# Revit family: Specialty_Equipment-Planter-Planters_Unlimited-Madera-Square-Rectangular
name_source: partatom
category: Specialty Equipment
units: mm (PartAtom-declared; Revit-internal decimal feet)

## family parameters
Always vertical = Yes
Cut with Voids When Loaded = No
Enable Cutting in Views = Yes
Maintain Annotation Orientation = No
OmniClass Number = 23.40.05.21.17
OmniClass Title = Planters
Part Type = Normal
Room Calculation Point = No
Round Connector Dimension = Use Diameter
Shared = No
Work Plane-Based = No

## types (1344) — shared parameters
Assembly Code = G2050600
CD_Height Max = 60"
CD_Height Min = 18"
CD_Length Max = 120"
CD_Length Min = 18"
CD_Offset = 0"
CD_Product Name = Madera Planter
CD_Product Page URL = https://www.plantersunlimited.com
CD_Specification = https://www.plantersunlimited.com
CD_Width Max = 72"
CD_Width Min = 12"
Default Elevation = 0"
Description = Modular Planting Bed
Manufacturer = Planters Unlimited
Material = Plastic-Fiberglass-Carlsbad-Faux Wood-Grey
Model = Madera Series Planters
Stiffeners Horizontal = Yes
Type Comments = Rectangular/Square Planter
URL = https://www.plantersunlimited.com

## per-type parameters (varying)
| type | CD_Height | CD_Length | CD_Requested Height | CD_Requested Length | CD_Requested Length Bottom | CD_Requested Width | CD_Requested Width Bottom | CD_Width | Center Divider | Center Divider Visibility by Length | Diagonal Support | Diagonal Support Visibility by Length | Rectangle Planter | Square Planter |
| Rectangular 18" x 12" x 18" | 18" | 18" | 18" | 18" | 12" | 12" | 8" | 12" | No | No | No | No | Yes | No |
| Rectangular 18" x 12" x 24" | 24" | 18" | 24" | 18" | 12" | 12" | 8" | 12" | No | No | No | No | Yes | No |
| Rectangular 18" x 12" x 30" | 30" | 18" | 30" | 18" | 12" | 12" | 8" | 12" | No | No | No | No | Yes | No |
| Rectangular 18" x 12" x 36" | 36" | 18" | 36" | 18" | 12" | 12" | 8" | 12" | No | No | No | No | Yes | No |
| Rectangular 18" x 15" x 18" | 18" | 18" | 18" | 18" | 12" | 15" | 10" | 15" | No | No | No | No | Yes | No |
| Rectangular 18" x 15" x 24" | 24" | 18" | 24" | 18" | 12" | 15" | 10" | 15" | No | No | No | No | Yes | No |
| Rectangular 18" x 15" x 30" | 30" | 18" | 30" | 18" | 12" | 15" | 10" | 15" | No | No | No | No | Yes | No |
| Rectangular 18" x 15" x 36" | 36" | 18" | 36" | 18" | 12" | 15" | 10" | 15" | No | No | No | No | Yes | No |
| Rectangular 18" x 15" x 42" | 42" | 18" | 42" | 18" | 12" | 15" | 10" | 15" | No | No | No | No | Yes | No |
| Rectangular 18" x 15" x 48" | 48" | 18" | 48" | 18" | 12" | 15" | 10" | 15" | No | No | No | No | Yes | No |
| Rectangular 18" x 15" x 54" | 54" | 18" | 54" | 18" | 12" | 15" | 10" | 15" | No | No | No | No | Yes | No |
| Rectangular 18" x 15" x 60" | 60" | 18" | 60" | 18" | 12" | 15" | 10" | 15" | No | No | No | No | Yes | No |
| Square 18" x 18" x 18" | 18" | 18" | 18" | 18" | 12" | 18" | 12" | 18" | No | No | No | No | No | Yes |
| Square 18" x 18" x 24" | 24" | 18" | 24" | 18" | 12" | 18" | 12" | 18" | No | No | No | No | No | Yes |
| Square 18" x 18" x 30" | 30" | 18" | 30" | 18" | 12" | 18" | 12" | 18" | No | No | No | No | No | Yes |
| Square 18" x 18" x 36" | 36" | 18" | 36" | 18" | 12" | 18" | 12" | 18" | No | No | No | No | No | Yes |
| Square 18" x 18" x 42" | 42" | 18" | 42" | 18" | 12" | 18" | 12" | 18" | No | No | No | No | No | Yes |
| Square 18" x 18" x 48" | 48" | 18" | 48" | 18" | 12" | 18" | 12" | 18" | No | No | No | No | No | Yes |
| Square 18" x 18" x 54" | 54" | 18" | 54" | 18" | 12" | 18" | 12" | 18" | No | No | No | No | No | Yes |
| Square 18" x 18" x 60" | 60" | 18" | 60" | 18" | 12" | 18" | 12" | 18" | No | No | No | No | No | Yes |
| Rectangular 18" x 24" x 18" | 18" | 18" | 18" | 18" | 12" | 24" | 16" | 24" | No | No | No | No | Yes | No |
| Rectangular 18" x 24" x 24" | 24" | 18" | 24" | 18" | 12" | 24" | 16" | 24" | No | No | No | No | Yes | No |
| Rectangular 18" x 24" x 30" | 30" | 18" | 30" | 18" | 12" | 24" | 16" | 24" | No | No | No | No | Yes | No |
| Rectangular 18" x 24" x 36" | 36" | 18" | 36" | 18" | 12" | 24" | 16" | 24" | No | No | No | No | Yes | No |
| Rectangular 18" x 24" x 42" | 42" | 18" | 42" | 18" | 12" | 24" | 16" | 24" | No | No | No | No | Yes | No |
| Rectangular 18" x 24" x 48" | 48" | 18" | 48" | 18" | 12" | 24" | 16" | 24" | No | No | No | No | Yes | No |
| Rectangular 18" x 24" x 54" | 54" | 18" | 54" | 18" | 12" | 24" | 16" | 24" | No | No | No | No | Yes | No |
| Rectangular 18" x 24" x 60" | 60" | 18" | 60" | 18" | 12" | 24" | 16" | 24" | No | No | No | No | Yes | No |
| Rectangular 18" x 30" x 18" | 18" | 18" | 18" | 18" | 12" | 30" | 20" | 30" | No | No | No | No | Yes | No |
| Rectangular 18" x 30" x 24" | 24" | 18" | 24" | 18" | 12" | 30" | 20" | 30" | No | No | No | No | Yes | No |
| Rectangular 18" x 30" x 30" | 30" | 18" | 30" | 18" | 12" | 30" | 20" | 30" | No | No | No | No | Yes | No |
| Rectangular 18" x 30" x 36" | 36" | 18" | 36" | 18" | 12" | 30" | 20" | 30" | No | No | No | No | Yes | No |
| Rectangular 18" x 30" x 42" | 42" | 18" | 42" | 18" | 12" | 30" | 20" | 30" | No | No | No | No | Yes | No |
| Rectangular 18" x 30" x 48" | 48" | 18" | 48" | 18" | 12" | 30" | 20" | 30" | No | No | No | No | Yes | No |
| Rectangular 18" x 30" x 54" | 54" | 18" | 54" | 18" | 12" | 30" | 20" | 30" | No | No | No | No | Yes | No |
| Rectangular 18" x 30" x 60" | 60" | 18" | 60" | 18" | 12" | 30" | 20" | 30" | No | No | No | No | Yes | No |
| Rectangular 18" x 36" x 18" | 18" | 18" | 18" | 18" | 12" | 36" | 24" | 36" | No | No | No | No | Yes | No |
| Rectangular 18" x 36" x 24" | 24" | 18" | 24" | 18" | 12" | 36" | 24" | 36" | No | No | No | No | Yes | No |
| Rectangular 18" x 36" x 30" | 30" | 18" | 30" | 18" | 12" | 36" | 24" | 36" | No | No | No | No | Yes | No |
| Rectangular 18" x 36" x 36" | 36" | 18" | 36" | 18" | 12" | 36" | 24" | 36" | No | No | No | No | Yes | No |
| Rectangular 18" x 36" x 42" | 42" | 18" | 42" | 18" | 12" | 36" | 24" | 36" | No | No | No | No | Yes | No |
| Rectangular 18" x 36" x 48" | 48" | 18" | 48" | 18" | 12" | 36" | 24" | 36" | No | No | No | No | Yes | No |
| Rectangular 18" x 36" x 54" | 54" | 18" | 54" | 18" | 12" | 36" | 24" | 36" | No | No | No | No | Yes | No |
| Rectangular 18" x 36" x 60" | 60" | 18" | 60" | 18" | 12" | 36" | 24" | 36" | No | No | No | No | Yes | No |
| Rectangular 18" x 42" x 18" | 18" | 18" | 18" | 18" | 12" | 42" | 28" | 42" | No | No | No | No | Yes | No |
| Rectangular 18" x 42" x 24" | 24" | 18" | 24" | 18" | 12" | 42" | 28" | 42" | No | No | No | No | Yes | No |
| Rectangular 18" x 42" x 30" | 30" | 18" | 30" | 18" | 12" | 42" | 28" | 42" | No | No | No | No | Yes | No |
| Rectangular 18" x 42" x 36" | 36" | 18" | 36" | 18" | 12" | 42" | 28" | 42" | No | No | No | No | Yes | No |
| Rectangular 18" x 42" x 42" | 42" | 18" | 42" | 18" | 12" | 42" | 28" | 42" | No | No | No | No | Yes | No |
| Rectangular 18" x 42" x 48" | 48" | 18" | 48" | 18" | 12" | 42" | 28" | 42" | No | No | No | No | Yes | No |
| Rectangular 18" x 42" x 54" | 54" | 18" | 54" | 18" | 12" | 42" | 28" | 42" | No | No | No | No | Yes | No |
| Rectangular 18" x 42" x 60" | 60" | 18" | 60" | 18" | 12" | 42" | 28" | 42" | No | No | No | No | Yes | No |
| Rectangular 18" x 48" x 18" | 18" | 18" | 18" | 18" | 12" | 48" | 32" | 48" | No | No | No | No | Yes | No |
| Rectangular 18" x 48" x 24" | 24" | 18" | 24" | 18" | 12" | 48" | 32" | 48" | No | No | No | No | Yes | No |
| Rectangular 18" x 48" x 30" | 30" | 18" | 30" | 18" | 12" | 48" | 32" | 48" | No | No | No | No | Yes | No |
| Rectangular 18" x 48" x 36" | 36" | 18" | 36" | 18" | 12" | 48" | 32" | 48" | No | No | No | No | Yes | No |
| Rectangular 18" x 48" x 42" | 42" | 18" | 42" | 18" | 12" | 48" | 32" | 48" | No | No | No | No | Yes | No |
| Rectangular 18" x 48" x 48" | 48" | 18" | 48" | 18" | 12" | 48" | 32" | 48" | No | No | No | No | Yes | No |
| Rectangular 18" x 48" x 54" | 54" | 18" | 54" | 18" | 12" | 48" | 32" | 48" | No | No | No | No | Yes | No |
| Rectangular 18" x 48" x 60" | 60" | 18" | 60" | 18" | 12" | 48" | 32" | 48" | No | No | No | No | Yes | No |
| Rectangular 18" x 60" x 18" | 18" | 18" | 18" | 18" | 12" | 60" | 40" | 60" | No | No | No | No | Yes | No |
| Rectangular 18" x 60" x 24" | 24" | 18" | 24" | 18" | 12" | 60" | 40" | 60" | No | No | No | No | Yes | No |
| Rectangular 18" x 60" x 30" | 30" | 18" | 30" | 18" | 12" | 60" | 40" | 60" | No | No | No | No | Yes | No |
| Rectangular 18" x 60" x 36" | 36" | 18" | 36" | 18" | 12" | 60" | 40" | 60" | No | No | No | No | Yes | No |
| Rectangular 18" x 60" x 42" | 42" | 18" | 42" | 18" | 12" | 60" | 40" | 60" | No | No | No | No | Yes | No |
| Rectangular 18" x 60" x 48" | 48" | 18" | 48" | 18" | 12" | 60" | 40" | 60" | No | No | No | No | Yes | No |
| Rectangular 18" x 60" x 54" | 54" | 18" | 54" | 18" | 12" | 60" | 40" | 60" | No | No | No | No | Yes | No |
| Rectangular 18" x 60" x 60" | 60" | 18" | 60" | 18" | 12" | 60" | 40" | 60" | No | No | No | No | Yes | No |
| Rectangular 18" x 66" x 18" | 18" | 18" | 18" | 18" | 12" | 66" | 44" | 66" | No | No | No | No | Yes | No |
| Rectangular 18" x 66" x 24" | 24" | 18" | 24" | 18" | 12" | 66" | 44" | 66" | No | No | No | No | Yes | No |
| Rectangular 18" x 66" x 30" | 30" | 18" | 30" | 18" | 12" | 66" | 44" | 66" | No | No | No | No | Yes | No |
| Rectangular 18" x 66" x 36" | 36" | 18" | 36" | 18" | 12" | 66" | 44" | 66" | No | No | No | No | Yes | No |
| Rectangular 18" x 66" x 42" | 42" | 18" | 42" | 18" | 12" | 66" | 44" | 66" | No | No | No | No | Yes | No |
| Rectangular 18" x 66" x 48" | 48" | 18" | 48" | 18" | 12" | 66" | 44" | 66" | No | No | No | No | Yes | No |
| Rectangular 18" x 66" x 54" | 54" | 18" | 54" | 18" | 12" | 66" | 44" | 66" | No | No | No | No | Yes | No |
| Rectangular 18" x 66" x 60" | 60" | 18" | 60" | 18" | 12" | 66" | 44" | 66" | No | No | No | No | Yes | No |
| Rectangular 18" x 72" x 18" | 18" | 18" | 18" | 18" | 12" | 72" | 48" | 72" | No | No | No | No | Yes | No |
| Rectangular 18" x 72" x 24" | 24" | 18" | 24" | 18" | 12" | 72" | 48" | 72" | No | No | No | No | Yes | No |
| Rectangular 18" x 72" x 30" | 30" | 18" | 30" | 18" | 12" | 72" | 48" | 72" | No | No | No | No | Yes | No |
| Rectangular 18" x 72" x 36" | 36" | 18" | 36" | 18" | 12" | 72" | 48" | 72" | No | No | No | No | Yes | No |
| Rectangular 18" x 72" x 42" | 42" | 18" | 42" | 18" | 12" | 72" | 48" | 72" | No | No | No | No | Yes | No |
| Rectangular 18" x 72" x 48" | 48" | 18" | 48" | 18" | 12" | 72" | 48" | 72" | No | No | No | No | Yes | No |
| Rectangular 18" x 72" x 54" | 54" | 18" | 54" | 18" | 12" | 72" | 48" | 72" | No | No | No | No | Yes | No |
| Rectangular 18" x 72" x 60" | 60" | 18" | 60" | 18" | 12" | 72" | 48" | 72" | No | No | No | No | Yes | No |
| Rectangular 24" x 12" x 18" | 18" | 24" | 18" | 24" | 16" | 12" | 8" | 12" | No | No | No | No | Yes | No |
| Rectangular 24" x 12" x 24" | 24" | 24" | 24" | 24" | 16" | 12" | 8" | 12" | No | No | No | No | Yes | No |
| Rectangular 24" x 12" x 30" | 30" | 24" | 30" | 24" | 16" | 12" | 8" | 12" | No | No | No | No | Yes | No |
| Rectangular 24" x 12" x 36" | 36" | 24" | 36" | 24" | 16" | 12" | 8" | 12" | No | No | No | No | Yes | No |
| Rectangular 24" x 15" x 18" | 18" | 24" | 18" | 24" | 16" | 15" | 10" | 15" | No | No | No | No | Yes | No |
| Rectangular 24" x 15" x 24" | 24" | 24" | 24" | 24" | 16" | 15" | 10" | 15" | No | No | No | No | Yes | No |
| Rectangular 24" x 15" x 30" | 30" | 24" | 30" | 24" | 16" | 15" | 10" | 15" | No | No | No | No | Yes | No |
| Rectangular 24" x 15" x 36" | 36" | 24" | 36" | 24" | 16" | 15" | 10" | 15" | No | No | No | No | Yes | No |
| Rectangular 24" x 15" x 42" | 42" | 24" | 42" | 24" | 16" | 15" | 10" | 15" | No | No | No | No | Yes | No |
| Rectangular 24" x 15" x 48" | 48" | 24" | 48" | 24" | 16" | 15" | 10" | 15" | No | No | No | No | Yes | No |
| Rectangular 24" x 15" x 54" | 54" | 24" | 54" | 24" | 16" | 15" | 10" | 15" | No | No | No | No | Yes | No |
| Rectangular 24" x 15" x 60" | 60" | 24" | 60" | 24" | 16" | 15" | 10" | 15" | No | No | No | No | Yes | No |
| Rectangular 24" x 18" x 18" | 18" | 24" | 18" | 24" | 16" | 18" | 12" | 18" | No | No | No | No | Yes | No |
| Rectangular 24" x 18" x 24" | 24" | 24" | 24" | 24" | 16" | 18" | 12" | 18" | No | No | No | No | Yes | No |
| Rectangular 24" x 18" x 30" | 30" | 24" | 30" | 24" | 16" | 18" | 12" | 18" | No | No | No | No | Yes | No |
| Rectangular 24" x 18" x 36" | 36" | 24" | 36" | 24" | 16" | 18" | 12" | 18" | No | No | No | No | Yes | No |
| Rectangular 24" x 18" x 42" | 42" | 24" | 42" | 24" | 16" | 18" | 12" | 18" | No | No | No | No | Yes | No |
| Rectangular 24" x 18" x 48" | 48" | 24" | 48" | 24" | 16" | 18" | 12" | 18" | No | No | No | No | Yes | No |
| Rectangular 24" x 18" x 54" | 54" | 24" | 54" | 24" | 16" | 18" | 12" | 18" | No | No | No | No | Yes | No |
| Rectangular 24" x 18" x 60" | 60" | 24" | 60" | 24" | 16" | 18" | 12" | 18" | No | No | No | No | Yes | No |
| Square 24" x 24" x 18" | 18" | 24" | 18" | 24" | 16" | 24" | 16" | 24" | No | No | No | No | No | Yes |
| Square 24" x 24" x 24" | 24" | 24" | 24" | 24" | 16" | 24" | 16" | 24" | No | No | No | No | No | Yes |
| Square 24" x 24" x 30" | 30" | 24" | 30" | 24" | 16" | 24" | 16" | 24" | No | No | No | No | No | Yes |
| Square 24" x 24" x 36" | 36" | 24" | 36" | 24" | 16" | 24" | 16" | 24" | No | No | No | No | No | Yes |
| Square 24" x 24" x 42" | 42" | 24" | 42" | 24" | 16" | 24" | 16" | 24" | No | No | No | No | No | Yes |
| Square 24" x 24" x 48" | 48" | 24" | 48" | 24" | 16" | 24" | 16" | 24" | No | No | No | No | No | Yes |
| Square 24" x 24" x 54" | 54" | 24" | 54" | 24" | 16" | 24" | 16" | 24" | No | No | No | No | No | Yes |
| Square 24" x 24" x 60" | 60" | 24" | 60" | 24" | 16" | 24" | 16" | 24" | No | No | No | No | No | Yes |
| Rectangular 24" x 30" x 18" | 18" | 24" | 18" | 24" | 16" | 30" | 20" | 30" | No | No | No | No | Yes | No |
| Rectangular 24" x 30" x 24" | 24" | 24" | 24" | 24" | 16" | 30" | 20" | 30" | No | No | No | No | Yes | No |
| Rectangular 24" x 30" x 30" | 30" | 24" | 30" | 24" | 16" | 30" | 20" | 30" | No | No | No | No | Yes | No |
| Rectangular 24" x 30" x 36" | 36" | 24" | 36" | 24" | 16" | 30" | 20" | 30" | No | No | No | No | Yes | No |
| Rectangular 24" x 30" x 42" | 42" | 24" | 42" | 24" | 16" | 30" | 20" | 30" | No | No | No | No | Yes | No |
| Rectangular 24" x 30" x 48" | 48" | 24" | 48" | 24" | 16" | 30" | 20" | 30" | No | No | No | No | Yes | No |
| Rectangular 24" x 30" x 54" | 54" | 24" | 54" | 24" | 16" | 30" | 20" | 30" | No | No | No | No | Yes | No |
| Rectangular 24" x 30" x 60" | 60" | 24" | 60" | 24" | 16" | 30" | 20" | 30" | No | No | No | No | Yes | No |
| Rectangular 24" x 36" x 18" | 18" | 24" | 18" | 24" | 16" | 36" | 24" | 36" | No | No | No | No | Yes | No |
| Rectangular 24" x 36" x 24" | 24" | 24" | 24" | 24" | 16" | 36" | 24" | 36" | No | No | No | No | Yes | No |
| Rectangular 24" x 36" x 30" | 30" | 24" | 30" | 24" | 16" | 36" | 24" | 36" | No | No | No | No | Yes | No |
| Rectangular 24" x 36" x 36" | 36" | 24" | 36" | 24" | 16" | 36" | 24" | 36" | No | No | No | No | Yes | No |
| Rectangular 24" x 36" x 42" | 42" | 24" | 42" | 24" | 16" | 36" | 24" | 36" | No | No | No | No | Yes | No |
| Rectangular 24" x 36" x 48" | 48" | 24" | 48" | 24" | 16" | 36" | 24" | 36" | No | No | No | No | Yes | No |
| Rectangular 24" x 36" x 54" | 54" | 24" | 54" | 24" | 16" | 36" | 24" | 36" | No | No | No | No | Yes | No |
| Rectangular 24" x 36" x 60" | 60" | 24" | 60" | 24" | 16" | 36" | 24" | 36" | No | No | No | No | Yes | No |
| Rectangular 24" x 42" x 18" | 18" | 24" | 18" | 24" | 16" | 42" | 28" | 42" | No | No | No | No | Yes | No |
| Rectangular 24" x 42" x 24" | 24" | 24" | 24" | 24" | 16" | 42" | 28" | 42" | No | No | No | No | Yes | No |
| Rectangular 24" x 42" x 30" | 30" | 24" | 30" | 24" | 16" | 42" | 28" | 42" | No | No | No | No | Yes | No |
| Rectangular 24" x 42" x 36" | 36" | 24" | 36" | 24" | 16" | 42" | 28" | 42" | No | No | No | No | Yes | No |
| Rectangular 24" x 42" x 42" | 42" | 24" | 42" | 24" | 16" | 42" | 28" | 42" | No | No | No | No | Yes | No |
| Rectangular 24" x 42" x 48" | 48" | 24" | 48" | 24" | 16" | 42" | 28" | 42" | No | No | No | No | Yes | No |
| Rectangular 24" x 42" x 54" | 54" | 24" | 54" | 24" | 16" | 42" | 28" | 42" | No | No | No | No | Yes | No |
| Rectangular 24" x 42" x 60" | 60" | 24" | 60" | 24" | 16" | 42" | 28" | 42" | No | No | No | No | Yes | No |
| Rectangular 24" x 48" x 18" | 18" | 24" | 18" | 24" | 16" | 48" | 32" | 48" | No | No | No | No | Yes | No |
| Rectangular 24" x 48" x 24" | 24" | 24" | 24" | 24" | 16" | 48" | 32" | 48" | No | No | No | No | Yes | No |
| Rectangular 24" x 48" x 30" | 30" | 24" | 30" | 24" | 16" | 48" | 32" | 48" | No | No | No | No | Yes | No |
| Rectangular 24" x 48" x 36" | 36" | 24" | 36" | 24" | 16" | 48" | 32" | 48" | No | No | No | No | Yes | No |
| Rectangular 24" x 48" x 42" | 42" | 24" | 42" | 24" | 16" | 48" | 32" | 48" | No | No | No | No | Yes | No |
| Rectangular 24" x 48" x 48" | 48" | 24" | 48" | 24" | 16" | 48" | 32" | 48" | No | No | No | No | Yes | No |
| Rectangular 24" x 48" x 54" | 54" | 24" | 54" | 24" | 16" | 48" | 32" | 48" | No | No | No | No | Yes | No |
| Rectangular 24" x 48" x 60" | 60" | 24" | 60" | 24" | 16" | 48" | 32" | 48" | No | No | No | No | Yes | No |
| Rectangular 24" x 60" x 18" | 18" | 24" | 18" | 24" | 16" | 60" | 40" | 60" | No | No | No | No | Yes | No |
| Rectangular 24" x 60" x 24" | 24" | 24" | 24" | 24" | 16" | 60" | 40" | 60" | No | No | No | No | Yes | No |
| Rectangular 24" x 60" x 30" | 30" | 24" | 30" | 24" | 16" | 60" | 40" | 60" | No | No | No | No | Yes | No |
| Rectangular 24" x 60" x 36" | 36" | 24" | 36" | 24" | 16" | 60" | 40" | 60" | No | No | No | No | Yes | No |
| Rectangular 24" x 60" x 42" | 42" | 24" | 42" | 24" | 16" | 60" | 40" | 60" | No | No | No | No | Yes | No |
| Rectangular 24" x 60" x 48" | 48" | 24" | 48" | 24" | 16" | 60" | 40" | 60" | No | No | No | No | Yes | No |
| Rectangular 24" x 60" x 54" | 54" | 24" | 54" | 24" | 16" | 60" | 40" | 60" | No | No | No | No | Yes | No |
| Rectangular 24" x 60" x 60" | 60" | 24" | 60" | 24" | 16" | 60" | 40" | 60" | No | No | No | No | Yes | No |
| Rectangular 24" x 66" x 18" | 18" | 24" | 18" | 24" | 16" | 66" | 44" | 66" | No | No | No | No | Yes | No |
| Rectangular 24" x 66" x 24" | 24" | 24" | 24" | 24" | 16" | 66" | 44" | 66" | No | No | No | No | Yes | No |
| Rectangular 24" x 66" x 30" | 30" | 24" | 30" | 24" | 16" | 66" | 44" | 66" | No | No | No | No | Yes | No |
| Rectangular 24" x 66" x 36" | 36" | 24" | 36" | 24" | 16" | 66" | 44" | 66" | No | No | No | No | Yes | No |
| Rectangular 24" x 66" x 42" | 42" | 24" | 42" | 24" | 16" | 66" | 44" | 66" | No | No | No | No | Yes | No |
| Rectangular 24" x 66" x 48" | 48" | 24" | 48" | 24" | 16" | 66" | 44" | 66" | No | No | No | No | Yes | No |
| Rectangular 24" x 66" x 54" | 54" | 24" | 54" | 24" | 16" | 66" | 44" | 66" | No | No | No | No | Yes | No |
| Rectangular 24" x 66" x 60" | 60" | 24" | 60" | 24" | 16" | 66" | 44" | 66" | No | No | No | No | Yes | No |
| Rectangular 24" x 72" x 18" | 18" | 24" | 18" | 24" | 16" | 72" | 48" | 72" | No | No | No | No | Yes | No |
| Rectangular 24" x 72" x 24" | 24" | 24" | 24" | 24" | 16" | 72" | 48" | 72" | No | No | No | No | Yes | No |
| Rectangular 24" x 72" x 30" | 30" | 24" | 30" | 24" | 16" | 72" | 48" | 72" | No | No | No | No | Yes | No |
| Rectangular 24" x 72" x 36" | 36" | 24" | 36" | 24" | 16" | 72" | 48" | 72" | No | No | No | No | Yes | No |
| Rectangular 24" x 72" x 42" | 42" | 24" | 42" | 24" | 16" | 72" | 48" | 72" | No | No | No | No | Yes | No |
| Rectangular 24" x 72" x 48" | 48" | 24" | 48" | 24" | 16" | 72" | 48" | 72" | No | No | No | No | Yes | No |
| Rectangular 24" x 72" x 54" | 54" | 24" | 54" | 24" | 16" | 72" | 48" | 72" | No | No | No | No | Yes | No |
| Rectangular 24" x 72" x 60" | 60" | 24" | 60" | 24" | 16" | 72" | 48" | 72" | No | No | No | No | Yes | No |
| Rectangular 30" x 12" x 18" | 18" | 30" | 18" | 30" | 20" | 12" | 8" | 12" | No | No | No | No | Yes | No |
| Rectangular 30" x 12" x 24" | 24" | 30" | 24" | 30" | 20" | 12" | 8" | 12" | No | No | No | No | Yes | No |
| Rectangular 30" x 12" x 30" | 30" | 30" | 30" | 30" | 20" | 12" | 8" | 12" | No | No | No | No | Yes | No |
| Rectangular 30" x 12" x 36" | 36" | 30" | 36" | 30" | 20" | 12" | 8" | 12" | No | No | No | No | Yes | No |
| Rectangular 30" x 15" x 18" | 18" | 30" | 18" | 30" | 20" | 15" | 10" | 15" | No | No | No | No | Yes | No |
| Rectangular 30" x 15" x 24" | 24" | 30" | 24" | 30" | 20" | 15" | 10" | 15" | No | No | No | No | Yes | No |
| Rectangular 30" x 15" x 30" | 30" | 30" | 30" | 30" | 20" | 15" | 10" | 15" | No | No | No | No | Yes | No |
| Rectangular 30" x 15" x 36" | 36" | 30" | 36" | 30" | 20" | 15" | 10" | 15" | No | No | No | No | Yes | No |
| Rectangular 30" x 15" x 42" | 42" | 30" | 42" | 30" | 20" | 15" | 10" | 15" | No | No | No | No | Yes | No |
| Rectangular 30" x 15" x 48" | 48" | 30" | 48" | 30" | 20" | 15" | 10" | 15" | No | No | No | No | Yes | No |
| Rectangular 30" x 15" x 54" | 54" | 30" | 54" | 30" | 20" | 15" | 10" | 15" | No | No | No | No | Yes | No |
| Rectangular 30" x 15" x 60" | 60" | 30" | 60" | 30" | 20" | 15" | 10" | 15" | No | No | No | No | Yes | No |
| Rectangular 30" x 18" x 18" | 18" | 30" | 18" | 30" | 20" | 18" | 12" | 18" | No | No | No | No | Yes | No |
| Rectangular 30" x 18" x 24" | 24" | 30" | 24" | 30" | 20" | 18" | 12" | 18" | No | No | No | No | Yes | No |
| Rectangular 30" x 18" x 30" | 30" | 30" | 30" | 30" | 20" | 18" | 12" | 18" | No | No | No | No | Yes | No |
| Rectangular 30" x 18" x 36" | 36" | 30" | 36" | 30" | 20" | 18" | 12" | 18" | No | No | No | No | Yes | No |
| Rectangular 30" x 18" x 42" | 42" | 30" | 42" | 30" | 20" | 18" | 12" | 18" | No | No | No | No | Yes | No |
| Rectangular 30" x 18" x 48" | 48" | 30" | 48" | 30" | 20" | 18" | 12" | 18" | No | No | No | No | Yes | No |
| Rectangular 30" x 18" x 54" | 54" | 30" | 54" | 30" | 20" | 18" | 12" | 18" | No | No | No | No | Yes | No |
| Rectangular 30" x 18" x 60" | 60" | 30" | 60" | 30" | 20" | 18" | 12" | 18" | No | No | No | No | Yes | No |
| Rectangular 30" x 24" x 18" | 18" | 30" | 18" | 30" | 20" | 24" | 16" | 24" | No | No | No | No | Yes | No |
| Rectangular 30" x 24" x 24" | 24" | 30" | 24" | 30" | 20" | 24" | 16" | 24" | No | No | No | No | Yes | No |
| Rectangular 30" x 24" x 30" | 30" | 30" | 30" | 30" | 20" | 24" | 16" | 24" | No | No | No | No | Yes | No |
| Rectangular 30" x 24" x 36" | 36" | 30" | 36" | 30" | 20" | 24" | 16" | 24" | No | No | No | No | Yes | No |
| Rectangular 30" x 24" x 42" | 42" | 30" | 42" | 30" | 20" | 24" | 16" | 24" | No | No | No | No | Yes | No |
| Rectangular 30" x 24" x 48" | 48" | 30" | 48" | 30" | 20" | 24" | 16" | 24" | No | No | No | No | Yes | No |
| Rectangular 30" x 24" x 54" | 54" | 30" | 54" | 30" | 20" | 24" | 16" | 24" | No | No | No | No | Yes | No |
| Rectangular 30" x 24" x 60" | 60" | 30" | 60" | 30" | 20" | 24" | 16" | 24" | No | No | No | No | Yes | No |
| Square 30" x 30" x 18" | 18" | 30" | 18" | 30" | 20" | 30" | 20" | 30" | No | No | No | No | No | Yes |
| Square 30" x 30" x 24" | 24" | 30" | 24" | 30" | 20" | 30" | 20" | 30" | No | No | No | No | No | Yes |
| Square 30" x 30" x 30" | 30" | 30" | 30" | 30" | 20" | 30" | 20" | 30" | No | No | No | No | No | Yes |
| Square 30" x 30" x 36" | 36" | 30" | 36" | 30" | 20" | 30" | 20" | 30" | No | No | No | No | No | Yes |
| Square 30" x 30" x 42" | 42" | 30" | 42" | 30" | 20" | 30" | 20" | 30" | No | No | No | No | No | Yes |
| Square 30" x 30" x 48" | 48" | 30" | 48" | 30" | 20" | 30" | 20" | 30" | No | No | No | No | No | Yes |
| Square 30" x 30" x 54" | 54" | 30" | 54" | 30" | 20" | 30" | 20" | 30" | No | No | No | No | No | Yes |
| Square 30" x 30" x 60" | 60" | 30" | 60" | 30" | 20" | 30" | 20" | 30" | No | No | No | No | No | Yes |
| Rectangular 30" x 36" x 18" | 18" | 30" | 18" | 30" | 20" | 36" | 24" | 36" | No | No | No | No | Yes | No |
| Rectangular 30" x 36" x 24" | 24" | 30" | 24" | 30" | 20" | 36" | 24" | 36" | No | No | No | No | Yes | No |
| Rectangular 30" x 36" x 30" | 30" | 30" | 30" | 30" | 20" | 36" | 24" | 36" | No | No | No | No | Yes | No |
| Rectangular 30" x 36" x 36" | 36" | 30" | 36" | 30" | 20" | 36" | 24" | 36" | No | No | No | No | Yes | No |
| Rectangular 30" x 36" x 42" | 42" | 30" | 42" | 30" | 20" | 36" | 24" | 36" | No | No | No | No | Yes | No |
| Rectangular 30" x 36" x 48" | 48" | 30" | 48" | 30" | 20" | 36" | 24" | 36" | No | No | No | No | Yes | No |
| Rectangular 30" x 36" x 54" | 54" | 30" | 54" | 30" | 20" | 36" | 24" | 36" | No | No | No | No | Yes | No |
| Rectangular 30" x 36" x 60" | 60" | 30" | 60" | 30" | 20" | 36" | 24" | 36" | No | No | No | No | Yes | No |
| Rectangular 30" x 42" x 18" | 18" | 30" | 18" | 30" | 20" | 42" | 28" | 42" | No | No | No | No | Yes | No |
| Rectangular 30" x 42" x 24" | 24" | 30" | 24" | 30" | 20" | 42" | 28" | 42" | No | No | No | No | Yes | No |
| Rectangular 30" x 42" x 30" | 30" | 30" | 30" | 30" | 20" | 42" | 28" | 42" | No | No | No | No | Yes | No |
| Rectangular 30" x 42" x 36" | 36" | 30" | 36" | 30" | 20" | 42" | 28" | 42" | No | No | No | No | Yes | No |
| Rectangular 30" x 42" x 42" | 42" | 30" | 42" | 30" | 20" | 42" | 28" | 42" | No | No | No | No | Yes | No |
| Rectangular 30" x 42" x 48" | 48" | 30" | 48" | 30" | 20" | 42" | 28" | 42" | No | No | No | No | Yes | No |
| Rectangular 30" x 42" x 54" | 54" | 30" | 54" | 30" | 20" | 42" | 28" | 42" | No | No | No | No | Yes | No |
| Rectangular 30" x 42" x 60" | 60" | 30" | 60" | 30" | 20" | 42" | 28" | 42" | No | No | No | No | Yes | No |
| Rectangular 30" x 48" x 18" | 18" | 30" | 18" | 30" | 20" | 48" | 32" | 48" | No | No | No | No | Yes | No |
| Rectangular 30" x 48" x 24" | 24" | 30" | 24" | 30" | 20" | 48" | 32" | 48" | No | No | No | No | Yes | No |
| Rectangular 30" x 48" x 30" | 30" | 30" | 30" | 30" | 20" | 48" | 32" | 48" | No | No | No | No | Yes | No |
| Rectangular 30" x 48" x 36" | 36" | 30" | 36" | 30" | 20" | 48" | 32" | 48" | No | No | No | No | Yes | No |
| Rectangular 30" x 48" x 42" | 42" | 30" | 42" | 30" | 20" | 48" | 32" | 48" | No | No | No | No | Yes | No |
| Rectangular 30" x 48" x 48" | 48" | 30" | 48" | 30" | 20" | 48" | 32" | 48" | No | No | No | No | Yes | No |
| Rectangular 30" x 48" x 54" | 54" | 30" | 54" | 30" | 20" | 48" | 32" | 48" | No | No | No | No | Yes | No |
| Rectangular 30" x 48" x 60" | 60" | 30" | 60" | 30" | 20" | 48" | 32" | 48" | No | No | No | No | Yes | No |
| Rectangular 30" x 60" x 18" | 18" | 30" | 18" | 30" | 20" | 60" | 40" | 60" | No | No | No | No | Yes | No |
| Rectangular 30" x 60" x 24" | 24" | 30" | 24" | 30" | 20" | 60" | 40" | 60" | No | No | No | No | Yes | No |
| Rectangular 30" x 60" x 30" | 30" | 30" | 30" | 30" | 20" | 60" | 40" | 60" | No | No | No | No | Yes | No |
| Rectangular 30" x 60" x 36" | 36" | 30" | 36" | 30" | 20" | 60" | 40" | 60" | No | No | No | No | Yes | No |
| Rectangular 30" x 60" x 42" | 42" | 30" | 42" | 30" | 20" | 60" | 40" | 60" | No | No | No | No | Yes | No |
| Rectangular 30" x 60" x 48" | 48" | 30" | 48" | 30" | 20" | 60" | 40" | 60" | No | No | No | No | Yes | No |
| Rectangular 30" x 60" x 54" | 54" | 30" | 54" | 30" | 20" | 60" | 40" | 60" | No | No | No | No | Yes | No |
| Rectangular 30" x 60" x 60" | 60" | 30" | 60" | 30" | 20" | 60" | 40" | 60" | No | No | No | No | Yes | No |
| Rectangular 30" x 66" x 18" | 18" | 30" | 18" | 30" | 20" | 66" | 44" | 66" | No | No | No | No | Yes | No |
| Rectangular 30" x 66" x 24" | 24" | 30" | 24" | 30" | 20" | 66" | 44" | 66" | No | No | No | No | Yes | No |
| Rectangular 30" x 66" x 30" | 30" | 30" | 30" | 30" | 20" | 66" | 44" | 66" | No | No | No | No | Yes | No |
| Rectangular 30" x 66" x 36" | 36" | 30" | 36" | 30" | 20" | 66" | 44" | 66" | No | No | No | No | Yes | No |
| Rectangular 30" x 66" x 42" | 42" | 30" | 42" | 30" | 20" | 66" | 44" | 66" | No | No | No | No | Yes | No |
| Rectangular 30" x 66" x 48" | 48" | 30" | 48" | 30" | 20" | 66" | 44" | 66" | No | No | No | No | Yes | No |
| Rectangular 30" x 66" x 54" | 54" | 30" | 54" | 30" | 20" | 66" | 44" | 66" | No | No | No | No | Yes | No |
| Rectangular 30" x 66" x 60" | 60" | 30" | 60" | 30" | 20" | 66" | 44" | 66" | No | No | No | No | Yes | No |
| Rectangular 30" x 72" x 18" | 18" | 30" | 18" | 30" | 20" | 72" | 48" | 72" | No | No | No | No | Yes | No |
| Rectangular 30" x 72" x 24" | 24" | 30" | 24" | 30" | 20" | 72" | 48" | 72" | No | No | No | No | Yes | No |
| Rectangular 30" x 72" x 30" | 30" | 30" | 30" | 30" | 20" | 72" | 48" | 72" | No | No | No | No | Yes | No |
| Rectangular 30" x 72" x 36" | 36" | 30" | 36" | 30" | 20" | 72" | 48" | 72" | No | No | No | No | Yes | No |
| Rectangular 30" x 72" x 42" | 42" | 30" | 42" | 30" | 20" | 72" | 48" | 72" | No | No | No | No | Yes | No |
| Rectangular 30" x 72" x 48" | 48" | 30" | 48" | 30" | 20" | 72" | 48" | 72" | No | No | No | No | Yes | No |
| Rectangular 30" x 72" x 54" | 54" | 30" | 54" | 30" | 20" | 72" | 48" | 72" | No | No | No | No | Yes | No |
| Rectangular 30" x 72" x 60" | 60" | 30" | 60" | 30" | 20" | 72" | 48" | 72" | No | No | No | No | Yes | No |
| Rectangular 36" x 12" x 18" | 18" | 36" | 18" | 36" | 24" | 12" | 8" | 12" | No | No | No | No | Yes | No |
| Rectangular 36" x 12" x 24" | 24" | 36" | 24" | 36" | 24" | 12" | 8" | 12" | No | No | No | No | Yes | No |
| Rectangular 36" x 12" x 30" | 30" | 36" | 30" | 36" | 24" | 12" | 8" | 12" | No | No | No | No | Yes | No |
| Rectangular 36" x 12" x 36" | 36" | 36" | 36" | 36" | 24" | 12" | 8" | 12" | No | No | No | No | Yes | No |
| Rectangular 36" x 15" x 18" | 18" | 36" | 18" | 36" | 24" | 15" | 10" | 15" | No | No | No | No | Yes | No |
| Rectangular 36" x 15" x 24" | 24" | 36" | 24" | 36" | 24" | 15" | 10" | 15" | No | No | No | No | Yes | No |
| Rectangular 36" x 15" x 30" | 30" | 36" | 30" | 36" | 24" | 15" | 10" | 15" | No | No | No | No | Yes | No |
| Rectangular 36" x 15" x 36" | 36" | 36" | 36" | 36" | 24" | 15" | 10" | 15" | No | No | No | No | Yes | No |
| Rectangular 36" x 15" x 42" | 42" | 36" | 42" | 36" | 24" | 15" | 10" | 15" | No | No | No | No | Yes | No |
| Rectangular 36" x 15" x 48" | 48" | 36" | 48" | 36" | 24" | 15" | 10" | 15" | No | No | No | No | Yes | No |
| Rectangular 36" x 15" x 54" | 54" | 36" | 54" | 36" | 24" | 15" | 10" | 15" | No | No | No | No | Yes | No |
| Rectangular 36" x 15" x 60" | 60" | 36" | 60" | 36" | 24" | 15" | 10" | 15" | No | No | No | No | Yes | No |
| Rectangular 36" x 18" x 18" | 18" | 36" | 18" | 36" | 24" | 18" | 12" | 18" | No | No | No | No | Yes | No |
| Rectangular 36" x 18" x 24" | 24" | 36" | 24" | 36" | 24" | 18" | 12" | 18" | No | No | No | No | Yes | No |
| Rectangular 36" x 18" x 30" | 30" | 36" | 30" | 36" | 24" | 18" | 12" | 18" | No | No | No | No | Yes | No |
| Rectangular 36" x 18" x 36" | 36" | 36" | 36" | 36" | 24" | 18" | 12" | 18" | No | No | No | No | Yes | No |
| Rectangular 36" x 18" x 42" | 42" | 36" | 42" | 36" | 24" | 18" | 12" | 18" | No | No | No | No | Yes | No |
| Rectangular 36" x 18" x 48" | 48" | 36" | 48" | 36" | 24" | 18" | 12" | 18" | No | No | No | No | Yes | No |
| Rectangular 36" x 18" x 54" | 54" | 36" | 54" | 36" | 24" | 18" | 12" | 18" | No | No | No | No | Yes | No |
| Rectangular 36" x 18" x 60" | 60" | 36" | 60" | 36" | 24" | 18" | 12" | 18" | No | No | No | No | Yes | No |
| Rectangular 36" x 24" x 18" | 18" | 36" | 18" | 36" | 24" | 24" | 16" | 24" | No | No | No | No | Yes | No |
| Rectangular 36" x 24" x 24" | 24" | 36" | 24" | 36" | 24" | 24" | 16" | 24" | No | No | No | No | Yes | No |
| Rectangular 36" x 24" x 30" | 30" | 36" | 30" | 36" | 24" | 24" | 16" | 24" | No | No | No | No | Yes | No |
| Rectangular 36" x 24" x 36" | 36" | 36" | 36" | 36" | 24" | 24" | 16" | 24" | No | No | No | No | Yes | No |
| Rectangular 36" x 24" x 42" | 42" | 36" | 42" | 36" | 24" | 24" | 16" | 24" | No | No | No | No | Yes | No |
| Rectangular 36" x 24" x 48" | 48" | 36" | 48" | 36" | 24" | 24" | 16" | 24" | No | No | No | No | Yes | No |
| Rectangular 36" x 24" x 54" | 54" | 36" | 54" | 36" | 24" | 24" | 16" | 24" | No | No | No | No | Yes | No |
| Rectangular 36" x 24" x 60" | 60" | 36" | 60" | 36" | 24" | 24" | 16" | 24" | No | No | No | No | Yes | No |
| Rectangular 36" x 30" x 18" | 18" | 36" | 18" | 36" | 24" | 30" | 20" | 30" | No | No | No | No | Yes | No |
| Rectangular 36" x 30" x 24" | 24" | 36" | 24" | 36" | 24" | 30" | 20" | 30" | No | No | No | No | Yes | No |
| Rectangular 36" x 30" x 30" | 30" | 36" | 30" | 36" | 24" | 30" | 20" | 30" | No | No | No | No | Yes | No |
| Rectangular 36" x 30" x 36" | 36" | 36" | 36" | 36" | 24" | 30" | 20" | 30" | No | No | No | No | Yes | No |
| Rectangular 36" x 30" x 42" | 42" | 36" | 42" | 36" | 24" | 30" | 20" | 30" | No | No | No | No | Yes | No |
| Rectangular 36" x 30" x 48" | 48" | 36" | 48" | 36" | 24" | 30" | 20" | 30" | No | No | No | No | Yes | No |
| Rectangular 36" x 30" x 54" | 54" | 36" | 54" | 36" | 24" | 30" | 20" | 30" | No | No | No | No | Yes | No |
| Rectangular 36" x 30" x 60" | 60" | 36" | 60" | 36" | 24" | 30" | 20" | 30" | No | No | No | No | Yes | No |
| Square 36" x 36" x 18" | 18" | 36" | 18" | 36" | 24" | 36" | 24" | 36" | No | No | No | No | No | Yes |
| Square 36" x 36" x 24" | 24" | 36" | 24" | 36" | 24" | 36" | 24" | 36" | No | No | No | No | No | Yes |
| Square 36" x 36" x 30" | 30" | 36" | 30" | 36" | 24" | 36" | 24" | 36" | No | No | No | No | No | Yes |
| Square 36" x 36" x 36" | 36" | 36" | 36" | 36" | 24" | 36" | 24" | 36" | No | No | No | No | No | Yes |
| Square 36" x 36" x 42" | 42" | 36" | 42" | 36" | 24" | 36" | 24" | 36" | No | No | No | No | No | Yes |
| Square 36" x 36" x 48" | 48" | 36" | 48" | 36" | 24" | 36" | 24" | 36" | No | No | No | No | No | Yes |
| Square 36" x 36" x 54" | 54" | 36" | 54" | 36" | 24" | 36" | 24" | 36" | No | No | No | No | No | Yes |
| Square 36" x 36" x 60" | 60" | 36" | 60" | 36" | 24" | 36" | 24" | 36" | No | No | No | No | No | Yes |
| Rectangular 36" x 42" x 18" | 18" | 36" | 18" | 36" | 24" | 42" | 28" | 42" | No | No | No | No | Yes | No |
| Rectangular 36" x 42" x 24" | 24" | 36" | 24" | 36" | 24" | 42" | 28" | 42" | No | No | No | No | Yes | No |
| Rectangular 36" x 42" x 30" | 30" | 36" | 30" | 36" | 24" | 42" | 28" | 42" | No | No | No | No | Yes | No |
| Rectangular 36" x 42" x 36" | 36" | 36" | 36" | 36" | 24" | 42" | 28" | 42" | No | No | No | No | Yes | No |
| Rectangular 36" x 42" x 42" | 42" | 36" | 42" | 36" | 24" | 42" | 28" | 42" | No | No | No | No | Yes | No |
| Rectangular 36" x 42" x 48" | 48" | 36" | 48" | 36" | 24" | 42" | 28" | 42" | No | No | No | No | Yes | No |
| Rectangular 36" x 42" x 54" | 54" | 36" | 54" | 36" | 24" | 42" | 28" | 42" | No | No | No | No | Yes | No |
| Rectangular 36" x 42" x 60" | 60" | 36" | 60" | 36" | 24" | 42" | 28" | 42" | No | No | No | No | Yes | No |
| Rectangular 36" x 48" x 18" | 18" | 36" | 18" | 36" | 24" | 48" | 32" | 48" | No | No | No | No | Yes | No |
| Rectangular 36" x 48" x 24" | 24" | 36" | 24" | 36" | 24" | 48" | 32" | 48" | No | No | No | No | Yes | No |
| Rectangular 36" x 48" x 30" | 30" | 36" | 30" | 36" | 24" | 48" | 32" | 48" | No | No | No | No | Yes | No |
| Rectangular 36" x 48" x 36" | 36" | 36" | 36" | 36" | 24" | 48" | 32" | 48" | No | No | No | No | Yes | No |
| Rectangular 36" x 48" x 42" | 42" | 36" | 42" | 36" | 24" | 48" | 32" | 48" | No | No | No | No | Yes | No |
| Rectangular 36" x 48" x 48" | 48" | 36" | 48" | 36" | 24" | 48" | 32" | 48" | No | No | No | No | Yes | No |
| Rectangular 36" x 48" x 54" | 54" | 36" | 54" | 36" | 24" | 48" | 32" | 48" | No | No | No | No | Yes | No |
| Rectangular 36" x 48" x 60" | 60" | 36" | 60" | 36" | 24" | 48" | 32" | 48" | No | No | No | No | Yes | No |
| Rectangular 36" x 60" x 18" | 18" | 36" | 18" | 36" | 24" | 60" | 40" | 60" | No | No | No | No | Yes | No |
| Rectangular 36" x 60" x 24" | 24" | 36" | 24" | 36" | 24" | 60" | 40" | 60" | No | No | No | No | Yes | No |
| Rectangular 36" x 60" x 30" | 30" | 36" | 30" | 36" | 24" | 60" | 40" | 60" | No | No | No | No | Yes | No |
| Rectangular 36" x 60" x 36" | 36" | 36" | 36" | 36" | 24" | 60" | 40" | 60" | No | No | No | No | Yes | No |
| Rectangular 36" x 60" x 42" | 42" | 36" | 42" | 36" | 24" | 60" | 40" | 60" | No | No | No | No | Yes | No |
| Rectangular 36" x 60" x 48" | 48" | 36" | 48" | 36" | 24" | 60" | 40" | 60" | No | No | No | No | Yes | No |
| Rectangular 36" x 60" x 54" | 54" | 36" | 54" | 36" | 24" | 60" | 40" | 60" | No | No | No | No | Yes | No |
| Rectangular 36" x 60" x 60" | 60" | 36" | 60" | 36" | 24" | 60" | 40" | 60" | No | No | No | No | Yes | No |
| Rectangular 36" x 66" x 18" | 18" | 36" | 18" | 36" | 24" | 66" | 44" | 66" | No | No | No | No | Yes | No |
| Rectangular 36" x 66" x 24" | 24" | 36" | 24" | 36" | 24" | 66" | 44" | 66" | No | No | No | No | Yes | No |
| Rectangular 36" x 66" x 30" | 30" | 36" | 30" | 36" | 24" | 66" | 44" | 66" | No | No | No | No | Yes | No |
| Rectangular 36" x 66" x 36" | 36" | 36" | 36" | 36" | 24" | 66" | 44" | 66" | No | No | No | No | Yes | No |
| Rectangular 36" x 66" x 42" | 42" | 36" | 42" | 36" | 24" | 66" | 44" | 66" | No | No | No | No | Yes | No |
| Rectangular 36" x 66" x 48" | 48" | 36" | 48" | 36" | 24" | 66" | 44" | 66" | No | No | No | No | Yes | No |
| Rectangular 36" x 66" x 54" | 54" | 36" | 54" | 36" | 24" | 66" | 44" | 66" | No | No | No | No | Yes | No |
| Rectangular 36" x 66" x 60" | 60" | 36" | 60" | 36" | 24" | 66" | 44" | 66" | No | No | No | No | Yes | No |
| Rectangular 36" x 72" x 18" | 18" | 36" | 18" | 36" | 24" | 72" | 48" | 72" | No | No | No | No | Yes | No |
| Rectangular 36" x 72" x 24" | 24" | 36" | 24" | 36" | 24" | 72" | 48" | 72" | No | No | No | No | Yes | No |
| Rectangular 36" x 72" x 30" | 30" | 36" | 30" | 36" | 24" | 72" | 48" | 72" | No | No | No | No | Yes | No |
| Rectangular 36" x 72" x 36" | 36" | 36" | 36" | 36" | 24" | 72" | 48" | 72" | No | No | No | No | Yes | No |
| Rectangular 36" x 72" x 42" | 42" | 36" | 42" | 36" | 24" | 72" | 48" | 72" | No | No | No | No | Yes | No |
| Rectangular 36" x 72" x 48" | 48" | 36" | 48" | 36" | 24" | 72" | 48" | 72" | No | No | No | No | Yes | No |
| Rectangular 36" x 72" x 54" | 54" | 36" | 54" | 36" | 24" | 72" | 48" | 72" | No | No | No | No | Yes | No |
| Rectangular 36" x 72" x 60" | 60" | 36" | 60" | 36" | 24" | 72" | 48" | 72" | No | No | No | No | Yes | No |
| Rectangular 42" x 12" x 18" | 18" | 42" | 18" | 42" | 28" | 12" | 8" | 12" | No | No | No | No | Yes | No |
| Rectangular 42" x 12" x 24" | 24" | 42" | 24" | 42" | 28" | 12" | 8" | 12" | No | No | No | No | Yes | No |
| Rectangular 42" x 12" x 30" | 30" | 42" | 30" | 42" | 28" | 12" | 8" | 12" | No | No | No | No | Yes | No |
| Rectangular 42" x 12" x 36" | 36" | 42" | 36" | 42" | 28" | 12" | 8" | 12" | No | No | No | No | Yes | No |
| Rectangular 42" x 15" x 18" | 18" | 42" | 18" | 42" | 28" | 15" | 10" | 15" | No | No | No | No | Yes | No |
| Rectangular 42" x 15" x 24" | 24" | 42" | 24" | 42" | 28" | 15" | 10" | 15" | No | No | No | No | Yes | No |
| Rectangular 42" x 15" x 30" | 30" | 42" | 30" | 42" | 28" | 15" | 10" | 15" | No | No | No | No | Yes | No |
| Rectangular 42" x 15" x 36" | 36" | 42" | 36" | 42" | 28" | 15" | 10" | 15" | No | No | No | No | Yes | No |
| Rectangular 42" x 15" x 42" | 42" | 42" | 42" | 42" | 28" | 15" | 10" | 15" | No | No | No | No | Yes | No |
| Rectangular 42" x 15" x 48" | 48" | 42" | 48" | 42" | 28" | 15" | 10" | 15" | No | No | No | No | Yes | No |
| Rectangular 42" x 15" x 54" | 54" | 42" | 54" | 42" | 28" | 15" | 10" | 15" | No | No | No | No | Yes | No |
| Rectangular 42" x 15" x 60" | 60" | 42" | 60" | 42" | 28" | 15" | 10" | 15" | No | No | No | No | Yes | No |
| Rectangular 42" x 18" x 18" | 18" | 42" | 18" | 42" | 28" | 18" | 12" | 18" | No | No | No | No | Yes | No |
| Rectangular 42" x 18" x 24" | 24" | 42" | 24" | 42" | 28" | 18" | 12" | 18" | No | No | No | No | Yes | No |
| Rectangular 42" x 18" x 30" | 30" | 42" | 30" | 42" | 28" | 18" | 12" | 18" | No | No | No | No | Yes | No |
| Rectangular 42" x 18" x 36" | 36" | 42" | 36" | 42" | 28" | 18" | 12" | 18" | No | No | No | No | Yes | No |
| Rectangular 42" x 18" x 42" | 42" | 42" | 42" | 42" | 28" | 18" | 12" | 18" | No | No | No | No | Yes | No |
| Rectangular 42" x 18" x 48" | 48" | 42" | 48" | 42" | 28" | 18" | 12" | 18" | No | No | No | No | Yes | No |
| Rectangular 42" x 18" x 54" | 54" | 42" | 54" | 42" | 28" | 18" | 12" | 18" | No | No | No | No | Yes | No |
| Rectangular 42" x 18" x 60" | 60" | 42" | 60" | 42" | 28" | 18" | 12" | 18" | No | No | No | No | Yes | No |
| Rectangular 42" x 24" x 18" | 18" | 42" | 18" | 42" | 28" | 24" | 16" | 24" | No | No | No | No | Yes | No |
| Rectangular 42" x 24" x 24" | 24" | 42" | 24" | 42" | 28" | 24" | 16" | 24" | No | No | No | No | Yes | No |
| Rectangular 42" x 24" x 30" | 30" | 42" | 30" | 42" | 28" | 24" | 16" | 24" | No | No | No | No | Yes | No |
| Rectangular 42" x 24" x 36" | 36" | 42" | 36" | 42" | 28" | 24" | 16" | 24" | No | No | No | No | Yes | No |
| Rectangular 42" x 24" x 42" | 42" | 42" | 42" | 42" | 28" | 24" | 16" | 24" | No | No | No | No | Yes | No |
| Rectangular 42" x 24" x 48" | 48" | 42" | 48" | 42" | 28" | 24" | 16" | 24" | No | No | No | No | Yes | No |
| Rectangular 42" x 24" x 54" | 54" | 42" | 54" | 42" | 28" | 24" | 16" | 24" | No | No | No | No | Yes | No |
| Rectangular 42" x 24" x 60" | 60" | 42" | 60" | 42" | 28" | 24" | 16" | 24" | No | No | No | No | Yes | No |
| Rectangular 42" x 30" x 18" | 18" | 42" | 18" | 42" | 28" | 30" | 20" | 30" | No | No | No | No | Yes | No |
| Rectangular 42" x 30" x 24" | 24" | 42" | 24" | 42" | 28" | 30" | 20" | 30" | No | No | No | No | Yes | No |
| Rectangular 42" x 30" x 30" | 30" | 42" | 30" | 42" | 28" | 30" | 20" | 30" | No | No | No | No | Yes | No |
| Rectangular 42" x 30" x 36" | 36" | 42" | 36" | 42" | 28" | 30" | 20" | 30" | No | No | No | No | Yes | No |
| Rectangular 42" x 30" x 42" | 42" | 42" | 42" | 42" | 28" | 30" | 20" | 30" | No | No | No | No | Yes | No |
| Rectangular 42" x 30" x 48" | 48" | 42" | 48" | 42" | 28" | 30" | 20" | 30" | No | No | No | No | Yes | No |
| Rectangular 42" x 30" x 54" | 54" | 42" | 54" | 42" | 28" | 30" | 20" | 30" | No | No | No | No | Yes | No |
| Rectangular 42" x 30" x 60" | 60" | 42" | 60" | 42" | 28" | 30" | 20" | 30" | No | No | No | No | Yes | No |
| Rectangular 42" x 36" x 18" | 18" | 42" | 18" | 42" | 28" | 36" | 24" | 36" | No | No | No | No | Yes | No |
| Rectangular 42" x 36" x 24" | 24" | 42" | 24" | 42" | 28" | 36" | 24" | 36" | No | No | No | No | Yes | No |
| Rectangular 42" x 36" x 30" | 30" | 42" | 30" | 42" | 28" | 36" | 24" | 36" | No | No | No | No | Yes | No |
| Rectangular 42" x 36" x 36" | 36" | 42" | 36" | 42" | 28" | 36" | 24" | 36" | No | No | No | No | Yes | No |
| Rectangular 42" x 36" x 42" | 42" | 42" | 42" | 42" | 28" | 36" | 24" | 36" | No | No | No | No | Yes | No |
| Rectangular 42" x 36" x 48" | 48" | 42" | 48" | 42" | 28" | 36" | 24" | 36" | No | No | No | No | Yes | No |
| Rectangular 42" x 36" x 54" | 54" | 42" | 54" | 42" | 28" | 36" | 24" | 36" | No | No | No | No | Yes | No |
| Rectangular 42" x 36" x 60" | 60" | 42" | 60" | 42" | 28" | 36" | 24" | 36" | No | No | No | No | Yes | No |
| Square 42" x 42" x 18" | 18" | 42" | 18" | 42" | 28" | 42" | 28" | 42" | No | No | No | No | No | Yes |
| Square 42" x 42" x 24" | 24" | 42" | 24" | 42" | 28" | 42" | 28" | 42" | No | No | No | No | No | Yes |
| Square 42" x 42" x 30" | 30" | 42" | 30" | 42" | 28" | 42" | 28" | 42" | No | No | No | No | No | Yes |
| Square 42" x 42" x 36" | 36" | 42" | 36" | 42" | 28" | 42" | 28" | 42" | No | No | No | No | No | Yes |
| Square 42" x 42" x 42" | 42" | 42" | 42" | 42" | 28" | 42" | 28" | 42" | No | No | No | No | No | Yes |
| Square 42" x 42" x 48" | 48" | 42" | 48" | 42" | 28" | 42" | 28" | 42" | No | No | No | No | No | Yes |
| Square 42" x 42" x 54" | 54" | 42" | 54" | 42" | 28" | 42" | 28" | 42" | No | No | No | No | No | Yes |
| Square 42" x 42" x 60" | 60" | 42" | 60" | 42" | 28" | 42" | 28" | 42" | No | No | No | No | No | Yes |
| Rectangular 42" x 48" x 18" | 18" | 42" | 18" | 42" | 28" | 48" | 32" | 48" | No | No | No | No | Yes | No |
| Rectangular 42" x 48" x 24" | 24" | 42" | 24" | 42" | 28" | 48" | 32" | 48" | No | No | No | No | Yes | No |
| Rectangular 42" x 48" x 30" | 30" | 42" | 30" | 42" | 28" | 48" | 32" | 48" | No | No | No | No | Yes | No |
| Rectangular 42" x 48" x 36" | 36" | 42" | 36" | 42" | 28" | 48" | 32" | 48" | No | No | No | No | Yes | No |
| Rectangular 42" x 48" x 42" | 42" | 42" | 42" | 42" | 28" | 48" | 32" | 48" | No | No | No | No | Yes | No |
| Rectangular 42" x 48" x 48" | 48" | 42" | 48" | 42" | 28" | 48" | 32" | 48" | No | No | No | No | Yes | No |
| Rectangular 42" x 48" x 54" | 54" | 42" | 54" | 42" | 28" | 48" | 32" | 48" | No | No | No | No | Yes | No |
| Rectangular 42" x 48" x 60" | 60" | 42" | 60" | 42" | 28" | 48" | 32" | 48" | No | No | No | No | Yes | No |
| Rectangular 42" x 60" x 18" | 18" | 42" | 18" | 42" | 28" | 60" | 40" | 60" | No | No | No | No | Yes | No |
| Rectangular 42" x 60" x 24" | 24" | 42" | 24" | 42" | 28" | 60" | 40" | 60" | No | No | No | No | Yes | No |
| Rectangular 42" x 60" x 30" | 30" | 42" | 30" | 42" | 28" | 60" | 40" | 60" | No | No | No | No | Yes | No |
| Rectangular 42" x 60" x 36" | 36" | 42" | 36" | 42" | 28" | 60" | 40" | 60" | No | No | No | No | Yes | No |
| Rectangular 42" x 60" x 42" | 42" | 42" | 42" | 42" | 28" | 60" | 40" | 60" | No | No | No | No | Yes | No |
| Rectangular 42" x 60" x 48" | 48" | 42" | 48" | 42" | 28" | 60" | 40" | 60" | No | No | No | No | Yes | No |
| Rectangular 42" x 60" x 54" | 54" | 42" | 54" | 42" | 28" | 60" | 40" | 60" | No | No | No | No | Yes | No |
| Rectangular 42" x 60" x 60" | 60" | 42" | 60" | 42" | 28" | 60" | 40" | 60" | No | No | No | No | Yes | No |
| Rectangular 42" x 66" x 18" | 18" | 42" | 18" | 42" | 28" | 66" | 44" | 66" | No | No | No | No | Yes | No |
| Rectangular 42" x 66" x 24" | 24" | 42" | 24" | 42" | 28" | 66" | 44" | 66" | No | No | No | No | Yes | No |
| Rectangular 42" x 66" x 30" | 30" | 42" | 30" | 42" | 28" | 66" | 44" | 66" | No | No | No | No | Yes | No |
| Rectangular 42" x 66" x 36" | 36" | 42" | 36" | 42" | 28" | 66" | 44" | 66" | No | No | No | No | Yes | No |
| Rectangular 42" x 66" x 42" | 42" | 42" | 42" | 42" | 28" | 66" | 44" | 66" | No | No | No | No | Yes | No |
| Rectangular 42" x 66" x 48" | 48" | 42" | 48" | 42" | 28" | 66" | 44" | 66" | No | No | No | No | Yes | No |
| Rectangular 42" x 66" x 54" | 54" | 42" | 54" | 42" | 28" | 66" | 44" | 66" | No | No | No | No | Yes | No |
| Rectangular 42" x 66" x 60" | 60" | 42" | 60" | 42" | 28" | 66" | 44" | 66" | No | No | No | No | Yes | No |
| Rectangular 42" x 72" x 18" | 18" | 42" | 18" | 42" | 28" | 72" | 48" | 72" | No | No | No | No | Yes | No |
| Rectangular 42" x 72" x 24" | 24" | 42" | 24" | 42" | 28" | 72" | 48" | 72" | No | No | No | No | Yes | No |
| Rectangular 42" x 72" x 30" | 30" | 42" | 30" | 42" | 28" | 72" | 48" | 72" | No | No | No | No | Yes | No |
| Rectangular 42" x 72" x 36" | 36" | 42" | 36" | 42" | 28" | 72" | 48" | 72" | No | No | No | No | Yes | No |
| Rectangular 42" x 72" x 42" | 42" | 42" | 42" | 42" | 28" | 72" | 48" | 72" | No | No | No | No | Yes | No |
| Rectangular 42" x 72" x 48" | 48" | 42" | 48" | 42" | 28" | 72" | 48" | 72" | No | No | No | No | Yes | No |
| Rectangular 42" x 72" x 54" | 54" | 42" | 54" | 42" | 28" | 72" | 48" | 72" | No | No | No | No | Yes | No |
| Rectangular 42" x 72" x 60" | 60" | 42" | 60" | 42" | 28" | 72" | 48" | 72" | No | No | No | No | Yes | No |
| Rectangular 48" x 12" x 18" | 18" | 48" | 18" | 48" | 32" | 12" | 8" | 12" | No | No | No | Yes | Yes | No |
| Rectangular 48" x 12" x 24" | 24" | 48" | 24" | 48" | 32" | 12" | 8" | 12" | No | No | No | Yes | Yes | No |
| Rectangular 48" x 12" x 30" | 30" | 48" | 30" | 48" | 32" | 12" | 8" | 12" | No | No | No | Yes | Yes | No |
| Rectangular 48" x 12" x 36" | 36" | 48" | 36" | 48" | 32" | 12" | 8" | 12" | No | No | No | Yes | Yes | No |
| Rectangular 48" x 15" x 18" | 18" | 48" | 18" | 48" | 32" | 15" | 10" | 15" | No | No | No | Yes | Yes | No |
| Rectangular 48" x 15" x 24" | 24" | 48" | 24" | 48" | 32" | 15" | 10" | 15" | No | No | No | Yes | Yes | No |
| Rectangular 48" x 15" x 30" | 30" | 48" | 30" | 48" | 32" | 15" | 10" | 15" | No | No | No | Yes | Yes | No |
| Rectangular 48" x 15" x 36" | 36" | 48" | 36" | 48" | 32" | 15" | 10" | 15" | No | No | No | Yes | Yes | No |
| Rectangular 48" x 15" x 42" | 42" | 48" | 42" | 48" | 32" | 15" | 10" | 15" | No | No | No | Yes | Yes | No |
| Rectangular 48" x 15" x 48" | 48" | 48" | 48" | 48" | 32" | 15" | 10" | 15" | No | No | No | Yes | Yes | No |
| Rectangular 48" x 15" x 54" | 54" | 48" | 54" | 48" | 32" | 15" | 10" | 15" | No | No | No | Yes | Yes | No |
| Rectangular 48" x 15" x 60" | 60" | 48" | 60" | 48" | 32" | 15" | 10" | 15" | No | No | No | Yes | Yes | No |
| Rectangular 48" x 18" x 18" | 18" | 48" | 18" | 48" | 32" | 18" | 12" | 18" | No | No | No | Yes | Yes | No |
| Rectangular 48" x 18" x 24" | 24" | 48" | 24" | 48" | 32" | 18" | 12" | 18" | No | No | No | Yes | Yes | No |
| Rectangular 48" x 18" x 30" | 30" | 48" | 30" | 48" | 32" | 18" | 12" | 18" | No | No | No | Yes | Yes | No |
| Rectangular 48" x 18" x 36" | 36" | 48" | 36" | 48" | 32" | 18" | 12" | 18" | No | No | No | Yes | Yes | No |
| Rectangular 48" x 18" x 42" | 42" | 48" | 42" | 48" | 32" | 18" | 12" | 18" | No | No | No | Yes | Yes | No |
| Rectangular 48" x 18" x 48" | 48" | 48" | 48" | 48" | 32" | 18" | 12" | 18" | No | No | No | Yes | Yes | No |
| Rectangular 48" x 18" x 54" | 54" | 48" | 54" | 48" | 32" | 18" | 12" | 18" | No | No | No | Yes | Yes | No |
| Rectangular 48" x 18" x 60" | 60" | 48" | 60" | 48" | 32" | 18" | 12" | 18" | No | No | No | Yes | Yes | No |
| Rectangular 48" x 24" x 18" | 18" | 48" | 18" | 48" | 32" | 24" | 16" | 24" | No | No | No | Yes | Yes | No |
| Rectangular 48" x 24" x 24" | 24" | 48" | 24" | 48" | 32" | 24" | 16" | 24" | No | No | No | Yes | Yes | No |
| Rectangular 48" x 24" x 30" | 30" | 48" | 30" | 48" | 32" | 24" | 16" | 24" | No | No | No | Yes | Yes | No |
| Rectangular 48" x 24" x 36" | 36" | 48" | 36" | 48" | 32" | 24" | 16" | 24" | No | No | No | Yes | Yes | No |
| Rectangular 48" x 24" x 42" | 42" | 48" | 42" | 48" | 32" | 24" | 16" | 24" | No | No | No | Yes | Yes | No |
| Rectangular 48" x 24" x 48" | 48" | 48" | 48" | 48" | 32" | 24" | 16" | 24" | No | No | No | Yes | Yes | No |
| Rectangular 48" x 24" x 54" | 54" | 48" | 54" | 48" | 32" | 24" | 16" | 24" | No | No | No | Yes | Yes | No |
| Rectangular 48" x 24" x 60" | 60" | 48" | 60" | 48" | 32" | 24" | 16" | 24" | No | No | No | Yes | Yes | No |
| Rectangular 48" x 30" x 18" | 18" | 48" | 18" | 48" | 32" | 30" | 20" | 30" | No | No | No | Yes | Yes | No |
| Rectangular 48" x 30" x 24" | 24" | 48" | 24" | 48" | 32" | 30" | 20" | 30" | No | No | No | Yes | Yes | No |
| Rectangular 48" x 30" x 30" | 30" | 48" | 30" | 48" | 32" | 30" | 20" | 30" | No | No | No | Yes | Yes | No |
| Rectangular 48" x 30" x 36" | 36" | 48" | 36" | 48" | 32" | 30" | 20" | 30" | No | No | No | Yes | Yes | No |
| Rectangular 48" x 30" x 42" | 42" | 48" | 42" | 48" | 32" | 30" | 20" | 30" | No | No | No | Yes | Yes | No |
| Rectangular 48" x 30" x 48" | 48" | 48" | 48" | 48" | 32" | 30" | 20" | 30" | No | No | No | Yes | Yes | No |
| Rectangular 48" x 30" x 54" | 54" | 48" | 54" | 48" | 32" | 30" | 20" | 30" | No | No | No | Yes | Yes | No |
| Rectangular 48" x 30" x 60" | 60" | 48" | 60" | 48" | 32" | 30" | 20" | 30" | No | No | No | Yes | Yes | No |
| Rectangular 48" x 36" x 18" | 18" | 48" | 18" | 48" | 32" | 36" | 24" | 36" | No | No | No | Yes | Yes | No |
| Rectangular 48" x 36" x 24" | 24" | 48" | 24" | 48" | 32" | 36" | 24" | 36" | No | No | No | Yes | Yes | No |
| Rectangular 48" x 36" x 30" | 30" | 48" | 30" | 48" | 32" | 36" | 24" | 36" | No | No | No | Yes | Yes | No |
| Rectangular 48" x 36" x 36" | 36" | 48" | 36" | 48" | 32" | 36" | 24" | 36" | No | No | No | Yes | Yes | No |
| Rectangular 48" x 36" x 42" | 42" | 48" | 42" | 48" | 32" | 36" | 24" | 36" | No | No | No | Yes | Yes | No |
| Rectangular 48" x 36" x 48" | 48" | 48" | 48" | 48" | 32" | 36" | 24" | 36" | No | No | No | Yes | Yes | No |
| Rectangular 48" x 36" x 54" | 54" | 48" | 54" | 48" | 32" | 36" | 24" | 36" | No | No | No | Yes | Yes | No |
| Rectangular 48" x 36" x 60" | 60" | 48" | 60" | 48" | 32" | 36" | 24" | 36" | No | No | No | Yes | Yes | No |
| Rectangular 48" x 42" x 18" | 18" | 48" | 18" | 48" | 32" | 42" | 28" | 42" | No | No | No | Yes | Yes | No |
| Rectangular 48" x 42" x 24" | 24" | 48" | 24" | 48" | 32" | 42" | 28" | 42" | No | No | No | Yes | Yes | No |
| Rectangular 48" x 42" x 30" | 30" | 48" | 30" | 48" | 32" | 42" | 28" | 42" | No | No | No | Yes | Yes | No |
| Rectangular 48" x 42" x 36" | 36" | 48" | 36" | 48" | 32" | 42" | 28" | 42" | No | No | No | Yes | Yes | No |
| Rectangular 48" x 42" x 42" | 42" | 48" | 42" | 48" | 32" | 42" | 28" | 42" | No | No | No | Yes | Yes | No |
| Rectangular 48" x 42" x 48" | 48" | 48" | 48" | 48" | 32" | 42" | 28" | 42" | No | No | No | Yes | Yes | No |
| Rectangular 48" x 42" x 54" | 54" | 48" | 54" | 48" | 32" | 42" | 28" | 42" | No | No | No | Yes | Yes | No |
| Rectangular 48" x 42" x 60" | 60" | 48" | 60" | 48" | 32" | 42" | 28" | 42" | No | No | No | Yes | Yes | No |
| Square 48" x 48" x 18" | 18" | 48" | 18" | 48" | 32" | 48" | 32" | 48" | No | No | Yes | Yes | No | Yes |
| Square 48" x 48" x 24" | 24" | 48" | 24" | 48" | 32" | 48" | 32" | 48" | No | No | Yes | Yes | No | Yes |
| Square 48" x 48" x 30" | 30" | 48" | 30" | 48" | 32" | 48" | 32" | 48" | No | No | Yes | Yes | No | Yes |
| Square 48" x 48" x 36" | 36" | 48" | 36" | 48" | 32" | 48" | 32" | 48" | No | No | Yes | Yes | No | Yes |
| Square 48" x 48" x 42" | 42" | 48" | 42" | 48" | 32" | 48" | 32" | 48" | No | No | Yes | Yes | No | Yes |
| Square 48" x 48" x 48" | 48" | 48" | 48" | 48" | 32" | 48" | 32" | 48" | No | No | Yes | Yes | No | Yes |
| Square 48" x 48" x 54" | 54" | 48" | 54" | 48" | 32" | 48" | 32" | 48" | No | No | Yes | Yes | No | Yes |
| Square 48" x 48" x 60" | 60" | 48" | 60" | 48" | 32" | 48" | 32" | 48" | No | No | Yes | Yes | No | Yes |
| Rectangular 48" x 60" x 18" | 18" | 48" | 18" | 48" | 32" | 60" | 40" | 60" | No | No | No | Yes | Yes | No |
| Rectangular 48" x 60" x 24" | 24" | 48" | 24" | 48" | 32" | 60" | 40" | 60" | No | No | No | Yes | Yes | No |
| Rectangular 48" x 60" x 30" | 30" | 48" | 30" | 48" | 32" | 60" | 40" | 60" | No | No | No | Yes | Yes | No |
| Rectangular 48" x 60" x 36" | 36" | 48" | 36" | 48" | 32" | 60" | 40" | 60" | No | No | No | Yes | Yes | No |
| Rectangular 48" x 60" x 42" | 42" | 48" | 42" | 48" | 32" | 60" | 40" | 60" | No | No | No | Yes | Yes | No |
| Rectangular 48" x 60" x 48" | 48" | 48" | 48" | 48" | 32" | 60" | 40" | 60" | No | No | No | Yes | Yes | No |
| Rectangular 48" x 60" x 54" | 54" | 48" | 54" | 48" | 32" | 60" | 40" | 60" | No | No | No | Yes | Yes | No |
| Rectangular 48" x 60" x 60" | 60" | 48" | 60" | 48" | 32" | 60" | 40" | 60" | No | No | No | Yes | Yes | No |
| Rectangular 48" x 66" x 18" | 18" | 48" | 18" | 48" | 32" | 66" | 44" | 66" | No | No | No | Yes | Yes | No |
| Rectangular 48" x 66" x 24" | 24" | 48" | 24" | 48" | 32" | 66" | 44" | 66" | No | No | No | Yes | Yes | No |
| Rectangular 48" x 66" x 30" | 30" | 48" | 30" | 48" | 32" | 66" | 44" | 66" | No | No | No | Yes | Yes | No |
| Rectangular 48" x 66" x 36" | 36" | 48" | 36" | 48" | 32" | 66" | 44" | 66" | No | No | No | Yes | Yes | No |
| Rectangular 48" x 66" x 42" | 42" | 48" | 42" | 48" | 32" | 66" | 44" | 66" | No | No | No | Yes | Yes | No |
| Rectangular 48" x 66" x 48" | 48" | 48" | 48" | 48" | 32" | 66" | 44" | 66" | No | No | No | Yes | Yes | No |
| Rectangular 48" x 66" x 54" | 54" | 48" | 54" | 48" | 32" | 66" | 44" | 66" | No | No | No | Yes | Yes | No |
| Rectangular 48" x 66" x 60" | 60" | 48" | 60" | 48" | 32" | 66" | 44" | 66" | No | No | No | Yes | Yes | No |
| Rectangular 48" x 72" x 18" | 18" | 48" | 18" | 48" | 32" | 72" | 48" | 72" | No | No | No | Yes | Yes | No |
| Rectangular 48" x 72" x 24" | 24" | 48" | 24" | 48" | 32" | 72" | 48" | 72" | No | No | No | Yes | Yes | No |
| Rectangular 48" x 72" x 30" | 30" | 48" | 30" | 48" | 32" | 72" | 48" | 72" | No | No | No | Yes | Yes | No |
| Rectangular 48" x 72" x 36" | 36" | 48" | 36" | 48" | 32" | 72" | 48" | 72" | No | No | No | Yes | Yes | No |
| Rectangular 48" x 72" x 42" | 42" | 48" | 42" | 48" | 32" | 72" | 48" | 72" | No | No | No | Yes | Yes | No |
| Rectangular 48" x 72" x 48" | 48" | 48" | 48" | 48" | 32" | 72" | 48" | 72" | No | No | No | Yes | Yes | No |
| Rectangular 48" x 72" x 54" | 54" | 48" | 54" | 48" | 32" | 72" | 48" | 72" | No | No | No | Yes | Yes | No |
| Rectangular 48" x 72" x 60" | 60" | 48" | 60" | 48" | 32" | 72" | 48" | 72" | No | No | No | Yes | Yes | No |
| Rectangular 54" x 12" x 18" | 18" | 54" | 18" | 54" | 36" | 12" | 8" | 12" | Yes | Yes | No | Yes | Yes | No |
| Rectangular 54" x 12" x 24" | 24" | 54" | 24" | 54" | 36" | 12" | 8" | 12" | Yes | Yes | No | Yes | Yes | No |
| Rectangular 54" x 12" x 30" | 30" | 54" | 30" | 54" | 36" | 12" | 8" | 12" | Yes | Yes | No | Yes | Yes | No |
| Rectangular 54" x 12" x 36" | 36" | 54" | 36" | 54" | 36" | 12" | 8" | 12" | Yes | Yes | No | Yes | Yes | No |
| Rectangular 54" x 15" x 18" | 18" | 54" | 18" | 54" | 36" | 15" | 10" | 15" | Yes | Yes | No | Yes | Yes | No |
| Rectangular 54" x 15" x 24" | 24" | 54" | 24" | 54" | 36" | 15" | 10" | 15" | Yes | Yes | No | Yes | Yes | No |
| Rectangular 54" x 15" x 30" | 30" | 54" | 30" | 54" | 36" | 15" | 10" | 15" | Yes | Yes | No | Yes | Yes | No |
| Rectangular 54" x 15" x 36" | 36" | 54" | 36" | 54" | 36" | 15" | 10" | 15" | Yes | Yes | No | Yes | Yes | No |
| Rectangular 54" x 15" x 42" | 42" | 54" | 42" | 54" | 36" | 15" | 10" | 15" | Yes | Yes | No | Yes | Yes | No |
| Rectangular 54" x 15" x 48" | 48" | 54" | 48" | 54" | 36" | 15" | 10" | 15" | Yes | Yes | No | Yes | Yes | No |
| Rectangular 54" x 15" x 54" | 54" | 54" | 54" | 54" | 36" | 15" | 10" | 15" | Yes | Yes | No | Yes | Yes | No |
| Rectangular 54" x 15" x 60" | 60" | 54" | 60" | 54" | 36" | 15" | 10" | 15" | Yes | Yes | No | Yes | Yes | No |
| Rectangular 54" x 18" x 18" | 18" | 54" | 18" | 54" | 36" | 18" | 12" | 18" | Yes | Yes | No | Yes | Yes | No |
| Rectangular 54" x 18" x 24" | 24" | 54" | 24" | 54" | 36" | 18" | 12" | 18" | Yes | Yes | No | Yes | Yes | No |
| Rectangular 54" x 18" x 30" | 30" | 54" | 30" | 54" | 36" | 18" | 12" | 18" | Yes | Yes | No | Yes | Yes | No |
| Rectangular 54" x 18" x 36" | 36" | 54" | 36" | 54" | 36" | 18" | 12" | 18" | Yes | Yes | No | Yes | Yes | No |
| Rectangular 54" x 18" x 42" | 42" | 54" | 42" | 54" | 36" | 18" | 12" | 18" | Yes | Yes | No | Yes | Yes | No |
| Rectangular 54" x 18" x 48" | 48" | 54" | 48" | 54" | 36" | 18" | 12" | 18" | Yes | Yes | No | Yes | Yes | No |
| Rectangular 54" x 18" x 54" | 54" | 54" | 54" | 54" | 36" | 18" | 12" | 18" | Yes | Yes | No | Yes | Yes | No |
| Rectangular 54" x 18" x 60" | 60" | 54" | 60" | 54" | 36" | 18" | 12" | 18" | Yes | Yes | No | Yes | Yes | No |
| Rectangular 54" x 24" x 18" | 18" | 54" | 18" | 54" | 36" | 24" | 16" | 24" | Yes | Yes | No | Yes | Yes | No |
| Rectangular 54" x 24" x 24" | 24" | 54" | 24" | 54" | 36" | 24" | 16" | 24" | Yes | Yes | No | Yes | Yes | No |
| Rectangular 54" x 24" x 30" | 30" | 54" | 30" | 54" | 36" | 24" | 16" | 24" | Yes | Yes | No | Yes | Yes | No |
| Rectangular 54" x 24" x 36" | 36" | 54" | 36" | 54" | 36" | 24" | 16" | 24" | Yes | Yes | No | Yes | Yes | No |
| Rectangular 54" x 24" x 42" | 42" | 54" | 42" | 54" | 36" | 24" | 16" | 24" | Yes | Yes | No | Yes | Yes | No |
| Rectangular 54" x 24" x 48" | 48" | 54" | 48" | 54" | 36" | 24" | 16" | 24" | Yes | Yes | No | Yes | Yes | No |
| Rectangular 54" x 24" x 54" | 54" | 54" | 54" | 54" | 36" | 24" | 16" | 24" | Yes | Yes | No | Yes | Yes | No |
| Rectangular 54" x 24" x 60" | 60" | 54" | 60" | 54" | 36" | 24" | 16" | 24" | Yes | Yes | No | Yes | Yes | No |
| Rectangular 54" x 30" x 18" | 18" | 54" | 18" | 54" | 36" | 30" | 20" | 30" | Yes | Yes | No | Yes | Yes | No |
| Rectangular 54" x 30" x 24" | 24" | 54" | 24" | 54" | 36" | 30" | 20" | 30" | Yes | Yes | No | Yes | Yes | No |
| Rectangular 54" x 30" x 30" | 30" | 54" | 30" | 54" | 36" | 30" | 20" | 30" | Yes | Yes | No | Yes | Yes | No |
| Rectangular 54" x 30" x 36" | 36" | 54" | 36" | 54" | 36" | 30" | 20" | 30" | Yes | Yes | No | Yes | Yes | No |
| Rectangular 54" x 30" x 42" | 42" | 54" | 42" | 54" | 36" | 30" | 20" | 30" | Yes | Yes | No | Yes | Yes | No |
| Rectangular 54" x 30" x 48" | 48" | 54" | 48" | 54" | 36" | 30" | 20" | 30" | Yes | Yes | No | Yes | Yes | No |
| Rectangular 54" x 30" x 54" | 54" | 54" | 54" | 54" | 36" | 30" | 20" | 30" | Yes | Yes | No | Yes | Yes | No |
| Rectangular 54" x 30" x 60" | 60" | 54" | 60" | 54" | 36" | 30" | 20" | 30" | Yes | Yes | No | Yes | Yes | No |
| Rectangular 54" x 36" x 18" | 18" | 54" | 18" | 54" | 36" | 36" | 24" | 36" | Yes | Yes | No | Yes | Yes | No |
| Rectangular 54" x 36" x 24" | 24" | 54" | 24" | 54" | 36" | 36" | 24" | 36" | Yes | Yes | No | Yes | Yes | No |
| Rectangular 54" x 36" x 30" | 30" | 54" | 30" | 54" | 36" | 36" | 24" | 36" | Yes | Yes | No | Yes | Yes | No |
| Rectangular 54" x 36" x 36" | 36" | 54" | 36" | 54" | 36" | 36" | 24" | 36" | Yes | Yes | No | Yes | Yes | No |
| Rectangular 54" x 36" x 42" | 42" | 54" | 42" | 54" | 36" | 36" | 24" | 36" | Yes | Yes | No | Yes | Yes | No |
| Rectangular 54" x 36" x 48" | 48" | 54" | 48" | 54" | 36" | 36" | 24" | 36" | Yes | Yes | No | Yes | Yes | No |
| Rectangular 54" x 36" x 54" | 54" | 54" | 54" | 54" | 36" | 36" | 24" | 36" | Yes | Yes | No | Yes | Yes | No |
| Rectangular 54" x 36" x 60" | 60" | 54" | 60" | 54" | 36" | 36" | 24" | 36" | Yes | Yes | No | Yes | Yes | No |
| Rectangular 54" x 42" x 18" | 18" | 54" | 18" | 54" | 36" | 42" | 28" | 42" | Yes | Yes | No | Yes | Yes | No |
| Rectangular 54" x 42" x 24" | 24" | 54" | 24" | 54" | 36" | 42" | 28" | 42" | Yes | Yes | No | Yes | Yes | No |
| Rectangular 54" x 42" x 30" | 30" | 54" | 30" | 54" | 36" | 42" | 28" | 42" | Yes | Yes | No | Yes | Yes | No |
| Rectangular 54" x 42" x 36" | 36" | 54" | 36" | 54" | 36" | 42" | 28" | 42" | Yes | Yes | No | Yes | Yes | No |
| Rectangular 54" x 42" x 42" | 42" | 54" | 42" | 54" | 36" | 42" | 28" | 42" | Yes | Yes | No | Yes | Yes | No |
| Rectangular 54" x 42" x 48" | 48" | 54" | 48" | 54" | 36" | 42" | 28" | 42" | Yes | Yes | No | Yes | Yes | No |
| Rectangular 54" x 42" x 54" | 54" | 54" | 54" | 54" | 36" | 42" | 28" | 42" | Yes | Yes | No | Yes | Yes | No |
| Rectangular 54" x 42" x 60" | 60" | 54" | 60" | 54" | 36" | 42" | 28" | 42" | Yes | Yes | No | Yes | Yes | No |
| Rectangular 54" x 48" x 18" | 18" | 54" | 18" | 54" | 36" | 48" | 32" | 48" | Yes | Yes | No | Yes | Yes | No |
| Rectangular 54" x 48" x 24" | 24" | 54" | 24" | 54" | 36" | 48" | 32" | 48" | Yes | Yes | No | Yes | Yes | No |
| Rectangular 54" x 48" x 30" | 30" | 54" | 30" | 54" | 36" | 48" | 32" | 48" | Yes | Yes | No | Yes | Yes | No |
| Rectangular 54" x 48" x 36" | 36" | 54" | 36" | 54" | 36" | 48" | 32" | 48" | Yes | Yes | No | Yes | Yes | No |
| Rectangular 54" x 48" x 42" | 42" | 54" | 42" | 54" | 36" | 48" | 32" | 48" | Yes | Yes | No | Yes | Yes | No |
| Rectangular 54" x 48" x 48" | 48" | 54" | 48" | 54" | 36" | 48" | 32" | 48" | Yes | Yes | No | Yes | Yes | No |
| Rectangular 54" x 48" x 54" | 54" | 54" | 54" | 54" | 36" | 48" | 32" | 48" | Yes | Yes | No | Yes | Yes | No |
| Rectangular 54" x 48" x 60" | 60" | 54" | 60" | 54" | 36" | 48" | 32" | 48" | Yes | Yes | No | Yes | Yes | No |
| Rectangular 54" x 60" x 18" | 18" | 54" | 18" | 54" | 36" | 60" | 40" | 60" | Yes | Yes | No | Yes | Yes | No |
| Rectangular 54" x 60" x 24" | 24" | 54" | 24" | 54" | 36" | 60" | 40" | 60" | Yes | Yes | No | Yes | Yes | No |
| Rectangular 54" x 60" x 30" | 30" | 54" | 30" | 54" | 36" | 60" | 40" | 60" | Yes | Yes | No | Yes | Yes | No |
| Rectangular 54" x 60" x 36" | 36" | 54" | 36" | 54" | 36" | 60" | 40" | 60" | Yes | Yes | No | Yes | Yes | No |
| Rectangular 54" x 60" x 42" | 42" | 54" | 42" | 54" | 36" | 60" | 40" | 60" | Yes | Yes | No | Yes | Yes | No |
| Rectangular 54" x 60" x 48" | 48" | 54" | 48" | 54" | 36" | 60" | 40" | 60" | Yes | Yes | No | Yes | Yes | No |
| Rectangular 54" x 60" x 54" | 54" | 54" | 54" | 54" | 36" | 60" | 40" | 60" | Yes | Yes | No | Yes | Yes | No |
| Rectangular 54" x 60" x 60" | 60" | 54" | 60" | 54" | 36" | 60" | 40" | 60" | Yes | Yes | No | Yes | Yes | No |
| Rectangular 54" x 66" x 18" | 18" | 54" | 18" | 54" | 36" | 66" | 44" | 66" | Yes | Yes | No | Yes | Yes | No |
| Rectangular 54" x 66" x 24" | 24" | 54" | 24" | 54" | 36" | 66" | 44" | 66" | Yes | Yes | No | Yes | Yes | No |
| Rectangular 54" x 66" x 30" | 30" | 54" | 30" | 54" | 36" | 66" | 44" | 66" | Yes | Yes | No | Yes | Yes | No |
| Rectangular 54" x 66" x 36" | 36" | 54" | 36" | 54" | 36" | 66" | 44" | 66" | Yes | Yes | No | Yes | Yes | No |
| Rectangular 54" x 66" x 42" | 42" | 54" | 42" | 54" | 36" | 66" | 44" | 66" | Yes | Yes | No | Yes | Yes | No |
| Rectangular 54" x 66" x 48" | 48" | 54" | 48" | 54" | 36" | 66" | 44" | 66" | Yes | Yes | No | Yes | Yes | No |
| Rectangular 54" x 66" x 54" | 54" | 54" | 54" | 54" | 36" | 66" | 44" | 66" | Yes | Yes | No | Yes | Yes | No |
| Rectangular 54" x 66" x 60" | 60" | 54" | 60" | 54" | 36" | 66" | 44" | 66" | Yes | Yes | No | Yes | Yes | No |
| Rectangular 54" x 72" x 18" | 18" | 54" | 18" | 54" | 36" | 72" | 48" | 72" | Yes | Yes | No | Yes | Yes | No |
| Rectangular 54" x 72" x 24" | 24" | 54" | 24" | 54" | 36" | 72" | 48" | 72" | Yes | Yes | No | Yes | Yes | No |
| Rectangular 54" x 72" x 30" | 30" | 54" | 30" | 54" | 36" | 72" | 48" | 72" | Yes | Yes | No | Yes | Yes | No |
| Rectangular 54" x 72" x 36" | 36" | 54" | 36" | 54" | 36" | 72" | 48" | 72" | Yes | Yes | No | Yes | Yes | No |
| Rectangular 54" x 72" x 42" | 42" | 54" | 42" | 54" | 36" | 72" | 48" | 72" | Yes | Yes | No | Yes | Yes | No |
| Rectangular 54" x 72" x 48" | 48" | 54" | 48" | 54" | 36" | 72" | 48" | 72" | Yes | Yes | No | Yes | Yes | No |
| Rectangular 54" x 72" x 54" | 54" | 54" | 54" | 54" | 36" | 72" | 48" | 72" | Yes | Yes | No | Yes | Yes | No |
| Rectangular 54" x 72" x 60" | 60" | 54" | 60" | 54" | 36" | 72" | 48" | 72" | Yes | Yes | No | Yes | Yes | No |
| Rectangular 60" x 12" x 18" | 18" | 60" | 18" | 60" | 40" | 12" | 8" | 12" | Yes | Yes | No | Yes | Yes | No |
| Rectangular 60" x 12" x 24" | 24" | 60" | 24" | 60" | 40" | 12" | 8" | 12" | Yes | Yes | No | Yes | Yes | No |
| Rectangular 60" x 12" x 30" | 30" | 60" | 30" | 60" | 40" | 12" | 8" | 12" | Yes | Yes | No | Yes | Yes | No |
| Rectangular 60" x 12" x 36" | 36" | 60" | 36" | 60" | 40" | 12" | 8" | 12" | Yes | Yes | No | Yes | Yes | No |
| Rectangular 60" x 15" x 18" | 18" | 60" | 18" | 60" | 40" | 15" | 10" | 15" | Yes | Yes | No | Yes | Yes | No |
| Rectangular 60" x 15" x 24" | 24" | 60" | 24" | 60" | 40" | 15" | 10" | 15" | Yes | Yes | No | Yes | Yes | No |
| Rectangular 60" x 15" x 30" | 30" | 60" | 30" | 60" | 40" | 15" | 10" | 15" | Yes | Yes | No | Yes | Yes | No |
| Rectangular 60" x 15" x 36" | 36" | 60" | 36" | 60" | 40" | 15" | 10" | 15" | Yes | Yes | No | Yes | Yes | No |
| Rectangular 60" x 15" x 42" | 42" | 60" | 42" | 60" | 40" | 15" | 10" | 15" | Yes | Yes | No | Yes | Yes | No |
| Rectangular 60" x 15" x 48" | 48" | 60" | 48" | 60" | 40" | 15" | 10" | 15" | Yes | Yes | No | Yes | Yes | No |
| Rectangular 60" x 15" x 54" | 54" | 60" | 54" | 60" | 40" | 15" | 10" | 15" | Yes | Yes | No | Yes | Yes | No |
| Rectangular 60" x 15" x 60" | 60" | 60" | 60" | 60" | 40" | 15" | 10" | 15" | Yes | Yes | No | Yes | Yes | No |
| Rectangular 60" x 18" x 18" | 18" | 60" | 18" | 60" | 40" | 18" | 12" | 18" | Yes | Yes | No | Yes | Yes | No |
| Rectangular 60" x 18" x 24" | 24" | 60" | 24" | 60" | 40" | 18" | 12" | 18" | Yes | Yes | No | Yes | Yes | No |
| Rectangular 60" x 18" x 30" | 30" | 60" | 30" | 60" | 40" | 18" | 12" | 18" | Yes | Yes | No | Yes | Yes | No |
| Rectangular 60" x 18" x 36" | 36" | 60" | 36" | 60" | 40" | 18" | 12" | 18" | Yes | Yes | No | Yes | Yes | No |
| Rectangular 60" x 18" x 42" | 42" | 60" | 42" | 60" | 40" | 18" | 12" | 18" | Yes | Yes | No | Yes | Yes | No |
| Rectangular 60" x 18" x 48" | 48" | 60" | 48" | 60" | 40" | 18" | 12" | 18" | Yes | Yes | No | Yes | Yes | No |
| Rectangular 60" x 18" x 54" | 54" | 60" | 54" | 60" | 40" | 18" | 12" | 18" | Yes | Yes | No | Yes | Yes | No |
| Rectangular 60" x 18" x 60" | 60" | 60" | 60" | 60" | 40" | 18" | 12" | 18" | Yes | Yes | No | Yes | Yes | No |
| Rectangular 60" x 24" x 18" | 18" | 60" | 18" | 60" | 40" | 24" | 16" | 24" | Yes | Yes | No | Yes | Yes | No |
| Rectangular 60" x 24" x 24" | 24" | 60" | 24" | 60" | 40" | 24" | 16" | 24" | Yes | Yes | No | Yes | Yes | No |
| Rectangular 60" x 24" x 30" | 30" | 60" | 30" | 60" | 40" | 24" | 16" | 24" | Yes | Yes | No | Yes | Yes | No |
| Rectangular 60" x 24" x 36" | 36" | 60" | 36" | 60" | 40" | 24" | 16" | 24" | Yes | Yes | No | Yes | Yes | No |
| Rectangular 60" x 24" x 42" | 42" | 60" | 42" | 60" | 40" | 24" | 16" | 24" | Yes | Yes | No | Yes | Yes | No |
| Rectangular 60" x 24" x 48" | 48" | 60" | 48" | 60" | 40" | 24" | 16" | 24" | Yes | Yes | No | Yes | Yes | No |
| Rectangular 60" x 24" x 54" | 54" | 60" | 54" | 60" | 40" | 24" | 16" | 24" | Yes | Yes | No | Yes | Yes | No |
| Rectangular 60" x 24" x 60" | 60" | 60" | 60" | 60" | 40" | 24" | 16" | 24" | Yes | Yes | No | Yes | Yes | No |
| Rectangular 60" x 30" x 18" | 18" | 60" | 18" | 60" | 40" | 30" | 20" | 30" | Yes | Yes | No | Yes | Yes | No |
| Rectangular 60" x 30" x 24" | 24" | 60" | 24" | 60" | 40" | 30" | 20" | 30" | Yes | Yes | No | Yes | Yes | No |
| Rectangular 60" x 30" x 30" | 30" | 60" | 30" | 60" | 40" | 30" | 20" | 30" | Yes | Yes | No | Yes | Yes | No |
| Rectangular 60" x 30" x 36" | 36" | 60" | 36" | 60" | 40" | 30" | 20" | 30" | Yes | Yes | No | Yes | Yes | No |
| Rectangular 60" x 30" x 42" | 42" | 60" | 42" | 60" | 40" | 30" | 20" | 30" | Yes | Yes | No | Yes | Yes | No |
| Rectangular 60" x 30" x 48" | 48" | 60" | 48" | 60" | 40" | 30" | 20" | 30" | Yes | Yes | No | Yes | Yes | No |
| Rectangular 60" x 30" x 54" | 54" | 60" | 54" | 60" | 40" | 30" | 20" | 30" | Yes | Yes | No | Yes | Yes | No |
| Rectangular 60" x 30" x 60" | 60" | 60" | 60" | 60" | 40" | 30" | 20" | 30" | Yes | Yes | No | Yes | Yes | No |
| Rectangular 60" x 36" x 18" | 18" | 60" | 18" | 60" | 40" | 36" | 24" | 36" | Yes | Yes | No | Yes | Yes | No |
| Rectangular 60" x 36" x 24" | 24" | 60" | 24" | 60" | 40" | 36" | 24" | 36" | Yes | Yes | No | Yes | Yes | No |
| Rectangular 60" x 36" x 30" | 30" | 60" | 30" | 60" | 40" | 36" | 24" | 36" | Yes | Yes | No | Yes | Yes | No |
| Rectangular 60" x 36" x 36" | 36" | 60" | 36" | 60" | 40" | 36" | 24" | 36" | Yes | Yes | No | Yes | Yes | No |
| Rectangular 60" x 36" x 42" | 42" | 60" | 42" | 60" | 40" | 36" | 24" | 36" | Yes | Yes | No | Yes | Yes | No |
| Rectangular 60" x 36" x 48" | 48" | 60" | 48" | 60" | 40" | 36" | 24" | 36" | Yes | Yes | No | Yes | Yes | No |
| Rectangular 60" x 36" x 54" | 54" | 60" | 54" | 60" | 40" | 36" | 24" | 36" | Yes | Yes | No | Yes | Yes | No |
| Rectangular 60" x 36" x 60" | 60" | 60" | 60" | 60" | 40" | 36" | 24" | 36" | Yes | Yes | No | Yes | Yes | No |
| Rectangular 60" x 42" x 18" | 18" | 60" | 18" | 60" | 40" | 42" | 28" | 42" | Yes | Yes | No | Yes | Yes | No |
| Rectangular 60" x 42" x 24" | 24" | 60" | 24" | 60" | 40" | 42" | 28" | 42" | Yes | Yes | No | Yes | Yes | No |
| Rectangular 60" x 42" x 30" | 30" | 60" | 30" | 60" | 40" | 42" | 28" | 42" | Yes | Yes | No | Yes | Yes | No |
| Rectangular 60" x 42" x 36" | 36" | 60" | 36" | 60" | 40" | 42" | 28" | 42" | Yes | Yes | No | Yes | Yes | No |
| Rectangular 60" x 42" x 42" | 42" | 60" | 42" | 60" | 40" | 42" | 28" | 42" | Yes | Yes | No | Yes | Yes | No |
| Rectangular 60" x 42" x 48" | 48" | 60" | 48" | 60" | 40" | 42" | 28" | 42" | Yes | Yes | No | Yes | Yes | No |
| Rectangular 60" x 42" x 54" | 54" | 60" | 54" | 60" | 40" | 42" | 28" | 42" | Yes | Yes | No | Yes | Yes | No |
| Rectangular 60" x 42" x 60" | 60" | 60" | 60" | 60" | 40" | 42" | 28" | 42" | Yes | Yes | No | Yes | Yes | No |
| Rectangular 60" x 48" x 18" | 18" | 60" | 18" | 60" | 40" | 48" | 32" | 48" | Yes | Yes | No | Yes | Yes | No |
| Rectangular 60" x 48" x 24" | 24" | 60" | 24" | 60" | 40" | 48" | 32" | 48" | Yes | Yes | No | Yes | Yes | No |
| Rectangular 60" x 48" x 30" | 30" | 60" | 30" | 60" | 40" | 48" | 32" | 48" | Yes | Yes | No | Yes | Yes | No |
| Rectangular 60" x 48" x 36" | 36" | 60" | 36" | 60" | 40" | 48" | 32" | 48" | Yes | Yes | No | Yes | Yes | No |
| Rectangular 60" x 48" x 42" | 42" | 60" | 42" | 60" | 40" | 48" | 32" | 48" | Yes | Yes | No | Yes | Yes | No |
| Rectangular 60" x 48" x 48" | 48" | 60" | 48" | 60" | 40" | 48" | 32" | 48" | Yes | Yes | No | Yes | Yes | No |
| Rectangular 60" x 48" x 54" | 54" | 60" | 54" | 60" | 40" | 48" | 32" | 48" | Yes | Yes | No | Yes | Yes | No |
| Rectangular 60" x 48" x 60" | 60" | 60" | 60" | 60" | 40" | 48" | 32" | 48" | Yes | Yes | No | Yes | Yes | No |
| Square 60" x 60" x 18" | 18" | 60" | 18" | 60" | 40" | 60" | 40" | 60" | No | Yes | Yes | Yes | No | Yes |
| Square 60" x 60" x 24" | 24" | 60" | 24" | 60" | 40" | 60" | 40" | 60" | No | Yes | Yes | Yes | No | Yes |
| Square 60" x 60" x 30" | 30" | 60" | 30" | 60" | 40" | 60" | 40" | 60" | No | Yes | Yes | Yes | No | Yes |
| Square 60" x 60" x 36" | 36" | 60" | 36" | 60" | 40" | 60" | 40" | 60" | No | Yes | Yes | Yes | No | Yes |
| Square 60" x 60" x 42" | 42" | 60" | 42" | 60" | 40" | 60" | 40" | 60" | No | Yes | Yes | Yes | No | Yes |
| Square 60" x 60" x 48" | 48" | 60" | 48" | 60" | 40" | 60" | 40" | 60" | No | Yes | Yes | Yes | No | Yes |
| Square 60" x 60" x 54" | 54" | 60" | 54" | 60" | 40" | 60" | 40" | 60" | No | Yes | Yes | Yes | No | Yes |
| Square 60" x 60" x 60" | 60" | 60" | 60" | 60" | 40" | 60" | 40" | 60" | No | Yes | Yes | Yes | No | Yes |
| Rectangular 60" x 66" x 18" | 18" | 60" | 18" | 60" | 40" | 66" | 44" | 66" | Yes | Yes | No | Yes | Yes | No |
| Rectangular 60" x 66" x 24" | 24" | 60" | 24" | 60" | 40" | 66" | 44" | 66" | Yes | Yes | No | Yes | Yes | No |
| Rectangular 60" x 66" x 30" | 30" | 60" | 30" | 60" | 40" | 66" | 44" | 66" | Yes | Yes | No | Yes | Yes | No |
| Rectangular 60" x 66" x 36" | 36" | 60" | 36" | 60" | 40" | 66" | 44" | 66" | Yes | Yes | No | Yes | Yes | No |
| Rectangular 60" x 66" x 42" | 42" | 60" | 42" | 60" | 40" | 66" | 44" | 66" | Yes | Yes | No | Yes | Yes | No |
| Rectangular 60" x 66" x 48" | 48" | 60" | 48" | 60" | 40" | 66" | 44" | 66" | Yes | Yes | No | Yes | Yes | No |
| Rectangular 60" x 66" x 54" | 54" | 60" | 54" | 60" | 40" | 66" | 44" | 66" | Yes | Yes | No | Yes | Yes | No |
| Rectangular 60" x 66" x 60" | 60" | 60" | 60" | 60" | 40" | 66" | 44" | 66" | Yes | Yes | No | Yes | Yes | No |
| Rectangular 60" x 72" x 18" | 18" | 60" | 18" | 60" | 40" | 72" | 48" | 72" | Yes | Yes | No | Yes | Yes | No |
| Rectangular 60" x 72" x 24" | 24" | 60" | 24" | 60" | 40" | 72" | 48" | 72" | Yes | Yes | No | Yes | Yes | No |
| Rectangular 60" x 72" x 30" | 30" | 60" | 30" | 60" | 40" | 72" | 48" | 72" | Yes | Yes | No | Yes | Yes | No |
| Rectangular 60" x 72" x 36" | 36" | 60" | 36" | 60" | 40" | 72" | 48" | 72" | Yes | Yes | No | Yes | Yes | No |
| Rectangular 60" x 72" x 42" | 42" | 60" | 42" | 60" | 40" | 72" | 48" | 72" | Yes | Yes | No | Yes | Yes | No |
| Rectangular 60" x 72" x 48" | 48" | 60" | 48" | 60" | 40" | 72" | 48" | 72" | Yes | Yes | No | Yes | Yes | No |
| Rectangular 60" x 72" x 54" | 54" | 60" | 54" | 60" | 40" | 72" | 48" | 72" | Yes | Yes | No | Yes | Yes | No |
| Rectangular 60" x 72" x 60" | 60" | 60" | 60" | 60" | 40" | 72" | 48" | 72" | Yes | Yes | No | Yes | Yes | No |
| Rectangular 66" x 12" x 18" | 18" | 66" | 18" | 66" | 44" | 12" | 8" | 12" | Yes | Yes | No | Yes | Yes | No |
| Rectangular 66" x 12" x 24" | 24" | 66" | 24" | 66" | 44" | 12" | 8" | 12" | Yes | Yes | No | Yes | Yes | No |
| Rectangular 66" x 12" x 30" | 30" | 66" | 30" | 66" | 44" | 12" | 8" | 12" | Yes | Yes | No | Yes | Yes | No |
| Rectangular 66" x 12" x 36" | 36" | 66" | 36" | 66" | 44" | 12" | 8" | 12" | Yes | Yes | No | Yes | Yes | No |
| Rectangular 66" x 15" x 18" | 18" | 66" | 18" | 66" | 44" | 15" | 10" | 15" | Yes | Yes | No | Yes | Yes | No |
| Rectangular 66" x 15" x 24" | 24" | 66" | 24" | 66" | 44" | 15" | 10" | 15" | Yes | Yes | No | Yes | Yes | No |
| Rectangular 66" x 15" x 30" | 30" | 66" | 30" | 66" | 44" | 15" | 10" | 15" | Yes | Yes | No | Yes | Yes | No |
| Rectangular 66" x 15" x 36" | 36" | 66" | 36" | 66" | 44" | 15" | 10" | 15" | Yes | Yes | No | Yes | Yes | No |
| Rectangular 66" x 15" x 42" | 42" | 66" | 42" | 66" | 44" | 15" | 10" | 15" | Yes | Yes | No | Yes | Yes | No |
| Rectangular 66" x 15" x 48" | 48" | 66" | 48" | 66" | 44" | 15" | 10" | 15" | Yes | Yes | No | Yes | Yes | No |
| Rectangular 66" x 15" x 54" | 54" | 66" | 54" | 66" | 44" | 15" | 10" | 15" | Yes | Yes | No | Yes | Yes | No |
| Rectangular 66" x 15" x 60" | 60" | 66" | 60" | 66" | 44" | 15" | 10" | 15" | Yes | Yes | No | Yes | Yes | No |
| Rectangular 66" x 18" x 18" | 18" | 66" | 18" | 66" | 44" | 18" | 12" | 18" | Yes | Yes | No | Yes | Yes | No |
| Rectangular 66" x 18" x 24" | 24" | 66" | 24" | 66" | 44" | 18" | 12" | 18" | Yes | Yes | No | Yes | Yes | No |
| Rectangular 66" x 18" x 30" | 30" | 66" | 30" | 66" | 44" | 18" | 12" | 18" | Yes | Yes | No | Yes | Yes | No |
| Rectangular 66" x 18" x 36" | 36" | 66" | 36" | 66" | 44" | 18" | 12" | 18" | Yes | Yes | No | Yes | Yes | No |
| Rectangular 66" x 18" x 42" | 42" | 66" | 42" | 66" | 44" | 18" | 12" | 18" | Yes | Yes | No | Yes | Yes | No |
| Rectangular 66" x 18" x 48" | 48" | 66" | 48" | 66" | 44" | 18" | 12" | 18" | Yes | Yes | No | Yes | Yes | No |
| Rectangular 66" x 18" x 54" | 54" | 66" | 54" | 66" | 44" | 18" | 12" | 18" | Yes | Yes | No | Yes | Yes | No |
| Rectangular 66" x 18" x 60" | 60" | 66" | 60" | 66" | 44" | 18" | 12" | 18" | Yes | Yes | No | Yes | Yes | No |
| Rectangular 66" x 24" x 18" | 18" | 66" | 18" | 66" | 44" | 24" | 16" | 24" | Yes | Yes | No | Yes | Yes | No |
| Rectangular 66" x 24" x 24" | 24" | 66" | 24" | 66" | 44" | 24" | 16" | 24" | Yes | Yes | No | Yes | Yes | No |
| Rectangular 66" x 24" x 30" | 30" | 66" | 30" | 66" | 44" | 24" | 16" | 24" | Yes | Yes | No | Yes | Yes | No |
| Rectangular 66" x 24" x 36" | 36" | 66" | 36" | 66" | 44" | 24" | 16" | 24" | Yes | Yes | No | Yes | Yes | No |
| Rectangular 66" x 24" x 42" | 42" | 66" | 42" | 66" | 44" | 24" | 16" | 24" | Yes | Yes | No | Yes | Yes | No |
| Rectangular 66" x 24" x 48" | 48" | 66" | 48" | 66" | 44" | 24" | 16" | 24" | Yes | Yes | No | Yes | Yes | No |
| Rectangular 66" x 24" x 54" | 54" | 66" | 54" | 66" | 44" | 24" | 16" | 24" | Yes | Yes | No | Yes | Yes | No |
| Rectangular 66" x 24" x 60" | 60" | 66" | 60" | 66" | 44" | 24" | 16" | 24" | Yes | Yes | No | Yes | Yes | No |
| Rectangular 66" x 30" x 18" | 18" | 66" | 18" | 66" | 44" | 30" | 20" | 30" | Yes | Yes | No | Yes | Yes | No |
| Rectangular 66" x 30" x 24" | 24" | 66" | 24" | 66" | 44" | 30" | 20" | 30" | Yes | Yes | No | Yes | Yes | No |
| Rectangular 66" x 30" x 30" | 30" | 66" | 30" | 66" | 44" | 30" | 20" | 30" | Yes | Yes | No | Yes | Yes | No |
| Rectangular 66" x 30" x 36" | 36" | 66" | 36" | 66" | 44" | 30" | 20" | 30" | Yes | Yes | No | Yes | Yes | No |
| Rectangular 66" x 30" x 42" | 42" | 66" | 42" | 66" | 44" | 30" | 20" | 30" | Yes | Yes | No | Yes | Yes | No |
| Rectangular 66" x 30" x 48" | 48" | 66" | 48" | 66" | 44" | 30" | 20" | 30" | Yes | Yes | No | Yes | Yes | No |
| Rectangular 66" x 30" x 54" | 54" | 66" | 54" | 66" | 44" | 30" | 20" | 30" | Yes | Yes | No | Yes | Yes | No |
| Rectangular 66" x 30" x 60" | 60" | 66" | 60" | 66" | 44" | 30" | 20" | 30" | Yes | Yes | No | Yes | Yes | No |
| Rectangular 66" x 36" x 18" | 18" | 66" | 18" | 66" | 44" | 36" | 24" | 36" | Yes | Yes | No | Yes | Yes | No |
| Rectangular 66" x 36" x 24" | 24" | 66" | 24" | 66" | 44" | 36" | 24" | 36" | Yes | Yes | No | Yes | Yes | No |
| Rectangular 66" x 36" x 30" | 30" | 66" | 30" | 66" | 44" | 36" | 24" | 36" | Yes | Yes | No | Yes | Yes | No |
| Rectangular 66" x 36" x 36" | 36" | 66" | 36" | 66" | 44" | 36" | 24" | 36" | Yes | Yes | No | Yes | Yes | No |
| Rectangular 66" x 36" x 42" | 42" | 66" | 42" | 66" | 44" | 36" | 24" | 36" | Yes | Yes | No | Yes | Yes | No |
| Rectangular 66" x 36" x 48" | 48" | 66" | 48" | 66" | 44" | 36" | 24" | 36" | Yes | Yes | No | Yes | Yes | No |
| Rectangular 66" x 36" x 54" | 54" | 66" | 54" | 66" | 44" | 36" | 24" | 36" | Yes | Yes | No | Yes | Yes | No |
| Rectangular 66" x 36" x 60" | 60" | 66" | 60" | 66" | 44" | 36" | 24" | 36" | Yes | Yes | No | Yes | Yes | No |
| Rectangular 66" x 42" x 18" | 18" | 66" | 18" | 66" | 44" | 42" | 28" | 42" | Yes | Yes | No | Yes | Yes | No |
| Rectangular 66" x 42" x 24" | 24" | 66" | 24" | 66" | 44" | 42" | 28" | 42" | Yes | Yes | No | Yes | Yes | No |
| Rectangular 66" x 42" x 30" | 30" | 66" | 30" | 66" | 44" | 42" | 28" | 42" | Yes | Yes | No | Yes | Yes | No |
| Rectangular 66" x 42" x 36" | 36" | 66" | 36" | 66" | 44" | 42" | 28" | 42" | Yes | Yes | No | Yes | Yes | No |
| Rectangular 66" x 42" x 42" | 42" | 66" | 42" | 66" | 44" | 42" | 28" | 42" | Yes | Yes | No | Yes | Yes | No |
| Rectangular 66" x 42" x 48" | 48" | 66" | 48" | 66" | 44" | 42" | 28" | 42" | Yes | Yes | No | Yes | Yes | No |
| Rectangular 66" x 42" x 54" | 54" | 66" | 54" | 66" | 44" | 42" | 28" | 42" | Yes | Yes | No | Yes | Yes | No |
| Rectangular 66" x 42" x 60" | 60" | 66" | 60" | 66" | 44" | 42" | 28" | 42" | Yes | Yes | No | Yes | Yes | No |
| Rectangular 66" x 48" x 18" | 18" | 66" | 18" | 66" | 44" | 48" | 32" | 48" | Yes | Yes | No | Yes | Yes | No |
| Rectangular 66" x 48" x 24" | 24" | 66" | 24" | 66" | 44" | 48" | 32" | 48" | Yes | Yes | No | Yes | Yes | No |
| Rectangular 66" x 48" x 30" | 30" | 66" | 30" | 66" | 44" | 48" | 32" | 48" | Yes | Yes | No | Yes | Yes | No |
| Rectangular 66" x 48" x 36" | 36" | 66" | 36" | 66" | 44" | 48" | 32" | 48" | Yes | Yes | No | Yes | Yes | No |
| Rectangular 66" x 48" x 42" | 42" | 66" | 42" | 66" | 44" | 48" | 32" | 48" | Yes | Yes | No | Yes | Yes | No |
| Rectangular 66" x 48" x 48" | 48" | 66" | 48" | 66" | 44" | 48" | 32" | 48" | Yes | Yes | No | Yes | Yes | No |
| Rectangular 66" x 48" x 54" | 54" | 66" | 54" | 66" | 44" | 48" | 32" | 48" | Yes | Yes | No | Yes | Yes | No |
| Rectangular 66" x 48" x 60" | 60" | 66" | 60" | 66" | 44" | 48" | 32" | 48" | Yes | Yes | No | Yes | Yes | No |
| Rectangular 66" x 60" x 18" | 18" | 66" | 18" | 66" | 44" | 60" | 40" | 60" | Yes | Yes | No | Yes | Yes | No |
| Rectangular 66" x 60" x 24" | 24" | 66" | 24" | 66" | 44" | 60" | 40" | 60" | Yes | Yes | No | Yes | Yes | No |
| Rectangular 66" x 60" x 30" | 30" | 66" | 30" | 66" | 44" | 60" | 40" | 60" | Yes | Yes | No | Yes | Yes | No |
| Rectangular 66" x 60" x 36" | 36" | 66" | 36" | 66" | 44" | 60" | 40" | 60" | Yes | Yes | No | Yes | Yes | No |
| Rectangular 66" x 60" x 42" | 42" | 66" | 42" | 66" | 44" | 60" | 40" | 60" | Yes | Yes | No | Yes | Yes | No |
| Rectangular 66" x 60" x 48" | 48" | 66" | 48" | 66" | 44" | 60" | 40" | 60" | Yes | Yes | No | Yes | Yes | No |
| Rectangular 66" x 60" x 54" | 54" | 66" | 54" | 66" | 44" | 60" | 40" | 60" | Yes | Yes | No | Yes | Yes | No |
| Rectangular 66" x 60" x 60" | 60" | 66" | 60" | 66" | 44" | 60" | 40" | 60" | Yes | Yes | No | Yes | Yes | No |
| Square 66" x 66" x 18" | 18" | 66" | 18" | 66" | 44" | 66" | 44" | 66" | No | Yes | Yes | Yes | No | Yes |
| Square 66" x 66" x 24" | 24" | 66" | 24" | 66" | 44" | 66" | 44" | 66" | No | Yes | Yes | Yes | No | Yes |
| Square 66" x 66" x 30" | 30" | 66" | 30" | 66" | 44" | 66" | 44" | 66" | No | Yes | Yes | Yes | No | Yes |
| Square 66" x 66" x 36" | 36" | 66" | 36" | 66" | 44" | 66" | 44" | 66" | No | Yes | Yes | Yes | No | Yes |
| Square 66" x 66" x 42" | 42" | 66" | 42" | 66" | 44" | 66" | 44" | 66" | No | Yes | Yes | Yes | No | Yes |
| Square 66" x 66" x 48" | 48" | 66" | 48" | 66" | 44" | 66" | 44" | 66" | No | Yes | Yes | Yes | No | Yes |
| Square 66" x 66" x 54" | 54" | 66" | 54" | 66" | 44" | 66" | 44" | 66" | No | Yes | Yes | Yes | No | Yes |
| Square 66" x 66" x 60" | 60" | 66" | 60" | 66" | 44" | 66" | 44" | 66" | No | Yes | Yes | Yes | No | Yes |
| Rectangular 66" x 72" x 18" | 18" | 66" | 18" | 66" | 44" | 72" | 48" | 72" | Yes | Yes | No | Yes | Yes | No |
| Rectangular 66" x 72" x 24" | 24" | 66" | 24" | 66" | 44" | 72" | 48" | 72" | Yes | Yes | No | Yes | Yes | No |
| Rectangular 66" x 72" x 30" | 30" | 66" | 30" | 66" | 44" | 72" | 48" | 72" | Yes | Yes | No | Yes | Yes | No |
| Rectangular 66" x 72" x 36" | 36" | 66" | 36" | 66" | 44" | 72" | 48" | 72" | Yes | Yes | No | Yes | Yes | No |
| Rectangular 66" x 72" x 42" | 42" | 66" | 42" | 66" | 44" | 72" | 48" | 72" | Yes | Yes | No | Yes | Yes | No |
| Rectangular 66" x 72" x 48" | 48" | 66" | 48" | 66" | 44" | 72" | 48" | 72" | Yes | Yes | No | Yes | Yes | No |
| Rectangular 66" x 72" x 54" | 54" | 66" | 54" | 66" | 44" | 72" | 48" | 72" | Yes | Yes | No | Yes | Yes | No |
| Rectangular 66" x 72" x 60" | 60" | 66" | 60" | 66" | 44" | 72" | 48" | 72" | Yes | Yes | No | Yes | Yes | No |
| Rectangular 72" x 12" x 18" | 18" | 72" | 18" | 72" | 48" | 12" | 8" | 12" | Yes | Yes | No | Yes | Yes | No |
| Rectangular 72" x 12" x 24" | 24" | 72" | 24" | 72" | 48" | 12" | 8" | 12" | Yes | Yes | No | Yes | Yes | No |
| Rectangular 72" x 12" x 30" | 30" | 72" | 30" | 72" | 48" | 12" | 8" | 12" | Yes | Yes | No | Yes | Yes | No |
| Rectangular 72" x 12" x 36" | 36" | 72" | 36" | 72" | 48" | 12" | 8" | 12" | Yes | Yes | No | Yes | Yes | No |
| Rectangular 72" x 15" x 18" | 18" | 72" | 18" | 72" | 48" | 15" | 10" | 15" | Yes | Yes | No | Yes | Yes | No |
| Rectangular 72" x 15" x 24" | 24" | 72" | 24" | 72" | 48" | 15" | 10" | 15" | Yes | Yes | No | Yes | Yes | No |
| Rectangular 72" x 15" x 30" | 30" | 72" | 30" | 72" | 48" | 15" | 10" | 15" | Yes | Yes | No | Yes | Yes | No |
| Rectangular 72" x 15" x 36" | 36" | 72" | 36" | 72" | 48" | 15" | 10" | 15" | Yes | Yes | No | Yes | Yes | No |
| Rectangular 72" x 15" x 42" | 42" | 72" | 42" | 72" | 48" | 15" | 10" | 15" | Yes | Yes | No | Yes | Yes | No |
| Rectangular 72" x 15" x 48" | 48" | 72" | 48" | 72" | 48" | 15" | 10" | 15" | Yes | Yes | No | Yes | Yes | No |
| Rectangular 72" x 15" x 54" | 54" | 72" | 54" | 72" | 48" | 15" | 10" | 15" | Yes | Yes | No | Yes | Yes | No |
| Rectangular 72" x 15" x 60" | 60" | 72" | 60" | 72" | 48" | 15" | 10" | 15" | Yes | Yes | No | Yes | Yes | No |
| Rectangular 72" x 18" x 18" | 18" | 72" | 18" | 72" | 48" | 18" | 12" | 18" | Yes | Yes | No | Yes | Yes | No |
| Rectangular 72" x 18" x 24" | 24" | 72" | 24" | 72" | 48" | 18" | 12" | 18" | Yes | Yes | No | Yes | Yes | No |
| Rectangular 72" x 18" x 30" | 30" | 72" | 30" | 72" | 48" | 18" | 12" | 18" | Yes | Yes | No | Yes | Yes | No |
| Rectangular 72" x 18" x 36" | 36" | 72" | 36" | 72" | 48" | 18" | 12" | 18" | Yes | Yes | No | Yes | Yes | No |
| Rectangular 72" x 18" x 42" | 42" | 72" | 42" | 72" | 48" | 18" | 12" | 18" | Yes | Yes | No | Yes | Yes | No |
| Rectangular 72" x 18" x 48" | 48" | 72" | 48" | 72" | 48" | 18" | 12" | 18" | Yes | Yes | No | Yes | Yes | No |
| Rectangular 72" x 18" x 54" | 54" | 72" | 54" | 72" | 48" | 18" | 12" | 18" | Yes | Yes | No | Yes | Yes | No |
| Rectangular 72" x 18" x 60" | 60" | 72" | 60" | 72" | 48" | 18" | 12" | 18" | Yes | Yes | No | Yes | Yes | No |
| Rectangular 72" x 24" x 18" | 18" | 72" | 18" | 72" | 48" | 24" | 16" | 24" | Yes | Yes | No | Yes | Yes | No |
| Rectangular 72" x 24" x 24" | 24" | 72" | 24" | 72" | 48" | 24" | 16" | 24" | Yes | Yes | No | Yes | Yes | No |
| Rectangular 72" x 24" x 30" | 30" | 72" | 30" | 72" | 48" | 24" | 16" | 24" | Yes | Yes | No | Yes | Yes | No |
| Rectangular 72" x 24" x 36" | 36" | 72" | 36" | 72" | 48" | 24" | 16" | 24" | Yes | Yes | No | Yes | Yes | No |
| Rectangular 72" x 24" x 42" | 42" | 72" | 42" | 72" | 48" | 24" | 16" | 24" | Yes | Yes | No | Yes | Yes | No |
| Rectangular 72" x 24" x 48" | 48" | 72" | 48" | 72" | 48" | 24" | 16" | 24" | Yes | Yes | No | Yes | Yes | No |
| Rectangular 72" x 24" x 54" | 54" | 72" | 54" | 72" | 48" | 24" | 16" | 24" | Yes | Yes | No | Yes | Yes | No |
| Rectangular 72" x 24" x 60" | 60" | 72" | 60" | 72" | 48" | 24" | 16" | 24" | Yes | Yes | No | Yes | Yes | No |
| Rectangular 72" x 30" x 18" | 18" | 72" | 18" | 72" | 48" | 30" | 20" | 30" | Yes | Yes | No | Yes | Yes | No |
| Rectangular 72" x 30" x 24" | 24" | 72" | 24" | 72" | 48" | 30" | 20" | 30" | Yes | Yes | No | Yes | Yes | No |
| Rectangular 72" x 30" x 30" | 30" | 72" | 30" | 72" | 48" | 30" | 20" | 30" | Yes | Yes | No | Yes | Yes | No |
| Rectangular 72" x 30" x 36" | 36" | 72" | 36" | 72" | 48" | 30" | 20" | 30" | Yes | Yes | No | Yes | Yes | No |
| Rectangular 72" x 30" x 42" | 42" | 72" | 42" | 72" | 48" | 30" | 20" | 30" | Yes | Yes | No | Yes | Yes | No |
| Rectangular 72" x 30" x 48" | 48" | 72" | 48" | 72" | 48" | 30" | 20" | 30" | Yes | Yes | No | Yes | Yes | No |
| Rectangular 72" x 30" x 54" | 54" | 72" | 54" | 72" | 48" | 30" | 20" | 30" | Yes | Yes | No | Yes | Yes | No |
| Rectangular 72" x 30" x 60" | 60" | 72" | 60" | 72" | 48" | 30" | 20" | 30" | Yes | Yes | No | Yes | Yes | No |
| Rectangular 72" x 36" x 18" | 18" | 72" | 18" | 72" | 48" | 36" | 24" | 36" | Yes | Yes | No | Yes | Yes | No |
| Rectangular 72" x 36" x 24" | 24" | 72" | 24" | 72" | 48" | 36" | 24" | 36" | Yes | Yes | No | Yes | Yes | No |
| Rectangular 72" x 36" x 30" | 30" | 72" | 30" | 72" | 48" | 36" | 24" | 36" | Yes | Yes | No | Yes | Yes | No |
| Rectangular 72" x 36" x 36" | 36" | 72" | 36" | 72" | 48" | 36" | 24" | 36" | Yes | Yes | No | Yes | Yes | No |
| Rectangular 72" x 36" x 42" | 42" | 72" | 42" | 72" | 48" | 36" | 24" | 36" | Yes | Yes | No | Yes | Yes | No |
| Rectangular 72" x 36" x 48" | 48" | 72" | 48" | 72" | 48" | 36" | 24" | 36" | Yes | Yes | No | Yes | Yes | No |
| Rectangular 72" x 36" x 54" | 54" | 72" | 54" | 72" | 48" | 36" | 24" | 36" | Yes | Yes | No | Yes | Yes | No |
| Rectangular 72" x 36" x 60" | 60" | 72" | 60" | 72" | 48" | 36" | 24" | 36" | Yes | Yes | No | Yes | Yes | No |
| Rectangular 72" x 42" x 18" | 18" | 72" | 18" | 72" | 48" | 42" | 28" | 42" | Yes | Yes | No | Yes | Yes | No |
| Rectangular 72" x 42" x 24" | 24" | 72" | 24" | 72" | 48" | 42" | 28" | 42" | Yes | Yes | No | Yes | Yes | No |
| Rectangular 72" x 42" x 30" | 30" | 72" | 30" | 72" | 48" | 42" | 28" | 42" | Yes | Yes | No | Yes | Yes | No |
| Rectangular 72" x 42" x 36" | 36" | 72" | 36" | 72" | 48" | 42" | 28" | 42" | Yes | Yes | No | Yes | Yes | No |
| Rectangular 72" x 42" x 42" | 42" | 72" | 42" | 72" | 48" | 42" | 28" | 42" | Yes | Yes | No | Yes | Yes | No |
| Rectangular 72" x 42" x 48" | 48" | 72" | 48" | 72" | 48" | 42" | 28" | 42" | Yes | Yes | No | Yes | Yes | No |
| Rectangular 72" x 42" x 54" | 54" | 72" | 54" | 72" | 48" | 42" | 28" | 42" | Yes | Yes | No | Yes | Yes | No |
| Rectangular 72" x 42" x 60" | 60" | 72" | 60" | 72" | 48" | 42" | 28" | 42" | Yes | Yes | No | Yes | Yes | No |
| Rectangular 72" x 48" x 18" | 18" | 72" | 18" | 72" | 48" | 48" | 32" | 48" | Yes | Yes | No | Yes | Yes | No |
| Rectangular 72" x 48" x 24" | 24" | 72" | 24" | 72" | 48" | 48" | 32" | 48" | Yes | Yes | No | Yes | Yes | No |
| Rectangular 72" x 48" x 30" | 30" | 72" | 30" | 72" | 48" | 48" | 32" | 48" | Yes | Yes | No | Yes | Yes | No |
| Rectangular 72" x 48" x 36" | 36" | 72" | 36" | 72" | 48" | 48" | 32" | 48" | Yes | Yes | No | Yes | Yes | No |
| Rectangular 72" x 48" x 42" | 42" | 72" | 42" | 72" | 48" | 48" | 32" | 48" | Yes | Yes | No | Yes | Yes | No |
| Rectangular 72" x 48" x 48" | 48" | 72" | 48" | 72" | 48" | 48" | 32" | 48" | Yes | Yes | No | Yes | Yes | No |
| Rectangular 72" x 48" x 54" | 54" | 72" | 54" | 72" | 48" | 48" | 32" | 48" | Yes | Yes | No | Yes | Yes | No |
| Rectangular 72" x 48" x 60" | 60" | 72" | 60" | 72" | 48" | 48" | 32" | 48" | Yes | Yes | No | Yes | Yes | No |
| Rectangular 72" x 60" x 18" | 18" | 72" | 18" | 72" | 48" | 60" | 40" | 60" | Yes | Yes | No | Yes | Yes | No |
| Rectangular 72" x 60" x 24" | 24" | 72" | 24" | 72" | 48" | 60" | 40" | 60" | Yes | Yes | No | Yes | Yes | No |
| Rectangular 72" x 60" x 30" | 30" | 72" | 30" | 72" | 48" | 60" | 40" | 60" | Yes | Yes | No | Yes | Yes | No |
| Rectangular 72" x 60" x 36" | 36" | 72" | 36" | 72" | 48" | 60" | 40" | 60" | Yes | Yes | No | Yes | Yes | No |
| Rectangular 72" x 60" x 42" | 42" | 72" | 42" | 72" | 48" | 60" | 40" | 60" | Yes | Yes | No | Yes | Yes | No |
| Rectangular 72" x 60" x 48" | 48" | 72" | 48" | 72" | 48" | 60" | 40" | 60" | Yes | Yes | No | Yes | Yes | No |
| Rectangular 72" x 60" x 54" | 54" | 72" | 54" | 72" | 48" | 60" | 40" | 60" | Yes | Yes | No | Yes | Yes | No |
| Rectangular 72" x 60" x 60" | 60" | 72" | 60" | 72" | 48" | 60" | 40" | 60" | Yes | Yes | No | Yes | Yes | No |
| Rectangular 72" x 66" x 18" | 18" | 72" | 18" | 72" | 48" | 66" | 44" | 66" | Yes | Yes | No | Yes | Yes | No |
| Rectangular 72" x 66" x 24" | 24" | 72" | 24" | 72" | 48" | 66" | 44" | 66" | Yes | Yes | No | Yes | Yes | No |
| Rectangular 72" x 66" x 30" | 30" | 72" | 30" | 72" | 48" | 66" | 44" | 66" | Yes | Yes | No | Yes | Yes | No |
| Rectangular 72" x 66" x 36" | 36" | 72" | 36" | 72" | 48" | 66" | 44" | 66" | Yes | Yes | No | Yes | Yes | No |
| Rectangular 72" x 66" x 42" | 42" | 72" | 42" | 72" | 48" | 66" | 44" | 66" | Yes | Yes | No | Yes | Yes | No |
| Rectangular 72" x 66" x 48" | 48" | 72" | 48" | 72" | 48" | 66" | 44" | 66" | Yes | Yes | No | Yes | Yes | No |
| Rectangular 72" x 66" x 54" | 54" | 72" | 54" | 72" | 48" | 66" | 44" | 66" | Yes | Yes | No | Yes | Yes | No |
| Rectangular 72" x 66" x 60" | 60" | 72" | 60" | 72" | 48" | 66" | 44" | 66" | Yes | Yes | No | Yes | Yes | No |
| Square 72" x 72" x 18" | 18" | 72" | 18" | 72" | 48" | 72" | 48" | 72" | No | Yes | Yes | Yes | No | Yes |
| Square 72" x 72" x 24" | 24" | 72" | 24" | 72" | 48" | 72" | 48" | 72" | No | Yes | Yes | Yes | No | Yes |
| Square 72" x 72" x 30" | 30" | 72" | 30" | 72" | 48" | 72" | 48" | 72" | No | Yes | Yes | Yes | No | Yes |
| Square 72" x 72" x 36" | 36" | 72" | 36" | 72" | 48" | 72" | 48" | 72" | No | Yes | Yes | Yes | No | Yes |
| Square 72" x 72" x 42" | 42" | 72" | 42" | 72" | 48" | 72" | 48" | 72" | No | Yes | Yes | Yes | No | Yes |
| Square 72" x 72" x 48" | 48" | 72" | 48" | 72" | 48" | 72" | 48" | 72" | No | Yes | Yes | Yes | No | Yes |
| Square 72" x 72" x 54" | 54" | 72" | 54" | 72" | 48" | 72" | 48" | 72" | No | Yes | Yes | Yes | No | Yes |
| Square 72" x 72" x 60" | 60" | 72" | 60" | 72" | 48" | 72" | 48" | 72" | No | Yes | Yes | Yes | No | Yes |
| Rectangular 78" x 12" x 18" | 18" | 78" | 18" | 78" | 52" | 12" | 8" | 12" | Yes | Yes | No | Yes | Yes | No |
| Rectangular 78" x 12" x 24" | 24" | 78" | 24" | 78" | 52" | 12" | 8" | 12" | Yes | Yes | No | Yes | Yes | No |
| Rectangular 78" x 12" x 30" | 30" | 78" | 30" | 78" | 52" | 12" | 8" | 12" | Yes | Yes | No | Yes | Yes | No |
| Rectangular 78" x 12" x 36" | 36" | 78" | 36" | 78" | 52" | 12" | 8" | 12" | Yes | Yes | No | Yes | Yes | No |
| Rectangular 78" x 15" x 18" | 18" | 78" | 18" | 78" | 52" | 15" | 10" | 15" | Yes | Yes | No | Yes | Yes | No |
| Rectangular 78" x 15" x 24" | 24" | 78" | 24" | 78" | 52" | 15" | 10" | 15" | Yes | Yes | No | Yes | Yes | No |
| Rectangular 78" x 15" x 30" | 30" | 78" | 30" | 78" | 52" | 15" | 10" | 15" | Yes | Yes | No | Yes | Yes | No |
| Rectangular 78" x 15" x 36" | 36" | 78" | 36" | 78" | 52" | 15" | 10" | 15" | Yes | Yes | No | Yes | Yes | No |
| Rectangular 78" x 15" x 42" | 42" | 78" | 42" | 78" | 52" | 15" | 10" | 15" | Yes | Yes | No | Yes | Yes | No |
| Rectangular 78" x 15" x 48" | 48" | 78" | 48" | 78" | 52" | 15" | 10" | 15" | Yes | Yes | No | Yes | Yes | No |
| Rectangular 78" x 15" x 54" | 54" | 78" | 54" | 78" | 52" | 15" | 10" | 15" | Yes | Yes | No | Yes | Yes | No |
| Rectangular 78" x 15" x 60" | 60" | 78" | 60" | 78" | 52" | 15" | 10" | 15" | Yes | Yes | No | Yes | Yes | No |
| Rectangular 78" x 18" x 18" | 18" | 78" | 18" | 78" | 52" | 18" | 12" | 18" | Yes | Yes | No | Yes | Yes | No |
| Rectangular 78" x 18" x 24" | 24" | 78" | 24" | 78" | 52" | 18" | 12" | 18" | Yes | Yes | No | Yes | Yes | No |
| Rectangular 78" x 18" x 30" | 30" | 78" | 30" | 78" | 52" | 18" | 12" | 18" | Yes | Yes | No | Yes | Yes | No |
| Rectangular 78" x 18" x 36" | 36" | 78" | 36" | 78" | 52" | 18" | 12" | 18" | Yes | Yes | No | Yes | Yes | No |
| Rectangular 78" x 18" x 42" | 42" | 78" | 42" | 78" | 52" | 18" | 12" | 18" | Yes | Yes | No | Yes | Yes | No |
| Rectangular 78" x 18" x 48" | 48" | 78" | 48" | 78" | 52" | 18" | 12" | 18" | Yes | Yes | No | Yes | Yes | No |
| Rectangular 78" x 18" x 54" | 54" | 78" | 54" | 78" | 52" | 18" | 12" | 18" | Yes | Yes | No | Yes | Yes | No |
| Rectangular 78" x 18" x 60" | 60" | 78" | 60" | 78" | 52" | 18" | 12" | 18" | Yes | Yes | No | Yes | Yes | No |
| Rectangular 78" x 24" x 18" | 18" | 78" | 18" | 78" | 52" | 24" | 16" | 24" | Yes | Yes | No | Yes | Yes | No |
| Rectangular 78" x 24" x 24" | 24" | 78" | 24" | 78" | 52" | 24" | 16" | 24" | Yes | Yes | No | Yes | Yes | No |
| Rectangular 78" x 24" x 30" | 30" | 78" | 30" | 78" | 52" | 24" | 16" | 24" | Yes | Yes | No | Yes | Yes | No |
| Rectangular 78" x 24" x 36" | 36" | 78" | 36" | 78" | 52" | 24" | 16" | 24" | Yes | Yes | No | Yes | Yes | No |
| Rectangular 78" x 24" x 42" | 42" | 78" | 42" | 78" | 52" | 24" | 16" | 24" | Yes | Yes | No | Yes | Yes | No |
| Rectangular 78" x 24" x 48" | 48" | 78" | 48" | 78" | 52" | 24" | 16" | 24" | Yes | Yes | No | Yes | Yes | No |
| Rectangular 78" x 24" x 54" | 54" | 78" | 54" | 78" | 52" | 24" | 16" | 24" | Yes | Yes | No | Yes | Yes | No |
| Rectangular 78" x 24" x 60" | 60" | 78" | 60" | 78" | 52" | 24" | 16" | 24" | Yes | Yes | No | Yes | Yes | No |
| Rectangular 78" x 30" x 18" | 18" | 78" | 18" | 78" | 52" | 30" | 20" | 30" | Yes | Yes | No | Yes | Yes | No |
| Rectangular 78" x 30" x 24" | 24" | 78" | 24" | 78" | 52" | 30" | 20" | 30" | Yes | Yes | No | Yes | Yes | No |
| Rectangular 78" x 30" x 30" | 30" | 78" | 30" | 78" | 52" | 30" | 20" | 30" | Yes | Yes | No | Yes | Yes | No |
| Rectangular 78" x 30" x 36" | 36" | 78" | 36" | 78" | 52" | 30" | 20" | 30" | Yes | Yes | No | Yes | Yes | No |
| Rectangular 78" x 30" x 42" | 42" | 78" | 42" | 78" | 52" | 30" | 20" | 30" | Yes | Yes | No | Yes | Yes | No |
| Rectangular 78" x 30" x 48" | 48" | 78" | 48" | 78" | 52" | 30" | 20" | 30" | Yes | Yes | No | Yes | Yes | No |
| Rectangular 78" x 30" x 54" | 54" | 78" | 54" | 78" | 52" | 30" | 20" | 30" | Yes | Yes | No | Yes | Yes | No |
| Rectangular 78" x 30" x 60" | 60" | 78" | 60" | 78" | 52" | 30" | 20" | 30" | Yes | Yes | No | Yes | Yes | No |
| Rectangular 78" x 36" x 18" | 18" | 78" | 18" | 78" | 52" | 36" | 24" | 36" | Yes | Yes | No | Yes | Yes | No |
| Rectangular 78" x 36" x 24" | 24" | 78" | 24" | 78" | 52" | 36" | 24" | 36" | Yes | Yes | No | Yes | Yes | No |
| Rectangular 78" x 36" x 30" | 30" | 78" | 30" | 78" | 52" | 36" | 24" | 36" | Yes | Yes | No | Yes | Yes | No |
| Rectangular 78" x 36" x 36" | 36" | 78" | 36" | 78" | 52" | 36" | 24" | 36" | Yes | Yes | No | Yes | Yes | No |
| Rectangular 78" x 36" x 42" | 42" | 78" | 42" | 78" | 52" | 36" | 24" | 36" | Yes | Yes | No | Yes | Yes | No |
| Rectangular 78" x 36" x 48" | 48" | 78" | 48" | 78" | 52" | 36" | 24" | 36" | Yes | Yes | No | Yes | Yes | No |
| Rectangular 78" x 36" x 54" | 54" | 78" | 54" | 78" | 52" | 36" | 24" | 36" | Yes | Yes | No | Yes | Yes | No |
| Rectangular 78" x 36" x 60" | 60" | 78" | 60" | 78" | 52" | 36" | 24" | 36" | Yes | Yes | No | Yes | Yes | No |
| Rectangular 78" x 42" x 18" | 18" | 78" | 18" | 78" | 52" | 42" | 28" | 42" | Yes | Yes | No | Yes | Yes | No |
| Rectangular 78" x 42" x 24" | 24" | 78" | 24" | 78" | 52" | 42" | 28" | 42" | Yes | Yes | No | Yes | Yes | No |
| Rectangular 78" x 42" x 30" | 30" | 78" | 30" | 78" | 52" | 42" | 28" | 42" | Yes | Yes | No | Yes | Yes | No |
| Rectangular 78" x 42" x 36" | 36" | 78" | 36" | 78" | 52" | 42" | 28" | 42" | Yes | Yes | No | Yes | Yes | No |
| Rectangular 78" x 42" x 42" | 42" | 78" | 42" | 78" | 52" | 42" | 28" | 42" | Yes | Yes | No | Yes | Yes | No |
| Rectangular 78" x 42" x 48" | 48" | 78" | 48" | 78" | 52" | 42" | 28" | 42" | Yes | Yes | No | Yes | Yes | No |
| Rectangular 78" x 42" x 54" | 54" | 78" | 54" | 78" | 52" | 42" | 28" | 42" | Yes | Yes | No | Yes | Yes | No |
| Rectangular 78" x 42" x 60" | 60" | 78" | 60" | 78" | 52" | 42" | 28" | 42" | Yes | Yes | No | Yes | Yes | No |
| Rectangular 78" x 48" x 18" | 18" | 78" | 18" | 78" | 52" | 48" | 32" | 48" | Yes | Yes | No | Yes | Yes | No |
| Rectangular 78" x 48" x 24" | 24" | 78" | 24" | 78" | 52" | 48" | 32" | 48" | Yes | Yes | No | Yes | Yes | No |
| Rectangular 78" x 48" x 30" | 30" | 78" | 30" | 78" | 52" | 48" | 32" | 48" | Yes | Yes | No | Yes | Yes | No |
| Rectangular 78" x 48" x 36" | 36" | 78" | 36" | 78" | 52" | 48" | 32" | 48" | Yes | Yes | No | Yes | Yes | No |
| Rectangular 78" x 48" x 42" | 42" | 78" | 42" | 78" | 52" | 48" | 32" | 48" | Yes | Yes | No | Yes | Yes | No |
| Rectangular 78" x 48" x 48" | 48" | 78" | 48" | 78" | 52" | 48" | 32" | 48" | Yes | Yes | No | Yes | Yes | No |
| Rectangular 78" x 48" x 54" | 54" | 78" | 54" | 78" | 52" | 48" | 32" | 48" | Yes | Yes | No | Yes | Yes | No |
| Rectangular 78" x 48" x 60" | 60" | 78" | 60" | 78" | 52" | 48" | 32" | 48" | Yes | Yes | No | Yes | Yes | No |
| Rectangular 78" x 60" x 18" | 18" | 78" | 18" | 78" | 52" | 60" | 40" | 60" | Yes | Yes | No | Yes | Yes | No |
| Rectangular 78" x 60" x 24" | 24" | 78" | 24" | 78" | 52" | 60" | 40" | 60" | Yes | Yes | No | Yes | Yes | No |
| Rectangular 78" x 60" x 30" | 30" | 78" | 30" | 78" | 52" | 60" | 40" | 60" | Yes | Yes | No | Yes | Yes | No |
| Rectangular 78" x 60" x 36" | 36" | 78" | 36" | 78" | 52" | 60" | 40" | 60" | Yes | Yes | No | Yes | Yes | No |
| Rectangular 78" x 60" x 42" | 42" | 78" | 42" | 78" | 52" | 60" | 40" | 60" | Yes | Yes | No | Yes | Yes | No |
| Rectangular 78" x 60" x 48" | 48" | 78" | 48" | 78" | 52" | 60" | 40" | 60" | Yes | Yes | No | Yes | Yes | No |
| Rectangular 78" x 60" x 54" | 54" | 78" | 54" | 78" | 52" | 60" | 40" | 60" | Yes | Yes | No | Yes | Yes | No |
| Rectangular 78" x 60" x 60" | 60" | 78" | 60" | 78" | 52" | 60" | 40" | 60" | Yes | Yes | No | Yes | Yes | No |
| Rectangular 78" x 66" x 18" | 18" | 78" | 18" | 78" | 52" | 66" | 44" | 66" | Yes | Yes | No | Yes | Yes | No |
| Rectangular 78" x 66" x 24" | 24" | 78" | 24" | 78" | 52" | 66" | 44" | 66" | Yes | Yes | No | Yes | Yes | No |
| Rectangular 78" x 66" x 30" | 30" | 78" | 30" | 78" | 52" | 66" | 44" | 66" | Yes | Yes | No | Yes | Yes | No |
| Rectangular 78" x 66" x 36" | 36" | 78" | 36" | 78" | 52" | 66" | 44" | 66" | Yes | Yes | No | Yes | Yes | No |
| Rectangular 78" x 66" x 42" | 42" | 78" | 42" | 78" | 52" | 66" | 44" | 66" | Yes | Yes | No | Yes | Yes | No |
| Rectangular 78" x 66" x 48" | 48" | 78" | 48" | 78" | 52" | 66" | 44" | 66" | Yes | Yes | No | Yes | Yes | No |
| Rectangular 78" x 66" x 54" | 54" | 78" | 54" | 78" | 52" | 66" | 44" | 66" | Yes | Yes | No | Yes | Yes | No |
| Rectangular 78" x 66" x 60" | 60" | 78" | 60" | 78" | 52" | 66" | 44" | 66" | Yes | Yes | No | Yes | Yes | No |
| Rectangular 78" x 72" x 18" | 18" | 78" | 18" | 78" | 52" | 72" | 48" | 72" | Yes | Yes | No | Yes | Yes | No |
| Rectangular 78" x 72" x 24" | 24" | 78" | 24" | 78" | 52" | 72" | 48" | 72" | Yes | Yes | No | Yes | Yes | No |
| Rectangular 78" x 72" x 30" | 30" | 78" | 30" | 78" | 52" | 72" | 48" | 72" | Yes | Yes | No | Yes | Yes | No |
| Rectangular 78" x 72" x 36" | 36" | 78" | 36" | 78" | 52" | 72" | 48" | 72" | Yes | Yes | No | Yes | Yes | No |
| Rectangular 78" x 72" x 42" | 42" | 78" | 42" | 78" | 52" | 72" | 48" | 72" | Yes | Yes | No | Yes | Yes | No |
| Rectangular 78" x 72" x 48" | 48" | 78" | 48" | 78" | 52" | 72" | 48" | 72" | Yes | Yes | No | Yes | Yes | No |
| Rectangular 78" x 72" x 54" | 54" | 78" | 54" | 78" | 52" | 72" | 48" | 72" | Yes | Yes | No | Yes | Yes | No |
| Rectangular 78" x 72" x 60" | 60" | 78" | 60" | 78" | 52" | 72" | 48" | 72" | Yes | Yes | No | Yes | Yes | No |
| Rectangular 84" x 12" x 18" | 18" | 84" | 18" | 84" | 56" | 12" | 8" | 12" | Yes | Yes | No | Yes | Yes | No |
| Rectangular 84" x 12" x 24" | 24" | 84" | 24" | 84" | 56" | 12" | 8" | 12" | Yes | Yes | No | Yes | Yes | No |
| Rectangular 84" x 12" x 30" | 30" | 84" | 30" | 84" | 56" | 12" | 8" | 12" | Yes | Yes | No | Yes | Yes | No |
| Rectangular 84" x 12" x 36" | 36" | 84" | 36" | 84" | 56" | 12" | 8" | 12" | Yes | Yes | No | Yes | Yes | No |
| Rectangular 84" x 15" x 18" | 18" | 84" | 18" | 84" | 56" | 15" | 10" | 15" | Yes | Yes | No | Yes | Yes | No |
| Rectangular 84" x 15" x 24" | 24" | 84" | 24" | 84" | 56" | 15" | 10" | 15" | Yes | Yes | No | Yes | Yes | No |
| Rectangular 84" x 15" x 30" | 30" | 84" | 30" | 84" | 56" | 15" | 10" | 15" | Yes | Yes | No | Yes | Yes | No |
| Rectangular 84" x 15" x 36" | 36" | 84" | 36" | 84" | 56" | 15" | 10" | 15" | Yes | Yes | No | Yes | Yes | No |
| Rectangular 84" x 15" x 42" | 42" | 84" | 42" | 84" | 56" | 15" | 10" | 15" | Yes | Yes | No | Yes | Yes | No |
| Rectangular 84" x 15" x 48" | 48" | 84" | 48" | 84" | 56" | 15" | 10" | 15" | Yes | Yes | No | Yes | Yes | No |
| Rectangular 84" x 15" x 54" | 54" | 84" | 54" | 84" | 56" | 15" | 10" | 15" | Yes | Yes | No | Yes | Yes | No |
| Rectangular 84" x 15" x 60" | 60" | 84" | 60" | 84" | 56" | 15" | 10" | 15" | Yes | Yes | No | Yes | Yes | No |
| Rectangular 84" x 18" x 18" | 18" | 84" | 18" | 84" | 56" | 18" | 12" | 18" | Yes | Yes | No | Yes | Yes | No |
| Rectangular 84" x 18" x 24" | 24" | 84" | 24" | 84" | 56" | 18" | 12" | 18" | Yes | Yes | No | Yes | Yes | No |
| Rectangular 84" x 18" x 30" | 30" | 84" | 30" | 84" | 56" | 18" | 12" | 18" | Yes | Yes | No | Yes | Yes | No |
| Rectangular 84" x 18" x 36" | 36" | 84" | 36" | 84" | 56" | 18" | 12" | 18" | Yes | Yes | No | Yes | Yes | No |
| Rectangular 84" x 18" x 42" | 42" | 84" | 42" | 84" | 56" | 18" | 12" | 18" | Yes | Yes | No | Yes | Yes | No |
| Rectangular 84" x 18" x 48" | 48" | 84" | 48" | 84" | 56" | 18" | 12" | 18" | Yes | Yes | No | Yes | Yes | No |
| Rectangular 84" x 18" x 54" | 54" | 84" | 54" | 84" | 56" | 18" | 12" | 18" | Yes | Yes | No | Yes | Yes | No |
| Rectangular 84" x 18" x 60" | 60" | 84" | 60" | 84" | 56" | 18" | 12" | 18" | Yes | Yes | No | Yes | Yes | No |
| Rectangular 84" x 24" x 18" | 18" | 84" | 18" | 84" | 56" | 24" | 16" | 24" | Yes | Yes | No | Yes | Yes | No |
| Rectangular 84" x 24" x 24" | 24" | 84" | 24" | 84" | 56" | 24" | 16" | 24" | Yes | Yes | No | Yes | Yes | No |
| Rectangular 84" x 24" x 30" | 30" | 84" | 30" | 84" | 56" | 24" | 16" | 24" | Yes | Yes | No | Yes | Yes | No |
| Rectangular 84" x 24" x 36" | 36" | 84" | 36" | 84" | 56" | 24" | 16" | 24" | Yes | Yes | No | Yes | Yes | No |
| Rectangular 84" x 24" x 42" | 42" | 84" | 42" | 84" | 56" | 24" | 16" | 24" | Yes | Yes | No | Yes | Yes | No |
| Rectangular 84" x 24" x 48" | 48" | 84" | 48" | 84" | 56" | 24" | 16" | 24" | Yes | Yes | No | Yes | Yes | No |
| Rectangular 84" x 24" x 54" | 54" | 84" | 54" | 84" | 56" | 24" | 16" | 24" | Yes | Yes | No | Yes | Yes | No |
| Rectangular 84" x 24" x 60" | 60" | 84" | 60" | 84" | 56" | 24" | 16" | 24" | Yes | Yes | No | Yes | Yes | No |
| Rectangular 84" x 30" x 18" | 18" | 84" | 18" | 84" | 56" | 30" | 20" | 30" | Yes | Yes | No | Yes | Yes | No |
| Rectangular 84" x 30" x 24" | 24" | 84" | 24" | 84" | 56" | 30" | 20" | 30" | Yes | Yes | No | Yes | Yes | No |
| Rectangular 84" x 30" x 30" | 30" | 84" | 30" | 84" | 56" | 30" | 20" | 30" | Yes | Yes | No | Yes | Yes | No |
| Rectangular 84" x 30" x 36" | 36" | 84" | 36" | 84" | 56" | 30" | 20" | 30" | Yes | Yes | No | Yes | Yes | No |
| Rectangular 84" x 30" x 42" | 42" | 84" | 42" | 84" | 56" | 30" | 20" | 30" | Yes | Yes | No | Yes | Yes | No |
| Rectangular 84" x 30" x 48" | 48" | 84" | 48" | 84" | 56" | 30" | 20" | 30" | Yes | Yes | No | Yes | Yes | No |
| Rectangular 84" x 30" x 54" | 54" | 84" | 54" | 84" | 56" | 30" | 20" | 30" | Yes | Yes | No | Yes | Yes | No |
| Rectangular 84" x 30" x 60" | 60" | 84" | 60" | 84" | 56" | 30" | 20" | 30" | Yes | Yes | No | Yes | Yes | No |
| Rectangular 84" x 36" x 18" | 18" | 84" | 18" | 84" | 56" | 36" | 24" | 36" | Yes | Yes | No | Yes | Yes | No |
| Rectangular 84" x 36" x 24" | 24" | 84" | 24" | 84" | 56" | 36" | 24" | 36" | Yes | Yes | No | Yes | Yes | No |
| Rectangular 84" x 36" x 30" | 30" | 84" | 30" | 84" | 56" | 36" | 24" | 36" | Yes | Yes | No | Yes | Yes | No |
| Rectangular 84" x 36" x 36" | 36" | 84" | 36" | 84" | 56" | 36" | 24" | 36" | Yes | Yes | No | Yes | Yes | No |
| Rectangular 84" x 36" x 42" | 42" | 84" | 42" | 84" | 56" | 36" | 24" | 36" | Yes | Yes | No | Yes | Yes | No |
| Rectangular 84" x 36" x 48" | 48" | 84" | 48" | 84" | 56" | 36" | 24" | 36" | Yes | Yes | No | Yes | Yes | No |
| Rectangular 84" x 36" x 54" | 54" | 84" | 54" | 84" | 56" | 36" | 24" | 36" | Yes | Yes | No | Yes | Yes | No |
| Rectangular 84" x 36" x 60" | 60" | 84" | 60" | 84" | 56" | 36" | 24" | 36" | Yes | Yes | No | Yes | Yes | No |
| Rectangular 84" x 42" x 18" | 18" | 84" | 18" | 84" | 56" | 42" | 28" | 42" | Yes | Yes | No | Yes | Yes | No |
| Rectangular 84" x 42" x 24" | 24" | 84" | 24" | 84" | 56" | 42" | 28" | 42" | Yes | Yes | No | Yes | Yes | No |
| Rectangular 84" x 42" x 30" | 30" | 84" | 30" | 84" | 56" | 42" | 28" | 42" | Yes | Yes | No | Yes | Yes | No |
| Rectangular 84" x 42" x 36" | 36" | 84" | 36" | 84" | 56" | 42" | 28" | 42" | Yes | Yes | No | Yes | Yes | No |
| Rectangular 84" x 42" x 42" | 42" | 84" | 42" | 84" | 56" | 42" | 28" | 42" | Yes | Yes | No | Yes | Yes | No |
| Rectangular 84" x 42" x 48" | 48" | 84" | 48" | 84" | 56" | 42" | 28" | 42" | Yes | Yes | No | Yes | Yes | No |
| Rectangular 84" x 42" x 54" | 54" | 84" | 54" | 84" | 56" | 42" | 28" | 42" | Yes | Yes | No | Yes | Yes | No |
| Rectangular 84" x 42" x 60" | 60" | 84" | 60" | 84" | 56" | 42" | 28" | 42" | Yes | Yes | No | Yes | Yes | No |
| Rectangular 84" x 48" x 18" | 18" | 84" | 18" | 84" | 56" | 48" | 32" | 48" | Yes | Yes | No | Yes | Yes | No |
| Rectangular 84" x 48" x 24" | 24" | 84" | 24" | 84" | 56" | 48" | 32" | 48" | Yes | Yes | No | Yes | Yes | No |
| Rectangular 84" x 48" x 30" | 30" | 84" | 30" | 84" | 56" | 48" | 32" | 48" | Yes | Yes | No | Yes | Yes | No |
| Rectangular 84" x 48" x 36" | 36" | 84" | 36" | 84" | 56" | 48" | 32" | 48" | Yes | Yes | No | Yes | Yes | No |
| Rectangular 84" x 48" x 42" | 42" | 84" | 42" | 84" | 56" | 48" | 32" | 48" | Yes | Yes | No | Yes | Yes | No |
| Rectangular 84" x 48" x 48" | 48" | 84" | 48" | 84" | 56" | 48" | 32" | 48" | Yes | Yes | No | Yes | Yes | No |
| Rectangular 84" x 48" x 54" | 54" | 84" | 54" | 84" | 56" | 48" | 32" | 48" | Yes | Yes | No | Yes | Yes | No |
| Rectangular 84" x 48" x 60" | 60" | 84" | 60" | 84" | 56" | 48" | 32" | 48" | Yes | Yes | No | Yes | Yes | No |
| Rectangular 84" x 60" x 18" | 18" | 84" | 18" | 84" | 56" | 60" | 40" | 60" | Yes | Yes | No | Yes | Yes | No |
| Rectangular 84" x 60" x 24" | 24" | 84" | 24" | 84" | 56" | 60" | 40" | 60" | Yes | Yes | No | Yes | Yes | No |
| Rectangular 84" x 60" x 30" | 30" | 84" | 30" | 84" | 56" | 60" | 40" | 60" | Yes | Yes | No | Yes | Yes | No |
| Rectangular 84" x 60" x 36" | 36" | 84" | 36" | 84" | 56" | 60" | 40" | 60" | Yes | Yes | No | Yes | Yes | No |
| Rectangular 84" x 60" x 42" | 42" | 84" | 42" | 84" | 56" | 60" | 40" | 60" | Yes | Yes | No | Yes | Yes | No |
| Rectangular 84" x 60" x 48" | 48" | 84" | 48" | 84" | 56" | 60" | 40" | 60" | Yes | Yes | No | Yes | Yes | No |
| Rectangular 84" x 60" x 54" | 54" | 84" | 54" | 84" | 56" | 60" | 40" | 60" | Yes | Yes | No | Yes | Yes | No |
| Rectangular 84" x 60" x 60" | 60" | 84" | 60" | 84" | 56" | 60" | 40" | 60" | Yes | Yes | No | Yes | Yes | No |
| Rectangular 84" x 66" x 18" | 18" | 84" | 18" | 84" | 56" | 66" | 44" | 66" | Yes | Yes | No | Yes | Yes | No |
| Rectangular 84" x 66" x 24" | 24" | 84" | 24" | 84" | 56" | 66" | 44" | 66" | Yes | Yes | No | Yes | Yes | No |
| Rectangular 84" x 66" x 30" | 30" | 84" | 30" | 84" | 56" | 66" | 44" | 66" | Yes | Yes | No | Yes | Yes | No |
| Rectangular 84" x 66" x 36" | 36" | 84" | 36" | 84" | 56" | 66" | 44" | 66" | Yes | Yes | No | Yes | Yes | No |
| Rectangular 84" x 66" x 42" | 42" | 84" | 42" | 84" | 56" | 66" | 44" | 66" | Yes | Yes | No | Yes | Yes | No |
| Rectangular 84" x 66" x 48" | 48" | 84" | 48" | 84" | 56" | 66" | 44" | 66" | Yes | Yes | No | Yes | Yes | No |
| Rectangular 84" x 66" x 54" | 54" | 84" | 54" | 84" | 56" | 66" | 44" | 66" | Yes | Yes | No | Yes | Yes | No |
| Rectangular 84" x 66" x 60" | 60" | 84" | 60" | 84" | 56" | 66" | 44" | 66" | Yes | Yes | No | Yes | Yes | No |
| Rectangular 84" x 72" x 18" | 18" | 84" | 18" | 84" | 56" | 72" | 48" | 72" | Yes | Yes | No | Yes | Yes | No |
| Rectangular 84" x 72" x 24" | 24" | 84" | 24" | 84" | 56" | 72" | 48" | 72" | Yes | Yes | No | Yes | Yes | No |
| Rectangular 84" x 72" x 30" | 30" | 84" | 30" | 84" | 56" | 72" | 48" | 72" | Yes | Yes | No | Yes | Yes | No |
| Rectangular 84" x 72" x 36" | 36" | 84" | 36" | 84" | 56" | 72" | 48" | 72" | Yes | Yes | No | Yes | Yes | No |
| Rectangular 84" x 72" x 42" | 42" | 84" | 42" | 84" | 56" | 72" | 48" | 72" | Yes | Yes | No | Yes | Yes | No |
| Rectangular 84" x 72" x 48" | 48" | 84" | 48" | 84" | 56" | 72" | 48" | 72" | Yes | Yes | No | Yes | Yes | No |
| Rectangular 84" x 72" x 54" | 54" | 84" | 54" | 84" | 56" | 72" | 48" | 72" | Yes | Yes | No | Yes | Yes | No |
| Rectangular 84" x 72" x 60" | 60" | 84" | 60" | 84" | 56" | 72" | 48" | 72" | Yes | Yes | No | Yes | Yes | No |
| Rectangular 90" x 12" x 18" | 18" | 90" | 18" | 90" | 60" | 12" | 8" | 12" | Yes | Yes | No | Yes | Yes | No |
| Rectangular 90" x 12" x 24" | 24" | 90" | 24" | 90" | 60" | 12" | 8" | 12" | Yes | Yes | No | Yes | Yes | No |
| Rectangular 90" x 12" x 30" | 30" | 90" | 30" | 90" | 60" | 12" | 8" | 12" | Yes | Yes | No | Yes | Yes | No |
| Rectangular 90" x 12" x 36" | 36" | 90" | 36" | 90" | 60" | 12" | 8" | 12" | Yes | Yes | No | Yes | Yes | No |
| Rectangular 90" x 15" x 18" | 18" | 90" | 18" | 90" | 60" | 15" | 10" | 15" | Yes | Yes | No | Yes | Yes | No |
| Rectangular 90" x 15" x 24" | 24" | 90" | 24" | 90" | 60" | 15" | 10" | 15" | Yes | Yes | No | Yes | Yes | No |
| Rectangular 90" x 15" x 30" | 30" | 90" | 30" | 90" | 60" | 15" | 10" | 15" | Yes | Yes | No | Yes | Yes | No |
| Rectangular 90" x 15" x 36" | 36" | 90" | 36" | 90" | 60" | 15" | 10" | 15" | Yes | Yes | No | Yes | Yes | No |
| Rectangular 90" x 15" x 42" | 42" | 90" | 42" | 90" | 60" | 15" | 10" | 15" | Yes | Yes | No | Yes | Yes | No |
| Rectangular 90" x 15" x 48" | 48" | 90" | 48" | 90" | 60" | 15" | 10" | 15" | Yes | Yes | No | Yes | Yes | No |
| Rectangular 90" x 15" x 54" | 54" | 90" | 54" | 90" | 60" | 15" | 10" | 15" | Yes | Yes | No | Yes | Yes | No |
| Rectangular 90" x 15" x 60" | 60" | 90" | 60" | 90" | 60" | 15" | 10" | 15" | Yes | Yes | No | Yes | Yes | No |
| Rectangular 90" x 18" x 18" | 18" | 90" | 18" | 90" | 60" | 18" | 12" | 18" | Yes | Yes | No | Yes | Yes | No |
| Rectangular 90" x 18" x 24" | 24" | 90" | 24" | 90" | 60" | 18" | 12" | 18" | Yes | Yes | No | Yes | Yes | No |
| Rectangular 90" x 18" x 30" | 30" | 90" | 30" | 90" | 60" | 18" | 12" | 18" | Yes | Yes | No | Yes | Yes | No |
| Rectangular 90" x 18" x 36" | 36" | 90" | 36" | 90" | 60" | 18" | 12" | 18" | Yes | Yes | No | Yes | Yes | No |
| Rectangular 90" x 18" x 42" | 42" | 90" | 42" | 90" | 60" | 18" | 12" | 18" | Yes | Yes | No | Yes | Yes | No |
| Rectangular 90" x 18" x 48" | 48" | 90" | 48" | 90" | 60" | 18" | 12" | 18" | Yes | Yes | No | Yes | Yes | No |
| Rectangular 90" x 18" x 54" | 54" | 90" | 54" | 90" | 60" | 18" | 12" | 18" | Yes | Yes | No | Yes | Yes | No |
| Rectangular 90" x 18" x 60" | 60" | 90" | 60" | 90" | 60" | 18" | 12" | 18" | Yes | Yes | No | Yes | Yes | No |
| Rectangular 90" x 24" x 18" | 18" | 90" | 18" | 90" | 60" | 24" | 16" | 24" | Yes | Yes | No | Yes | Yes | No |
| Rectangular 90" x 24" x 24" | 24" | 90" | 24" | 90" | 60" | 24" | 16" | 24" | Yes | Yes | No | Yes | Yes | No |
| Rectangular 90" x 24" x 30" | 30" | 90" | 30" | 90" | 60" | 24" | 16" | 24" | Yes | Yes | No | Yes | Yes | No |
| Rectangular 90" x 24" x 36" | 36" | 90" | 36" | 90" | 60" | 24" | 16" | 24" | Yes | Yes | No | Yes | Yes | No |
| Rectangular 90" x 24" x 42" | 42" | 90" | 42" | 90" | 60" | 24" | 16" | 24" | Yes | Yes | No | Yes | Yes | No |
| Rectangular 90" x 24" x 48" | 48" | 90" | 48" | 90" | 60" | 24" | 16" | 24" | Yes | Yes | No | Yes | Yes | No |
| Rectangular 90" x 24" x 54" | 54" | 90" | 54" | 90" | 60" | 24" | 16" | 24" | Yes | Yes | No | Yes | Yes | No |
| Rectangular 90" x 24" x 60" | 60" | 90" | 60" | 90" | 60" | 24" | 16" | 24" | Yes | Yes | No | Yes | Yes | No |
| Rectangular 90" x 30" x 18" | 18" | 90" | 18" | 90" | 60" | 30" | 20" | 30" | Yes | Yes | No | Yes | Yes | No |
| Rectangular 90" x 30" x 24" | 24" | 90" | 24" | 90" | 60" | 30" | 20" | 30" | Yes | Yes | No | Yes | Yes | No |
| Rectangular 90" x 30" x 30" | 30" | 90" | 30" | 90" | 60" | 30" | 20" | 30" | Yes | Yes | No | Yes | Yes | No |
| Rectangular 90" x 30" x 36" | 36" | 90" | 36" | 90" | 60" | 30" | 20" | 30" | Yes | Yes | No | Yes | Yes | No |
| Rectangular 90" x 30" x 42" | 42" | 90" | 42" | 90" | 60" | 30" | 20" | 30" | Yes | Yes | No | Yes | Yes | No |
| Rectangular 90" x 30" x 48" | 48" | 90" | 48" | 90" | 60" | 30" | 20" | 30" | Yes | Yes | No | Yes | Yes | No |
| Rectangular 90" x 30" x 54" | 54" | 90" | 54" | 90" | 60" | 30" | 20" | 30" | Yes | Yes | No | Yes | Yes | No |
| Rectangular 90" x 30" x 60" | 60" | 90" | 60" | 90" | 60" | 30" | 20" | 30" | Yes | Yes | No | Yes | Yes | No |
| Rectangular 90" x 36" x 18" | 18" | 90" | 18" | 90" | 60" | 36" | 24" | 36" | Yes | Yes | No | Yes | Yes | No |
| Rectangular 90" x 36" x 24" | 24" | 90" | 24" | 90" | 60" | 36" | 24" | 36" | Yes | Yes | No | Yes | Yes | No |
| Rectangular 90" x 36" x 30" | 30" | 90" | 30" | 90" | 60" | 36" | 24" | 36" | Yes | Yes | No | Yes | Yes | No |
| Rectangular 90" x 36" x 36" | 36" | 90" | 36" | 90" | 60" | 36" | 24" | 36" | Yes | Yes | No | Yes | Yes | No |
| Rectangular 90" x 36" x 42" | 42" | 90" | 42" | 90" | 60" | 36" | 24" | 36" | Yes | Yes | No | Yes | Yes | No |
| Rectangular 90" x 36" x 48" | 48" | 90" | 48" | 90" | 60" | 36" | 24" | 36" | Yes | Yes | No | Yes | Yes | No |
| Rectangular 90" x 36" x 54" | 54" | 90" | 54" | 90" | 60" | 36" | 24" | 36" | Yes | Yes | No | Yes | Yes | No |
| Rectangular 90" x 36" x 60" | 60" | 90" | 60" | 90" | 60" | 36" | 24" | 36" | Yes | Yes | No | Yes | Yes | No |
| Rectangular 90" x 42" x 18" | 18" | 90" | 18" | 90" | 60" | 42" | 28" | 42" | Yes | Yes | No | Yes | Yes | No |
| Rectangular 90" x 42" x 24" | 24" | 90" | 24" | 90" | 60" | 42" | 28" | 42" | Yes | Yes | No | Yes | Yes | No |
| Rectangular 90" x 42" x 30" | 30" | 90" | 30" | 90" | 60" | 42" | 28" | 42" | Yes | Yes | No | Yes | Yes | No |
| Rectangular 90" x 42" x 36" | 36" | 90" | 36" | 90" | 60" | 42" | 28" | 42" | Yes | Yes | No | Yes | Yes | No |
| Rectangular 90" x 42" x 42" | 42" | 90" | 42" | 90" | 60" | 42" | 28" | 42" | Yes | Yes | No | Yes | Yes | No |
| Rectangular 90" x 42" x 48" | 48" | 90" | 48" | 90" | 60" | 42" | 28" | 42" | Yes | Yes | No | Yes | Yes | No |
| Rectangular 90" x 42" x 54" | 54" | 90" | 54" | 90" | 60" | 42" | 28" | 42" | Yes | Yes | No | Yes | Yes | No |
| Rectangular 90" x 42" x 60" | 60" | 90" | 60" | 90" | 60" | 42" | 28" | 42" | Yes | Yes | No | Yes | Yes | No |
| Rectangular 90" x 48" x 18" | 18" | 90" | 18" | 90" | 60" | 48" | 32" | 48" | Yes | Yes | No | Yes | Yes | No |
| Rectangular 90" x 48" x 24" | 24" | 90" | 24" | 90" | 60" | 48" | 32" | 48" | Yes | Yes | No | Yes | Yes | No |
| Rectangular 90" x 48" x 30" | 30" | 90" | 30" | 90" | 60" | 48" | 32" | 48" | Yes | Yes | No | Yes | Yes | No |
| Rectangular 90" x 48" x 36" | 36" | 90" | 36" | 90" | 60" | 48" | 32" | 48" | Yes | Yes | No | Yes | Yes | No |
| Rectangular 90" x 48" x 42" | 42" | 90" | 42" | 90" | 60" | 48" | 32" | 48" | Yes | Yes | No | Yes | Yes | No |
| Rectangular 90" x 48" x 48" | 48" | 90" | 48" | 90" | 60" | 48" | 32" | 48" | Yes | Yes | No | Yes | Yes | No |
| Rectangular 90" x 48" x 54" | 54" | 90" | 54" | 90" | 60" | 48" | 32" | 48" | Yes | Yes | No | Yes | Yes | No |
| Rectangular 90" x 48" x 60" | 60" | 90" | 60" | 90" | 60" | 48" | 32" | 48" | Yes | Yes | No | Yes | Yes | No |
| Rectangular 90" x 60" x 18" | 18" | 90" | 18" | 90" | 60" | 60" | 40" | 60" | Yes | Yes | No | Yes | Yes | No |
| Rectangular 90" x 60" x 24" | 24" | 90" | 24" | 90" | 60" | 60" | 40" | 60" | Yes | Yes | No | Yes | Yes | No |
| Rectangular 90" x 60" x 30" | 30" | 90" | 30" | 90" | 60" | 60" | 40" | 60" | Yes | Yes | No | Yes | Yes | No |
| Rectangular 90" x 60" x 36" | 36" | 90" | 36" | 90" | 60" | 60" | 40" | 60" | Yes | Yes | No | Yes | Yes | No |
| Rectangular 90" x 60" x 42" | 42" | 90" | 42" | 90" | 60" | 60" | 40" | 60" | Yes | Yes | No | Yes | Yes | No |
| Rectangular 90" x 60" x 48" | 48" | 90" | 48" | 90" | 60" | 60" | 40" | 60" | Yes | Yes | No | Yes | Yes | No |
| Rectangular 90" x 60" x 54" | 54" | 90" | 54" | 90" | 60" | 60" | 40" | 60" | Yes | Yes | No | Yes | Yes | No |
| Rectangular 90" x 60" x 60" | 60" | 90" | 60" | 90" | 60" | 60" | 40" | 60" | Yes | Yes | No | Yes | Yes | No |
| Rectangular 90" x 66" x 18" | 18" | 90" | 18" | 90" | 60" | 66" | 44" | 66" | Yes | Yes | No | Yes | Yes | No |
| Rectangular 90" x 66" x 24" | 24" | 90" | 24" | 90" | 60" | 66" | 44" | 66" | Yes | Yes | No | Yes | Yes | No |
| Rectangular 90" x 66" x 30" | 30" | 90" | 30" | 90" | 60" | 66" | 44" | 66" | Yes | Yes | No | Yes | Yes | No |
| Rectangular 90" x 66" x 36" | 36" | 90" | 36" | 90" | 60" | 66" | 44" | 66" | Yes | Yes | No | Yes | Yes | No |
| Rectangular 90" x 66" x 42" | 42" | 90" | 42" | 90" | 60" | 66" | 44" | 66" | Yes | Yes | No | Yes | Yes | No |
| Rectangular 90" x 66" x 48" | 48" | 90" | 48" | 90" | 60" | 66" | 44" | 66" | Yes | Yes | No | Yes | Yes | No |
| Rectangular 90" x 66" x 54" | 54" | 90" | 54" | 90" | 60" | 66" | 44" | 66" | Yes | Yes | No | Yes | Yes | No |
| Rectangular 90" x 66" x 60" | 60" | 90" | 60" | 90" | 60" | 66" | 44" | 66" | Yes | Yes | No | Yes | Yes | No |
| Rectangular 90" x 72" x 18" | 18" | 90" | 18" | 90" | 60" | 72" | 48" | 72" | Yes | Yes | No | Yes | Yes | No |
| Rectangular 90" x 72" x 24" | 24" | 90" | 24" | 90" | 60" | 72" | 48" | 72" | Yes | Yes | No | Yes | Yes | No |
| Rectangular 90" x 72" x 30" | 30" | 90" | 30" | 90" | 60" | 72" | 48" | 72" | Yes | Yes | No | Yes | Yes | No |
| Rectangular 90" x 72" x 36" | 36" | 90" | 36" | 90" | 60" | 72" | 48" | 72" | Yes | Yes | No | Yes | Yes | No |
| Rectangular 90" x 72" x 42" | 42" | 90" | 42" | 90" | 60" | 72" | 48" | 72" | Yes | Yes | No | Yes | Yes | No |
| Rectangular 90" x 72" x 48" | 48" | 90" | 48" | 90" | 60" | 72" | 48" | 72" | Yes | Yes | No | Yes | Yes | No |
| Rectangular 90" x 72" x 54" | 54" | 90" | 54" | 90" | 60" | 72" | 48" | 72" | Yes | Yes | No | Yes | Yes | No |
| Rectangular 90" x 72" x 60" | 60" | 90" | 60" | 90" | 60" | 72" | 48" | 72" | Yes | Yes | No | Yes | Yes | No |
| Rectangular 96" x 12" x 18" | 18" | 96" | 18" | 96" | 64" | 12" | 8" | 12" | Yes | Yes | No | Yes | Yes | No |
| Rectangular 96" x 12" x 24" | 24" | 96" | 24" | 96" | 64" | 12" | 8" | 12" | Yes | Yes | No | Yes | Yes | No |
| Rectangular 96" x 12" x 30" | 30" | 96" | 30" | 96" | 64" | 12" | 8" | 12" | Yes | Yes | No | Yes | Yes | No |
| Rectangular 96" x 12" x 36" | 36" | 96" | 36" | 96" | 64" | 12" | 8" | 12" | Yes | Yes | No | Yes | Yes | No |
| Rectangular 96" x 15" x 18" | 18" | 96" | 18" | 96" | 64" | 15" | 10" | 15" | Yes | Yes | No | Yes | Yes | No |
| Rectangular 96" x 15" x 24" | 24" | 96" | 24" | 96" | 64" | 15" | 10" | 15" | Yes | Yes | No | Yes | Yes | No |
| Rectangular 96" x 15" x 30" | 30" | 96" | 30" | 96" | 64" | 15" | 10" | 15" | Yes | Yes | No | Yes | Yes | No |
| Rectangular 96" x 15" x 36" | 36" | 96" | 36" | 96" | 64" | 15" | 10" | 15" | Yes | Yes | No | Yes | Yes | No |
| Rectangular 96" x 15" x 42" | 42" | 96" | 42" | 96" | 64" | 15" | 10" | 15" | Yes | Yes | No | Yes | Yes | No |
| Rectangular 96" x 15" x 48" | 48" | 96" | 48" | 96" | 64" | 15" | 10" | 15" | Yes | Yes | No | Yes | Yes | No |
| Rectangular 96" x 15" x 54" | 54" | 96" | 54" | 96" | 64" | 15" | 10" | 15" | Yes | Yes | No | Yes | Yes | No |
| Rectangular 96" x 15" x 60" | 60" | 96" | 60" | 96" | 64" | 15" | 10" | 15" | Yes | Yes | No | Yes | Yes | No |
| Rectangular 96" x 18" x 18" | 18" | 96" | 18" | 96" | 64" | 18" | 12" | 18" | Yes | Yes | No | Yes | Yes | No |
| Rectangular 96" x 18" x 24" | 24" | 96" | 24" | 96" | 64" | 18" | 12" | 18" | Yes | Yes | No | Yes | Yes | No |
| Rectangular 96" x 18" x 30" | 30" | 96" | 30" | 96" | 64" | 18" | 12" | 18" | Yes | Yes | No | Yes | Yes | No |
| Rectangular 96" x 18" x 36" | 36" | 96" | 36" | 96" | 64" | 18" | 12" | 18" | Yes | Yes | No | Yes | Yes | No |
| Rectangular 96" x 18" x 42" | 42" | 96" | 42" | 96" | 64" | 18" | 12" | 18" | Yes | Yes | No | Yes | Yes | No |
| Rectangular 96" x 18" x 48" | 48" | 96" | 48" | 96" | 64" | 18" | 12" | 18" | Yes | Yes | No | Yes | Yes | No |
| Rectangular 96" x 18" x 54" | 54" | 96" | 54" | 96" | 64" | 18" | 12" | 18" | Yes | Yes | No | Yes | Yes | No |
| Rectangular 96" x 18" x 60" | 60" | 96" | 60" | 96" | 64" | 18" | 12" | 18" | Yes | Yes | No | Yes | Yes | No |
| Rectangular 96" x 24" x 18" | 18" | 96" | 18" | 96" | 64" | 24" | 16" | 24" | Yes | Yes | No | Yes | Yes | No |
| Rectangular 96" x 24" x 24" | 24" | 96" | 24" | 96" | 64" | 24" | 16" | 24" | Yes | Yes | No | Yes | Yes | No |
| Rectangular 96" x 24" x 30" | 30" | 96" | 30" | 96" | 64" | 24" | 16" | 24" | Yes | Yes | No | Yes | Yes | No |
| Rectangular 96" x 24" x 36" | 36" | 96" | 36" | 96" | 64" | 24" | 16" | 24" | Yes | Yes | No | Yes | Yes | No |
| Rectangular 96" x 24" x 42" | 42" | 96" | 42" | 96" | 64" | 24" | 16" | 24" | Yes | Yes | No | Yes | Yes | No |
| Rectangular 96" x 24" x 48" | 48" | 96" | 48" | 96" | 64" | 24" | 16" | 24" | Yes | Yes | No | Yes | Yes | No |
| Rectangular 96" x 24" x 54" | 54" | 96" | 54" | 96" | 64" | 24" | 16" | 24" | Yes | Yes | No | Yes | Yes | No |
| Rectangular 96" x 24" x 60" | 60" | 96" | 60" | 96" | 64" | 24" | 16" | 24" | Yes | Yes | No | Yes | Yes | No |
| Rectangular 96" x 30" x 18" | 18" | 96" | 18" | 96" | 64" | 30" | 20" | 30" | Yes | Yes | No | Yes | Yes | No |
| Rectangular 96" x 30" x 24" | 24" | 96" | 24" | 96" | 64" | 30" | 20" | 30" | Yes | Yes | No | Yes | Yes | No |
| Rectangular 96" x 30" x 30" | 30" | 96" | 30" | 96" | 64" | 30" | 20" | 30" | Yes | Yes | No | Yes | Yes | No |
| Rectangular 96" x 30" x 36" | 36" | 96" | 36" | 96" | 64" | 30" | 20" | 30" | Yes | Yes | No | Yes | Yes | No |
| Rectangular 96" x 30" x 42" | 42" | 96" | 42" | 96" | 64" | 30" | 20" | 30" | Yes | Yes | No | Yes | Yes | No |
| Rectangular 96" x 30" x 48" | 48" | 96" | 48" | 96" | 64" | 30" | 20" | 30" | Yes | Yes | No | Yes | Yes | No |
| Rectangular 96" x 30" x 54" | 54" | 96" | 54" | 96" | 64" | 30" | 20" | 30" | Yes | Yes | No | Yes | Yes | No |
| Rectangular 96" x 30" x 60" | 60" | 96" | 60" | 96" | 64" | 30" | 20" | 30" | Yes | Yes | No | Yes | Yes | No |
| Rectangular 96" x 36" x 18" | 18" | 96" | 18" | 96" | 64" | 36" | 24" | 36" | Yes | Yes | No | Yes | Yes | No |
| Rectangular 96" x 36" x 24" | 24" | 96" | 24" | 96" | 64" | 36" | 24" | 36" | Yes | Yes | No | Yes | Yes | No |
| Rectangular 96" x 36" x 30" | 30" | 96" | 30" | 96" | 64" | 36" | 24" | 36" | Yes | Yes | No | Yes | Yes | No |
| Rectangular 96" x 36" x 36" | 36" | 96" | 36" | 96" | 64" | 36" | 24" | 36" | Yes | Yes | No | Yes | Yes | No |
| Rectangular 96" x 36" x 42" | 42" | 96" | 42" | 96" | 64" | 36" | 24" | 36" | Yes | Yes | No | Yes | Yes | No |
| Rectangular 96" x 36" x 48" | 48" | 96" | 48" | 96" | 64" | 36" | 24" | 36" | Yes | Yes | No | Yes | Yes | No |
| Rectangular 96" x 36" x 54" | 54" | 96" | 54" | 96" | 64" | 36" | 24" | 36" | Yes | Yes | No | Yes | Yes | No |
| Rectangular 96" x 36" x 60" | 60" | 96" | 60" | 96" | 64" | 36" | 24" | 36" | Yes | Yes | No | Yes | Yes | No |
| Rectangular 96" x 42" x 18" | 18" | 96" | 18" | 96" | 64" | 42" | 28" | 42" | Yes | Yes | No | Yes | Yes | No |
| Rectangular 96" x 42" x 24" | 24" | 96" | 24" | 96" | 64" | 42" | 28" | 42" | Yes | Yes | No | Yes | Yes | No |
| Rectangular 96" x 42" x 30" | 30" | 96" | 30" | 96" | 64" | 42" | 28" | 42" | Yes | Yes | No | Yes | Yes | No |
| Rectangular 96" x 42" x 36" | 36" | 96" | 36" | 96" | 64" | 42" | 28" | 42" | Yes | Yes | No | Yes | Yes | No |
| Rectangular 96" x 42" x 42" | 42" | 96" | 42" | 96" | 64" | 42" | 28" | 42" | Yes | Yes | No | Yes | Yes | No |
| Rectangular 96" x 42" x 48" | 48" | 96" | 48" | 96" | 64" | 42" | 28" | 42" | Yes | Yes | No | Yes | Yes | No |
| Rectangular 96" x 42" x 54" | 54" | 96" | 54" | 96" | 64" | 42" | 28" | 42" | Yes | Yes | No | Yes | Yes | No |
| Rectangular 96" x 42" x 60" | 60" | 96" | 60" | 96" | 64" | 42" | 28" | 42" | Yes | Yes | No | Yes | Yes | No |
| Rectangular 96" x 48" x 18" | 18" | 96" | 18" | 96" | 64" | 48" | 32" | 48" | Yes | Yes | No | Yes | Yes | No |
| Rectangular 96" x 48" x 24" | 24" | 96" | 24" | 96" | 64" | 48" | 32" | 48" | Yes | Yes | No | Yes | Yes | No |
| Rectangular 96" x 48" x 30" | 30" | 96" | 30" | 96" | 64" | 48" | 32" | 48" | Yes | Yes | No | Yes | Yes | No |
| Rectangular 96" x 48" x 36" | 36" | 96" | 36" | 96" | 64" | 48" | 32" | 48" | Yes | Yes | No | Yes | Yes | No |
| Rectangular 96" x 48" x 42" | 42" | 96" | 42" | 96" | 64" | 48" | 32" | 48" | Yes | Yes | No | Yes | Yes | No |
| Rectangular 96" x 48" x 48" | 48" | 96" | 48" | 96" | 64" | 48" | 32" | 48" | Yes | Yes | No | Yes | Yes | No |
| Rectangular 96" x 48" x 54" | 54" | 96" | 54" | 96" | 64" | 48" | 32" | 48" | Yes | Yes | No | Yes | Yes | No |
| Rectangular 96" x 48" x 60" | 60" | 96" | 60" | 96" | 64" | 48" | 32" | 48" | Yes | Yes | No | Yes | Yes | No |
| Rectangular 96" x 60" x 18" | 18" | 96" | 18" | 96" | 64" | 60" | 40" | 60" | Yes | Yes | No | Yes | Yes | No |
| Rectangular 96" x 60" x 24" | 24" | 96" | 24" | 96" | 64" | 60" | 40" | 60" | Yes | Yes | No | Yes | Yes | No |
| Rectangular 96" x 60" x 30" | 30" | 96" | 30" | 96" | 64" | 60" | 40" | 60" | Yes | Yes | No | Yes | Yes | No |
| Rectangular 96" x 60" x 36" | 36" | 96" | 36" | 96" | 64" | 60" | 40" | 60" | Yes | Yes | No | Yes | Yes | No |
| Rectangular 96" x 60" x 42" | 42" | 96" | 42" | 96" | 64" | 60" | 40" | 60" | Yes | Yes | No | Yes | Yes | No |
| Rectangular 96" x 60" x 48" | 48" | 96" | 48" | 96" | 64" | 60" | 40" | 60" | Yes | Yes | No | Yes | Yes | No |
| Rectangular 96" x 60" x 54" | 54" | 96" | 54" | 96" | 64" | 60" | 40" | 60" | Yes | Yes | No | Yes | Yes | No |
| Rectangular 96" x 60" x 60" | 60" | 96" | 60" | 96" | 64" | 60" | 40" | 60" | Yes | Yes | No | Yes | Yes | No |
| Rectangular 96" x 66" x 18" | 18" | 96" | 18" | 96" | 64" | 66" | 44" | 66" | Yes | Yes | No | Yes | Yes | No |
| Rectangular 96" x 66" x 24" | 24" | 96" | 24" | 96" | 64" | 66" | 44" | 66" | Yes | Yes | No | Yes | Yes | No |
| Rectangular 96" x 66" x 30" | 30" | 96" | 30" | 96" | 64" | 66" | 44" | 66" | Yes | Yes | No | Yes | Yes | No |
| Rectangular 96" x 66" x 36" | 36" | 96" | 36" | 96" | 64" | 66" | 44" | 66" | Yes | Yes | No | Yes | Yes | No |
| Rectangular 96" x 66" x 42" | 42" | 96" | 42" | 96" | 64" | 66" | 44" | 66" | Yes | Yes | No | Yes | Yes | No |
| Rectangular 96" x 66" x 48" | 48" | 96" | 48" | 96" | 64" | 66" | 44" | 66" | Yes | Yes | No | Yes | Yes | No |
| Rectangular 96" x 66" x 54" | 54" | 96" | 54" | 96" | 64" | 66" | 44" | 66" | Yes | Yes | No | Yes | Yes | No |
| Rectangular 96" x 66" x 60" | 60" | 96" | 60" | 96" | 64" | 66" | 44" | 66" | Yes | Yes | No | Yes | Yes | No |
| Rectangular 96" x 72" x 18" | 18" | 96" | 18" | 96" | 64" | 72" | 48" | 72" | Yes | Yes | No | Yes | Yes | No |
| Rectangular 96" x 72" x 24" | 24" | 96" | 24" | 96" | 64" | 72" | 48" | 72" | Yes | Yes | No | Yes | Yes | No |
| Rectangular 96" x 72" x 30" | 30" | 96" | 30" | 96" | 64" | 72" | 48" | 72" | Yes | Yes | No | Yes | Yes | No |
| Rectangular 96" x 72" x 36" | 36" | 96" | 36" | 96" | 64" | 72" | 48" | 72" | Yes | Yes | No | Yes | Yes | No |
| Rectangular 96" x 72" x 42" | 42" | 96" | 42" | 96" | 64" | 72" | 48" | 72" | Yes | Yes | No | Yes | Yes | No |
| Rectangular 96" x 72" x 48" | 48" | 96" | 48" | 96" | 64" | 72" | 48" | 72" | Yes | Yes | No | Yes | Yes | No |
| Rectangular 96" x 72" x 54" | 54" | 96" | 54" | 96" | 64" | 72" | 48" | 72" | Yes | Yes | No | Yes | Yes | No |
| Rectangular 96" x 72" x 60" | 60" | 96" | 60" | 96" | 64" | 72" | 48" | 72" | Yes | Yes | No | Yes | Yes | No |
| Rectangular 108" x 12" x 18" | 18" | 108" | 18" | 108" | 72" | 12" | 8" | 12" | Yes | Yes | No | Yes | Yes | No |
| Rectangular 108" x 12" x 24" | 24" | 108" | 24" | 108" | 72" | 12" | 8" | 12" | Yes | Yes | No | Yes | Yes | No |
| Rectangular 108" x 12" x 30" | 30" | 108" | 30" | 108" | 72" | 12" | 8" | 12" | Yes | Yes | No | Yes | Yes | No |
| Rectangular 108" x 12" x 36" | 36" | 108" | 36" | 108" | 72" | 12" | 8" | 12" | Yes | Yes | No | Yes | Yes | No |
| Rectangular 108" x 15" x 18" | 18" | 108" | 18" | 108" | 72" | 15" | 10" | 15" | Yes | Yes | No | Yes | Yes | No |
| Rectangular 108" x 15" x 24" | 24" | 108" | 24" | 108" | 72" | 15" | 10" | 15" | Yes | Yes | No | Yes | Yes | No |
| Rectangular 108" x 15" x 30" | 30" | 108" | 30" | 108" | 72" | 15" | 10" | 15" | Yes | Yes | No | Yes | Yes | No |
| Rectangular 108" x 15" x 36" | 36" | 108" | 36" | 108" | 72" | 15" | 10" | 15" | Yes | Yes | No | Yes | Yes | No |
| Rectangular 108" x 15" x 42" | 42" | 108" | 42" | 108" | 72" | 15" | 10" | 15" | Yes | Yes | No | Yes | Yes | No |
| Rectangular 108" x 15" x 48" | 48" | 108" | 48" | 108" | 72" | 15" | 10" | 15" | Yes | Yes | No | Yes | Yes | No |
| Rectangular 108" x 15" x 54" | 54" | 108" | 54" | 108" | 72" | 15" | 10" | 15" | Yes | Yes | No | Yes | Yes | No |
| Rectangular 108" x 15" x 60" | 60" | 108" | 60" | 108" | 72" | 15" | 10" | 15" | Yes | Yes | No | Yes | Yes | No |
| Rectangular 108" x 18" x 18" | 18" | 108" | 18" | 108" | 72" | 18" | 12" | 18" | Yes | Yes | No | Yes | Yes | No |
| Rectangular 108" x 18" x 24" | 24" | 108" | 24" | 108" | 72" | 18" | 12" | 18" | Yes | Yes | No | Yes | Yes | No |
| Rectangular 108" x 18" x 30" | 30" | 108" | 30" | 108" | 72" | 18" | 12" | 18" | Yes | Yes | No | Yes | Yes | No |
| Rectangular 108" x 18" x 36" | 36" | 108" | 36" | 108" | 72" | 18" | 12" | 18" | Yes | Yes | No | Yes | Yes | No |
| Rectangular 108" x 18" x 42" | 42" | 108" | 42" | 108" | 72" | 18" | 12" | 18" | Yes | Yes | No | Yes | Yes | No |
| Rectangular 108" x 18" x 48" | 48" | 108" | 48" | 108" | 72" | 18" | 12" | 18" | Yes | Yes | No | Yes | Yes | No |
| Rectangular 108" x 18" x 54" | 54" | 108" | 54" | 108" | 72" | 18" | 12" | 18" | Yes | Yes | No | Yes | Yes | No |
| Rectangular 108" x 18" x 60" | 60" | 108" | 60" | 108" | 72" | 18" | 12" | 18" | Yes | Yes | No | Yes | Yes | No |
| Rectangular 108" x 24" x 18" | 18" | 108" | 18" | 108" | 72" | 24" | 16" | 24" | Yes | Yes | No | Yes | Yes | No |
| Rectangular 108" x 24" x 24" | 24" | 108" | 24" | 108" | 72" | 24" | 16" | 24" | Yes | Yes | No | Yes | Yes | No |
| Rectangular 108" x 24" x 30" | 30" | 108" | 30" | 108" | 72" | 24" | 16" | 24" | Yes | Yes | No | Yes | Yes | No |
| Rectangular 108" x 24" x 36" | 36" | 108" | 36" | 108" | 72" | 24" | 16" | 24" | Yes | Yes | No | Yes | Yes | No |
| Rectangular 108" x 24" x 42" | 42" | 108" | 42" | 108" | 72" | 24" | 16" | 24" | Yes | Yes | No | Yes | Yes | No |
| Rectangular 108" x 24" x 48" | 48" | 108" | 48" | 108" | 72" | 24" | 16" | 24" | Yes | Yes | No | Yes | Yes | No |
| Rectangular 108" x 24" x 54" | 54" | 108" | 54" | 108" | 72" | 24" | 16" | 24" | Yes | Yes | No | Yes | Yes | No |
| Rectangular 108" x 24" x 60" | 60" | 108" | 60" | 108" | 72" | 24" | 16" | 24" | Yes | Yes | No | Yes | Yes | No |
| Rectangular 108" x 30" x 18" | 18" | 108" | 18" | 108" | 72" | 30" | 20" | 30" | Yes | Yes | No | Yes | Yes | No |
| Rectangular 108" x 30" x 24" | 24" | 108" | 24" | 108" | 72" | 30" | 20" | 30" | Yes | Yes | No | Yes | Yes | No |
| Rectangular 108" x 30" x 30" | 30" | 108" | 30" | 108" | 72" | 30" | 20" | 30" | Yes | Yes | No | Yes | Yes | No |
| Rectangular 108" x 30" x 36" | 36" | 108" | 36" | 108" | 72" | 30" | 20" | 30" | Yes | Yes | No | Yes | Yes | No |
| Rectangular 108" x 30" x 42" | 42" | 108" | 42" | 108" | 72" | 30" | 20" | 30" | Yes | Yes | No | Yes | Yes | No |
| Rectangular 108" x 30" x 48" | 48" | 108" | 48" | 108" | 72" | 30" | 20" | 30" | Yes | Yes | No | Yes | Yes | No |
| Rectangular 108" x 30" x 54" | 54" | 108" | 54" | 108" | 72" | 30" | 20" | 30" | Yes | Yes | No | Yes | Yes | No |
| Rectangular 108" x 30" x 60" | 60" | 108" | 60" | 108" | 72" | 30" | 20" | 30" | Yes | Yes | No | Yes | Yes | No |
| Rectangular 108" x 36" x 18" | 18" | 108" | 18" | 108" | 72" | 36" | 24" | 36" | Yes | Yes | No | Yes | Yes | No |
| Rectangular 108" x 36" x 24" | 24" | 108" | 24" | 108" | 72" | 36" | 24" | 36" | Yes | Yes | No | Yes | Yes | No |
| Rectangular 108" x 36" x 30" | 30" | 108" | 30" | 108" | 72" | 36" | 24" | 36" | Yes | Yes | No | Yes | Yes | No |
| Rectangular 108" x 36" x 36" | 36" | 108" | 36" | 108" | 72" | 36" | 24" | 36" | Yes | Yes | No | Yes | Yes | No |
| Rectangular 108" x 36" x 42" | 42" | 108" | 42" | 108" | 72" | 36" | 24" | 36" | Yes | Yes | No | Yes | Yes | No |
| Rectangular 108" x 36" x 48" | 48" | 108" | 48" | 108" | 72" | 36" | 24" | 36" | Yes | Yes | No | Yes | Yes | No |
| Rectangular 108" x 36" x 54" | 54" | 108" | 54" | 108" | 72" | 36" | 24" | 36" | Yes | Yes | No | Yes | Yes | No |
| Rectangular 108" x 36" x 60" | 60" | 108" | 60" | 108" | 72" | 36" | 24" | 36" | Yes | Yes | No | Yes | Yes | No |
| Rectangular 108" x 42" x 18" | 18" | 108" | 18" | 108" | 72" | 42" | 28" | 42" | Yes | Yes | No | Yes | Yes | No |
| Rectangular 108" x 42" x 24" | 24" | 108" | 24" | 108" | 72" | 42" | 28" | 42" | Yes | Yes | No | Yes | Yes | No |
| Rectangular 108" x 42" x 30" | 30" | 108" | 30" | 108" | 72" | 42" | 28" | 42" | Yes | Yes | No | Yes | Yes | No |
| Rectangular 108" x 42" x 36" | 36" | 108" | 36" | 108" | 72" | 42" | 28" | 42" | Yes | Yes | No | Yes | Yes | No |
| Rectangular 108" x 42" x 42" | 42" | 108" | 42" | 108" | 72" | 42" | 28" | 42" | Yes | Yes | No | Yes | Yes | No |
| Rectangular 108" x 42" x 48" | 48" | 108" | 48" | 108" | 72" | 42" | 28" | 42" | Yes | Yes | No | Yes | Yes | No |
| Rectangular 108" x 42" x 54" | 54" | 108" | 54" | 108" | 72" | 42" | 28" | 42" | Yes | Yes | No | Yes | Yes | No |
| Rectangular 108" x 42" x 60" | 60" | 108" | 60" | 108" | 72" | 42" | 28" | 42" | Yes | Yes | No | Yes | Yes | No |
| Rectangular 108" x 48" x 18" | 18" | 108" | 18" | 108" | 72" | 48" | 32" | 48" | Yes | Yes | No | Yes | Yes | No |
| Rectangular 108" x 48" x 24" | 24" | 108" | 24" | 108" | 72" | 48" | 32" | 48" | Yes | Yes | No | Yes | Yes | No |
| Rectangular 108" x 48" x 30" | 30" | 108" | 30" | 108" | 72" | 48" | 32" | 48" | Yes | Yes | No | Yes | Yes | No |
| Rectangular 108" x 48" x 36" | 36" | 108" | 36" | 108" | 72" | 48" | 32" | 48" | Yes | Yes | No | Yes | Yes | No |
| Rectangular 108" x 48" x 42" | 42" | 108" | 42" | 108" | 72" | 48" | 32" | 48" | Yes | Yes | No | Yes | Yes | No |
| Rectangular 108" x 48" x 48" | 48" | 108" | 48" | 108" | 72" | 48" | 32" | 48" | Yes | Yes | No | Yes | Yes | No |
| Rectangular 108" x 48" x 54" | 54" | 108" | 54" | 108" | 72" | 48" | 32" | 48" | Yes | Yes | No | Yes | Yes | No |
| Rectangular 108" x 48" x 60" | 60" | 108" | 60" | 108" | 72" | 48" | 32" | 48" | Yes | Yes | No | Yes | Yes | No |
| Rectangular 108" x 60" x 18" | 18" | 108" | 18" | 108" | 72" | 60" | 40" | 60" | Yes | Yes | No | Yes | Yes | No |
| Rectangular 108" x 60" x 24" | 24" | 108" | 24" | 108" | 72" | 60" | 40" | 60" | Yes | Yes | No | Yes | Yes | No |
| Rectangular 108" x 60" x 30" | 30" | 108" | 30" | 108" | 72" | 60" | 40" | 60" | Yes | Yes | No | Yes | Yes | No |
| Rectangular 108" x 60" x 36" | 36" | 108" | 36" | 108" | 72" | 60" | 40" | 60" | Yes | Yes | No | Yes | Yes | No |
| Rectangular 108" x 60" x 42" | 42" | 108" | 42" | 108" | 72" | 60" | 40" | 60" | Yes | Yes | No | Yes | Yes | No |
| Rectangular 108" x 60" x 48" | 48" | 108" | 48" | 108" | 72" | 60" | 40" | 60" | Yes | Yes | No | Yes | Yes | No |
| Rectangular 108" x 60" x 54" | 54" | 108" | 54" | 108" | 72" | 60" | 40" | 60" | Yes | Yes | No | Yes | Yes | No |
| Rectangular 108" x 60" x 60" | 60" | 108" | 60" | 108" | 72" | 60" | 40" | 60" | Yes | Yes | No | Yes | Yes | No |
| Rectangular 108" x 66" x 18" | 18" | 108" | 18" | 108" | 72" | 66" | 44" | 66" | Yes | Yes | No | Yes | Yes | No |
| Rectangular 108" x 66" x 24" | 24" | 108" | 24" | 108" | 72" | 66" | 44" | 66" | Yes | Yes | No | Yes | Yes | No |
| Rectangular 108" x 66" x 30" | 30" | 108" | 30" | 108" | 72" | 66" | 44" | 66" | Yes | Yes | No | Yes | Yes | No |
| Rectangular 108" x 66" x 36" | 36" | 108" | 36" | 108" | 72" | 66" | 44" | 66" | Yes | Yes | No | Yes | Yes | No |
| Rectangular 108" x 66" x 42" | 42" | 108" | 42" | 108" | 72" | 66" | 44" | 66" | Yes | Yes | No | Yes | Yes | No |
| Rectangular 108" x 66" x 48" | 48" | 108" | 48" | 108" | 72" | 66" | 44" | 66" | Yes | Yes | No | Yes | Yes | No |
| Rectangular 108" x 66" x 54" | 54" | 108" | 54" | 108" | 72" | 66" | 44" | 66" | Yes | Yes | No | Yes | Yes | No |
| Rectangular 108" x 66" x 60" | 60" | 108" | 60" | 108" | 72" | 66" | 44" | 66" | Yes | Yes | No | Yes | Yes | No |
| Rectangular 108" x 72" x 18" | 18" | 108" | 18" | 108" | 72" | 72" | 48" | 72" | Yes | Yes | No | Yes | Yes | No |
| Rectangular 108" x 72" x 24" | 24" | 108" | 24" | 108" | 72" | 72" | 48" | 72" | Yes | Yes | No | Yes | Yes | No |
| Rectangular 108" x 72" x 30" | 30" | 108" | 30" | 108" | 72" | 72" | 48" | 72" | Yes | Yes | No | Yes | Yes | No |
| Rectangular 108" x 72" x 36" | 36" | 108" | 36" | 108" | 72" | 72" | 48" | 72" | Yes | Yes | No | Yes | Yes | No |
| Rectangular 108" x 72" x 42" | 42" | 108" | 42" | 108" | 72" | 72" | 48" | 72" | Yes | Yes | No | Yes | Yes | No |
| Rectangular 108" x 72" x 48" | 48" | 108" | 48" | 108" | 72" | 72" | 48" | 72" | Yes | Yes | No | Yes | Yes | No |
| Rectangular 108" x 72" x 54" | 54" | 108" | 54" | 108" | 72" | 72" | 48" | 72" | Yes | Yes | No | Yes | Yes | No |
| Rectangular 108" x 72" x 60" | 60" | 108" | 60" | 108" | 72" | 72" | 48" | 72" | Yes | Yes | No | Yes | Yes | No |
| Rectangular 120" x 12" x 18" | 18" | 120" | 18" | 120" | 80" | 12" | 8" | 12" | Yes | Yes | No | Yes | Yes | No |
| Rectangular 120" x 12" x 24" | 24" | 120" | 24" | 120" | 80" | 12" | 8" | 12" | Yes | Yes | No | Yes | Yes | No |
| Rectangular 120" x 12" x 30" | 30" | 120" | 30" | 120" | 80" | 12" | 8" | 12" | Yes | Yes | No | Yes | Yes | No |
| Rectangular 120" x 12" x 36" | 36" | 120" | 36" | 120" | 80" | 12" | 8" | 12" | Yes | Yes | No | Yes | Yes | No |
| Rectangular 120" x 15" x 18" | 18" | 120" | 18" | 120" | 80" | 15" | 10" | 15" | Yes | Yes | No | Yes | Yes | No |
| Rectangular 120" x 15" x 24" | 24" | 120" | 24" | 120" | 80" | 15" | 10" | 15" | Yes | Yes | No | Yes | Yes | No |
| Rectangular 120" x 15" x 30" | 30" | 120" | 30" | 120" | 80" | 15" | 10" | 15" | Yes | Yes | No | Yes | Yes | No |
| Rectangular 120" x 15" x 36" | 36" | 120" | 36" | 120" | 80" | 15" | 10" | 15" | Yes | Yes | No | Yes | Yes | No |
| Rectangular 120" x 15" x 42" | 42" | 120" | 42" | 120" | 80" | 15" | 10" | 15" | Yes | Yes | No | Yes | Yes | No |
| Rectangular 120" x 15" x 48" | 48" | 120" | 48" | 120" | 80" | 15" | 10" | 15" | Yes | Yes | No | Yes | Yes | No |
| Rectangular 120" x 15" x 54" | 54" | 120" | 54" | 120" | 80" | 15" | 10" | 15" | Yes | Yes | No | Yes | Yes | No |
| Rectangular 120" x 15" x 60" | 60" | 120" | 60" | 120" | 80" | 15" | 10" | 15" | Yes | Yes | No | Yes | Yes | No |
| Rectangular 120" x 18" x 18" | 18" | 120" | 18" | 120" | 80" | 18" | 12" | 18" | Yes | Yes | No | Yes | Yes | No |
| Rectangular 120" x 18" x 24" | 24" | 120" | 24" | 120" | 80" | 18" | 12" | 18" | Yes | Yes | No | Yes | Yes | No |
| Rectangular 120" x 18" x 30" | 30" | 120" | 30" | 120" | 80" | 18" | 12" | 18" | Yes | Yes | No | Yes | Yes | No |
| Rectangular 120" x 18" x 36" | 36" | 120" | 36" | 120" | 80" | 18" | 12" | 18" | Yes | Yes | No | Yes | Yes | No |
| Rectangular 120" x 18" x 42" | 42" | 120" | 42" | 120" | 80" | 18" | 12" | 18" | Yes | Yes | No | Yes | Yes | No |
| Rectangular 120" x 18" x 48" | 48" | 120" | 48" | 120" | 80" | 18" | 12" | 18" | Yes | Yes | No | Yes | Yes | No |
| Rectangular 120" x 18" x 54" | 54" | 120" | 54" | 120" | 80" | 18" | 12" | 18" | Yes | Yes | No | Yes | Yes | No |
| Rectangular 120" x 18" x 60" | 60" | 120" | 60" | 120" | 80" | 18" | 12" | 18" | Yes | Yes | No | Yes | Yes | No |
| Rectangular 120" x 24" x 18" | 18" | 120" | 18" | 120" | 80" | 24" | 16" | 24" | Yes | Yes | No | Yes | Yes | No |
| Rectangular 120" x 24" x 24" | 24" | 120" | 24" | 120" | 80" | 24" | 16" | 24" | Yes | Yes | No | Yes | Yes | No |
| Rectangular 120" x 24" x 30" | 30" | 120" | 30" | 120" | 80" | 24" | 16" | 24" | Yes | Yes | No | Yes | Yes | No |
| Rectangular 120" x 24" x 36" | 36" | 120" | 36" | 120" | 80" | 24" | 16" | 24" | Yes | Yes | No | Yes | Yes | No |
| Rectangular 120" x 24" x 42" | 42" | 120" | 42" | 120" | 80" | 24" | 16" | 24" | Yes | Yes | No | Yes | Yes | No |
| Rectangular 120" x 24" x 48" | 48" | 120" | 48" | 120" | 80" | 24" | 16" | 24" | Yes | Yes | No | Yes | Yes | No |
| Rectangular 120" x 24" x 54" | 54" | 120" | 54" | 120" | 80" | 24" | 16" | 24" | Yes | Yes | No | Yes | Yes | No |
| Rectangular 120" x 24" x 60" | 60" | 120" | 60" | 120" | 80" | 24" | 16" | 24" | Yes | Yes | No | Yes | Yes | No |
| Rectangular 120" x 30" x 18" | 18" | 120" | 18" | 120" | 80" | 30" | 20" | 30" | Yes | Yes | No | Yes | Yes | No |
| Rectangular 120" x 30" x 24" | 24" | 120" | 24" | 120" | 80" | 30" | 20" | 30" | Yes | Yes | No | Yes | Yes | No |
| Rectangular 120" x 30" x 30" | 30" | 120" | 30" | 120" | 80" | 30" | 20" | 30" | Yes | Yes | No | Yes | Yes | No |
| Rectangular 120" x 30" x 36" | 36" | 120" | 36" | 120" | 80" | 30" | 20" | 30" | Yes | Yes | No | Yes | Yes | No |
| Rectangular 120" x 30" x 42" | 42" | 120" | 42" | 120" | 80" | 30" | 20" | 30" | Yes | Yes | No | Yes | Yes | No |
| Rectangular 120" x 30" x 48" | 48" | 120" | 48" | 120" | 80" | 30" | 20" | 30" | Yes | Yes | No | Yes | Yes | No |
| Rectangular 120" x 30" x 54" | 54" | 120" | 54" | 120" | 80" | 30" | 20" | 30" | Yes | Yes | No | Yes | Yes | No |
| Rectangular 120" x 30" x 60" | 60" | 120" | 60" | 120" | 80" | 30" | 20" | 30" | Yes | Yes | No | Yes | Yes | No |
| Rectangular 120" x 36" x 18" | 18" | 120" | 18" | 120" | 80" | 36" | 24" | 36" | Yes | Yes | No | Yes | Yes | No |
| Rectangular 120" x 36" x 24" | 24" | 120" | 24" | 120" | 80" | 36" | 24" | 36" | Yes | Yes | No | Yes | Yes | No |
| Rectangular 120" x 36" x 30" | 30" | 120" | 30" | 120" | 80" | 36" | 24" | 36" | Yes | Yes | No | Yes | Yes | No |
| Rectangular 120" x 36" x 36" | 36" | 120" | 36" | 120" | 80" | 36" | 24" | 36" | Yes | Yes | No | Yes | Yes | No |
| Rectangular 120" x 36" x 42" | 42" | 120" | 42" | 120" | 80" | 36" | 24" | 36" | Yes | Yes | No | Yes | Yes | No |
| Rectangular 120" x 36" x 48" | 48" | 120" | 48" | 120" | 80" | 36" | 24" | 36" | Yes | Yes | No | Yes | Yes | No |
| Rectangular 120" x 36" x 54" | 54" | 120" | 54" | 120" | 80" | 36" | 24" | 36" | Yes | Yes | No | Yes | Yes | No |
| Rectangular 120" x 36" x 60" | 60" | 120" | 60" | 120" | 80" | 36" | 24" | 36" | Yes | Yes | No | Yes | Yes | No |
| Rectangular 120" x 42" x 18" | 18" | 120" | 18" | 120" | 80" | 42" | 28" | 42" | Yes | Yes | No | Yes | Yes | No |
| Rectangular 120" x 42" x 24" | 24" | 120" | 24" | 120" | 80" | 42" | 28" | 42" | Yes | Yes | No | Yes | Yes | No |
| Rectangular 120" x 42" x 30" | 30" | 120" | 30" | 120" | 80" | 42" | 28" | 42" | Yes | Yes | No | Yes | Yes | No |
| Rectangular 120" x 42" x 36" | 36" | 120" | 36" | 120" | 80" | 42" | 28" | 42" | Yes | Yes | No | Yes | Yes | No |
| Rectangular 120" x 42" x 42" | 42" | 120" | 42" | 120" | 80" | 42" | 28" | 42" | Yes | Yes | No | Yes | Yes | No |
| Rectangular 120" x 42" x 48" | 48" | 120" | 48" | 120" | 80" | 42" | 28" | 42" | Yes | Yes | No | Yes | Yes | No |
| Rectangular 120" x 42" x 54" | 54" | 120" | 54" | 120" | 80" | 42" | 28" | 42" | Yes | Yes | No | Yes | Yes | No |
| Rectangular 120" x 42" x 60" | 60" | 120" | 60" | 120" | 80" | 42" | 28" | 42" | Yes | Yes | No | Yes | Yes | No |
| Rectangular 120" x 48" x 18" | 18" | 120" | 18" | 120" | 80" | 48" | 32" | 48" | Yes | Yes | No | Yes | Yes | No |
| Rectangular 120" x 48" x 24" | 24" | 120" | 24" | 120" | 80" | 48" | 32" | 48" | Yes | Yes | No | Yes | Yes | No |
| Rectangular 120" x 48" x 30" | 30" | 120" | 30" | 120" | 80" | 48" | 32" | 48" | Yes | Yes | No | Yes | Yes | No |
| Rectangular 120" x 48" x 36" | 36" | 120" | 36" | 120" | 80" | 48" | 32" | 48" | Yes | Yes | No | Yes | Yes | No |
| Rectangular 120" x 48" x 42" | 42" | 120" | 42" | 120" | 80" | 48" | 32" | 48" | Yes | Yes | No | Yes | Yes | No |
| Rectangular 120" x 48" x 48" | 48" | 120" | 48" | 120" | 80" | 48" | 32" | 48" | Yes | Yes | No | Yes | Yes | No |
| Rectangular 120" x 48" x 54" | 54" | 120" | 54" | 120" | 80" | 48" | 32" | 48" | Yes | Yes | No | Yes | Yes | No |
| Rectangular 120" x 48" x 60" | 60" | 120" | 60" | 120" | 80" | 48" | 32" | 48" | Yes | Yes | No | Yes | Yes | No |
| Rectangular 120" x 60" x 18" | 18" | 120" | 18" | 120" | 80" | 60" | 40" | 60" | Yes | Yes | No | Yes | Yes | No |
| Rectangular 120" x 60" x 24" | 24" | 120" | 24" | 120" | 80" | 60" | 40" | 60" | Yes | Yes | No | Yes | Yes | No |
| Rectangular 120" x 60" x 30" | 30" | 120" | 30" | 120" | 80" | 60" | 40" | 60" | Yes | Yes | No | Yes | Yes | No |
| Rectangular 120" x 60" x 36" | 36" | 120" | 36" | 120" | 80" | 60" | 40" | 60" | Yes | Yes | No | Yes | Yes | No |
| Rectangular 120" x 60" x 42" | 42" | 120" | 42" | 120" | 80" | 60" | 40" | 60" | Yes | Yes | No | Yes | Yes | No |
| Rectangular 120" x 60" x 48" | 48" | 120" | 48" | 120" | 80" | 60" | 40" | 60" | Yes | Yes | No | Yes | Yes | No |
| Rectangular 120" x 60" x 54" | 54" | 120" | 54" | 120" | 80" | 60" | 40" | 60" | Yes | Yes | No | Yes | Yes | No |
| Rectangular 120" x 60" x 60" | 60" | 120" | 60" | 120" | 80" | 60" | 40" | 60" | Yes | Yes | No | Yes | Yes | No |
| Rectangular 120" x 66" x 18" | 18" | 120" | 18" | 120" | 80" | 66" | 44" | 66" | Yes | Yes | No | Yes | Yes | No |
| Rectangular 120" x 66" x 24" | 24" | 120" | 24" | 120" | 80" | 66" | 44" | 66" | Yes | Yes | No | Yes | Yes | No |
| Rectangular 120" x 66" x 30" | 30" | 120" | 30" | 120" | 80" | 66" | 44" | 66" | Yes | Yes | No | Yes | Yes | No |
| Rectangular 120" x 66" x 36" | 36" | 120" | 36" | 120" | 80" | 66" | 44" | 66" | Yes | Yes | No | Yes | Yes | No |
| Rectangular 120" x 66" x 42" | 42" | 120" | 42" | 120" | 80" | 66" | 44" | 66" | Yes | Yes | No | Yes | Yes | No |
| Rectangular 120" x 66" x 48" | 48" | 120" | 48" | 120" | 80" | 66" | 44" | 66" | Yes | Yes | No | Yes | Yes | No |
| Rectangular 120" x 66" x 54" | 54" | 120" | 54" | 120" | 80" | 66" | 44" | 66" | Yes | Yes | No | Yes | Yes | No |
| Rectangular 120" x 66" x 60" | 60" | 120" | 60" | 120" | 80" | 66" | 44" | 66" | Yes | Yes | No | Yes | Yes | No |
| Rectangular 120" x 72" x 18" | 18" | 120" | 18" | 120" | 80" | 72" | 48" | 72" | Yes | Yes | No | Yes | Yes | No |
| Rectangular 120" x 72" x 24" | 24" | 120" | 24" | 120" | 80" | 72" | 48" | 72" | Yes | Yes | No | Yes | Yes | No |
| Rectangular 120" x 72" x 30" | 30" | 120" | 30" | 120" | 80" | 72" | 48" | 72" | Yes | Yes | No | Yes | Yes | No |
| Rectangular 120" x 72" x 36" | 36" | 120" | 36" | 120" | 80" | 72" | 48" | 72" | Yes | Yes | No | Yes | Yes | No |
| Rectangular 120" x 72" x 42" | 42" | 120" | 42" | 120" | 80" | 72" | 48" | 72" | Yes | Yes | No | Yes | Yes | No |
| Rectangular 120" x 72" x 48" | 48" | 120" | 48" | 120" | 80" | 72" | 48" | 72" | Yes | Yes | No | Yes | Yes | No |
| Rectangular 120" x 72" x 54" | 54" | 120" | 54" | 120" | 80" | 72" | 48" | 72" | Yes | Yes | No | Yes | Yes | No |
| Rectangular 120" x 72" x 60" | 60" | 120" | 60" | 120" | 80" | 72" | 48" | 72" | Yes | Yes | No | Yes | Yes | No |

## geometry (parser evidence)
native form markers: Extrusion x1, Sweep x2
no freeform markers — native parametric forms only
